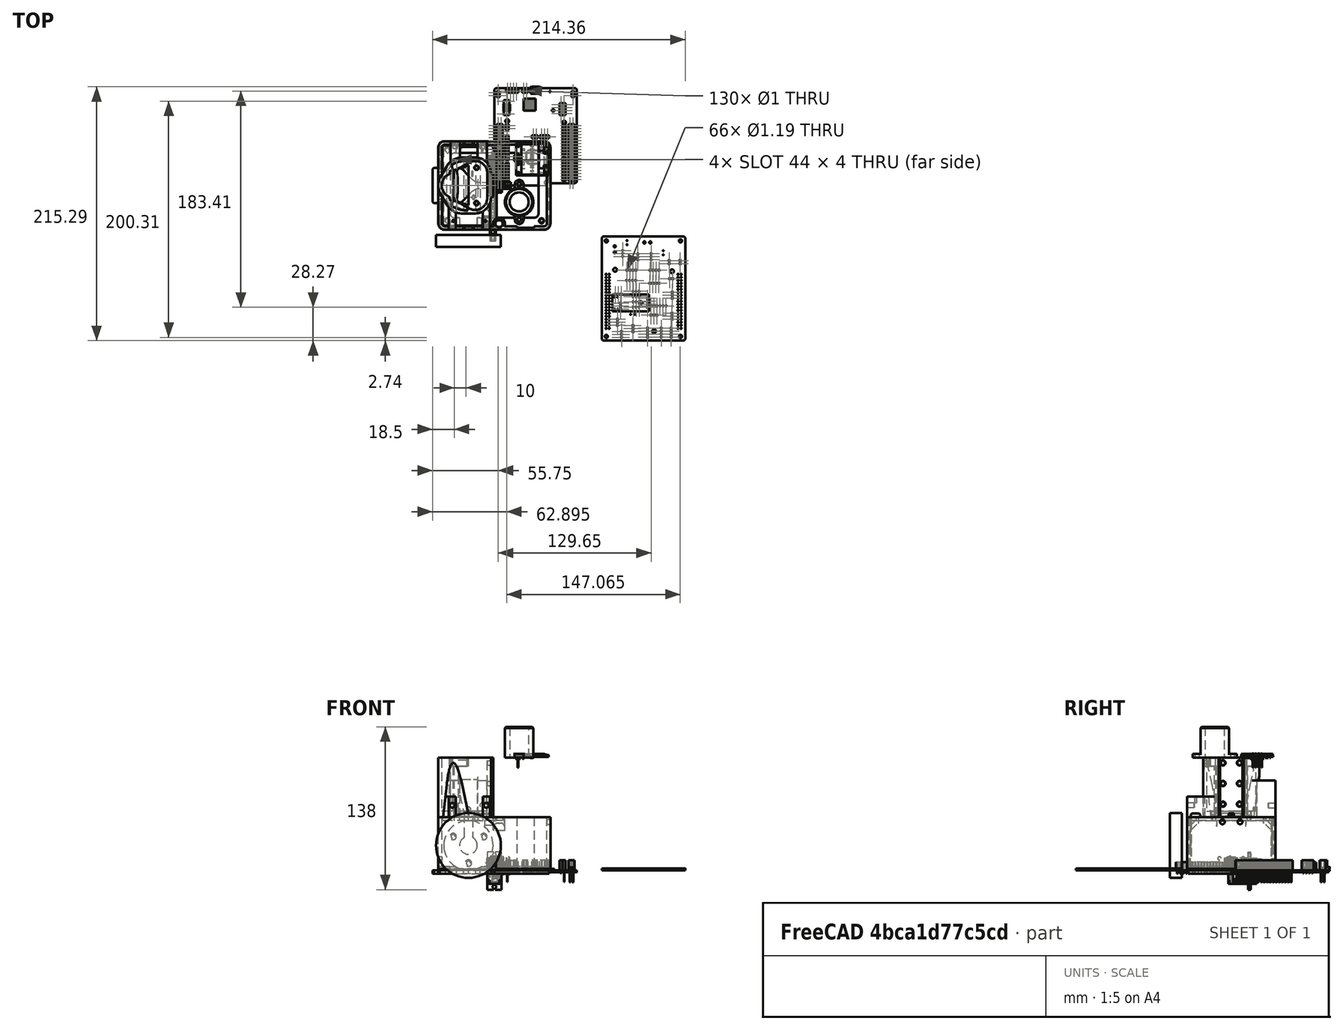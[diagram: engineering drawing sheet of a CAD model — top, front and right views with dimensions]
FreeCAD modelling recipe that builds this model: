
FCSTD DOCUMENT  (FreeCAD 1.0R38641 +678 (Git))
Label: Chassis_V3_PAMI
License: All rights reserved
LicenseURL: https://en.wikipedia.org/wiki/All_rights_reserved
objects: Part::Feature×336, Sketcher::SketchObject×61, App::Part×58, PartDesign::Pocket×46, PartDesign::Pad×18, PartDesign::Chamfer×15, PartDesign::Fillet×13, PartDesign::Body×8, PartDesign::Mirrored×7, Mesh::Feature×4, PartDesign::ShapeBinder×4, PartDesign::PolarPattern×3, PartDesign::Thickness×2, PartDesign::LinearPattern×2, PartDesign::Line×1, PartDesign::SubShapeBinder×1
note: 778 computed .brp shape members not serialized (recipe doc carries the construction recipe); baked Part::Feature solids carry a one-line shape summary decoded from their .brp
EXTERNAL_REF file=../MODEL PART/support_batterie_parkside_12V.FCStd obj=Part

FEATURE [Sketcher::SketchObject] Sketch
  ArcFitTolerance = 1e-06
  AttachmentSupport = -> [XY_Plane]
  FullyConstrained = true
  MakeInternals = false
  MapMode = 5
  sketch-geometry (5):
    g0: LineSegment StartX=47.5 StartY=-37.5 StartZ=0 EndX=47.5 EndY=37.5 EndZ=0
    g1: LineSegment StartX=47.5 StartY=37.5 StartZ=0 EndX=-47.5 EndY=37.5 EndZ=0
    g2: LineSegment StartX=-47.5 StartY=37.5 StartZ=0 EndX=-47.5 EndY=-37.5 EndZ=0
    g3: LineSegment StartX=-47.5 StartY=-37.5 StartZ=0 EndX=47.5 EndY=-37.5 EndZ=0
    g4: GeomPoint [constr] X=0 Y=0 Z=0
  constraints (12):
    c: Coincident(g0,g1)
    c: Coincident(g1,g2)
    c: Coincident(g2,g3)
    c: Coincident(g3,g0)
    c: Vertical(g0)
    c: Vertical(g2)
    c: Horizontal(g1)
    c: Horizontal(g3)
    c: Symmetric(g2,g0,g4)
    c: Coincident(g4,g-1)
    c: DistanceX(g1,g1) = 95
    c: DistanceY(g0,g0) = 75
FEATURE [PartDesign::Pad] Pad
  Direction = (0,0,1)
  Length = 45
  Length2 = 10
  Profile = -> Sketch
  ReferenceAxis = -> Sketch [N_Axis]
  Refine = true
  Suppressed = false
  Type = 0
FEATURE [PartDesign::Fillet] Fillet
  Base = -> Pad [Edge1,Edge2,Edge5,Edge8]
  BaseFeature = -> Pad
  Radius = 5
  Refine = true
  SupportTransform = false
  Suppressed = false
  UseAllEdges = false
FEATURE [PartDesign::Chamfer] Chamfer
  Angle = 45
  Base = -> Fillet [Edge7]
  BaseFeature = -> Fillet
  ChamferType = 0
  FlipDirection = false
  Refine = true
  Size = 1
  Size2 = 1
  SupportTransform = false
  Suppressed = false
  UseAllEdges = false
FEATURE [PartDesign::Thickness] Thickness
  Base = -> Chamfer [Face4]
  BaseFeature = -> Chamfer
  Intersection = true
  Join = 0
  Mode = 0
  Refine = true
  Reversed = true
  SupportTransform = false
  Suppressed = false
  Value = 3
FEATURE [Sketcher::SketchObject] Sketch001
  ArcFitTolerance = 1e-06
  AttachmentSupport = -> [Thickness]
  FullyConstrained = true
  MakeInternals = false
  MapMode = 5
  Placement = pos=(0,0,0) rot=(1,0,0;3.14159rad)
  sketch-geometry (5):
    g0: LineSegment StartX=-37.5 StartY=-27.5 StartZ=0 EndX=37.5 EndY=-27.5 EndZ=0
    g1: LineSegment StartX=37.5 StartY=-27.5 StartZ=0 EndX=37.5 EndY=27.5 EndZ=0
    g2: LineSegment StartX=37.5 StartY=27.5 StartZ=0 EndX=-37.5 EndY=27.5 EndZ=0
    g3: LineSegment StartX=-37.5 StartY=27.5 StartZ=0 EndX=-37.5 EndY=-27.5 EndZ=0
    g4: GeomPoint [constr] X=0 Y=0 Z=0
  constraints (12):
    c: Coincident(g0,g1)
    c: Coincident(g1,g2)
    c: Coincident(g2,g3)
    c: Coincident(g3,g0)
    c: Horizontal(g0)
    c: Horizontal(g2)
    c: Vertical(g1)
    c: Vertical(g3)
    c: Symmetric(g2,g0,g4)
    c: Coincident(g4,g-1)
    c: DistanceX(g2,g2) = 75
    c: DistanceY(g1,g1) = 55
FEATURE [PartDesign::Pocket] Pocket
  BaseFeature = -> Thickness
  Direction = (0,0,1)
  Length = 5
  Length2 = 5
  Profile = -> Sketch001
  ReferenceAxis = -> Sketch001 [N_Axis]
  Refine = true
  Suppressed = false
  Type = 1
FEATURE [PartDesign::Fillet] Fillet001
  Base = -> Pocket [Edge73,Edge75,Edge71,Edge69]
  BaseFeature = -> Pocket
  Radius = 4
  Refine = true
  SupportTransform = false
  Suppressed = false
  UseAllEdges = false
FEATURE [Sketcher::SketchObject] Sketch002
  ArcFitTolerance = 1e-06
  AttachmentSupport = -> [Fillet001]
  FullyConstrained = true
  MakeInternals = false
  MapMode = 5
  Placement = pos=(0,0,0) rot=(1,0,0;3.14159rad)
  sketch-geometry (6):
    g0: Circle CenterX=-40 CenterY=30 CenterZ=0 NormalX=0 NormalY=0 NormalZ=1 AngleXU=0 Radius=2.1
    g1: LineSegment [constr] StartX=-40 StartY=30 StartZ=0 EndX=-40 EndY=0 EndZ=0
    g2: LineSegment [constr] StartX=-40 StartY=0 StartZ=0 EndX=0 EndY=0 EndZ=0
    g3: LineSegment [constr] StartX=0 StartY=0 StartZ=0 EndX=0 EndY=30 EndZ=0
    g4: LineSegment [constr] StartX=0 StartY=30 StartZ=0 EndX=-40 EndY=30 EndZ=0
    g5: Circle CenterX=-40 CenterY=-30 CenterZ=0 NormalX=0 NormalY=0 NormalZ=1 AngleXU=0 Radius=2.1
  constraints (15):
    c: Diameter(g0) = 4.2
    c: Coincident(g1,g2)
    c: Coincident(g2,g3)
    c: Coincident(g3,g4)
    c: Coincident(g4,g1)
    c: Vertical(g1)
    c: Vertical(g3)
    c: Horizontal(g2)
    c: Horizontal(g4)
    c: Coincident(g1,g0)
    c: Coincident(g2,g-1)
    c: DistanceX(g4,g4) = 40
    c: DistanceY(g1,g1) = 30
    c: Equal(g5,g0)
    c: Symmetric(g0,g5,g2)
FEATURE [PartDesign::Pocket] Pocket001
  BaseFeature = -> Fillet001
  Direction = (0,0,1)
  Length = 5
  Length2 = 5
  Profile = -> Sketch002
  ReferenceAxis = -> Sketch002 [N_Axis]
  Refine = true
  Suppressed = false
  Type = 1
FEATURE [PartDesign::Chamfer] Chamfer001
  Angle = 45
  Base = -> Pocket001 [Edge9,Edge10]
  BaseFeature = -> Pocket001
  ChamferType = 0
  FlipDirection = false
  Refine = true
  Size = 0.4
  Size2 = 1
  SupportTransform = false
  Suppressed = false
  UseAllEdges = false
FEATURE [Sketcher::SketchObject] Sketch003
  ArcFitTolerance = 1e-06
  AttachmentSupport = -> [XZ_Plane]
  FullyConstrained = true
  MakeInternals = false
  MapMode = 5
  Placement = pos=(0,0,0) rot=(1,0,0;1.5708rad)
  sketch-geometry (1):
    g0: Circle CenterX=-22 CenterY=21 CenterZ=0 NormalX=0 NormalY=0 NormalZ=1 AngleXU=0 Radius=21
  constraints (3):
    c: Diameter(g0) = 42
    c: DistanceX(g0,g-1) = 22
    c: Tangent(g0,g-1)
FEATURE [PartDesign::Pocket] Pocket002
  BaseFeature = -> Chamfer001
  Direction = (0,1,-2e-16)
  Length = 69
  Length2 = 5
  Midplane = true
  Profile = -> Sketch003
  ReferenceAxis = -> Sketch003 [N_Axis]
  Refine = true
  Suppressed = false
  Type = 0
FEATURE [Sketcher::SketchObject] Sketch004
  ArcFitTolerance = 1e-06
  AttachmentSupport = -> [XZ_Plane]
  ExternalGeometry = -> [Sketch003]
  FullyConstrained = true
  MakeInternals = false
  MapMode = 5
  Placement = pos=(0,0,0) rot=(1,0,0;1.5708rad)
  sketch-geometry (1):
    g0: Circle CenterX=-22 CenterY=21 CenterZ=0 NormalX=0 NormalY=0 NormalZ=1 AngleXU=0 Radius=7.5
  constraints (2):
    c: Diameter(g0) = 15
    c: Coincident(g0,g-3)
FEATURE [PartDesign::Pocket] Pocket003
  BaseFeature = -> Pocket002
  Direction = (0,1,-2e-16)
  Length = 5
  Length2 = 5
  Midplane = true
  Profile = -> Sketch004
  ReferenceAxis = -> Sketch004 [N_Axis]
  Refine = true
  Suppressed = false
  Type = 1
FEATURE [Sketcher::SketchObject] Sketch005
  ArcFitTolerance = 1e-06
  AttachmentSupport = -> [XZ_Plane]
  ExternalGeometry = -> [Pocket003]
  FullyConstrained = true
  MakeInternals = false
  MapMode = 5
  Placement = pos=(0,0,0) rot=(1,0,0;1.5708rad)
  sketch-geometry (3):
    g0: Circle [constr] CenterX=-22 CenterY=21 CenterZ=0 NormalX=0 NormalY=0 NormalZ=1 AngleXU=0 Radius=15
    g1: LineSegment [constr] StartX=-22 StartY=21 StartZ=0 EndX=-22 EndY=6 EndZ=0
    g2: Circle CenterX=-22 CenterY=6 CenterZ=0 NormalX=0 NormalY=0 NormalZ=1 AngleXU=0 Radius=1.75
  constraints (7):
    c: Diameter(g0) = 30
    c: Coincident(g1,g0)
    c: PointOnObject(g1,g0)
    c: Vertical(g1)
    c: Coincident(g2,g1)
    c: Diameter(g2) = 3.5
    c: Coincident(g0,g-3)
FEATURE [PartDesign::Pocket] Pocket004
  BaseFeature = -> Pocket003
  Direction = (0,1,-2e-16)
  Length = 5
  Length2 = 5
  Midplane = true
  Profile = -> Sketch005
  ReferenceAxis = -> Sketch005 [N_Axis]
  Refine = true
  Suppressed = false
  Type = 1
FEATURE [PartDesign::Line] DatumLine
  AttacherType = Attacher::AttachEngineLine
  AttachmentSupport = -> [Pocket004]
  Length = 20
  MapMode = 19
  Placement = pos=(-22,37.5,21) rot=(1,0,0;1.5708rad)
  ResizeMode = 0
FEATURE [Sketcher::SketchObject] Sketch006
  ArcFitTolerance = 1e-06
  AttachmentSupport = -> [Pocket004]
  ExternalGeometry = -> [Pocket004]
  FullyConstrained = true
  MakeInternals = false
  MapMode = 5
  Placement = pos=(0,37.5,0) rot=(0,0.707107,0.707107;3.14159rad)
  sketch-geometry (1):
    g0: Circle CenterX=22 CenterY=6 CenterZ=0 NormalX=0 NormalY=0 NormalZ=1 AngleXU=0 Radius=2.75
  constraints (2):
    c: Coincident(g0,g-3)
    c: Diameter(g0) = 5.5
FEATURE [PartDesign::Pocket] Pocket005
  BaseFeature = -> Pocket004
  Direction = (0,-1,2e-16)
  Length = 1.5
  Length2 = 5
  Profile = -> Sketch006
  ReferenceAxis = -> Sketch006 [N_Axis]
  Refine = true
  Suppressed = false
  Type = 0
FEATURE [PartDesign::PolarPattern] PolarPattern001
  Angle = 360
  Axis = -> DatumLine
  BaseFeature = -> Pocket005
  Mode = 0
  Occurrences = 3
  Offset = 120
  Originals = -> [Pocket005,Pocket004]
  Refine = true
  Suppressed = false
  TransformMode = 0
FEATURE [Sketcher::SketchObject] Sketch007
  ArcFitTolerance = 1e-06
  AttachmentSupport = -> [PolarPattern001]
  ExternalGeometry = -> [PolarPattern001]
  FullyConstrained = true
  MakeInternals = false
  MapMode = 5
  Placement = pos=(0,-37.5,0) rot=(1,0,0;1.5708rad)
  sketch-geometry (1):
    g0: Circle CenterX=-22 CenterY=6 CenterZ=0 NormalX=0 NormalY=0 NormalZ=1 AngleXU=0 Radius=2.75
  constraints (2):
    c: Diameter(g0) = 5.5
    c: Coincident(g0,g-3)
FEATURE [PartDesign::Pocket] Pocket006
  BaseFeature = -> PolarPattern001
  Direction = (0,1,-2e-16)
  Length = 1.5
  Length2 = 5
  Profile = -> Sketch007
  ReferenceAxis = -> Sketch007 [N_Axis]
  Refine = true
  Suppressed = false
  Type = 0
FEATURE [PartDesign::PolarPattern] PolarPattern002
  Angle = 360
  Axis = -> DatumLine
  BaseFeature = -> Pocket006
  Mode = 0
  Occurrences = 3
  Offset = 120
  Originals = -> [Pocket006]
  Refine = true
  Suppressed = false
  TransformMode = 0
FEATURE [Sketcher::SketchObject] Sketch008
  ArcFitTolerance = 1e-06
  AttachmentSupport = -> [XZ_Plane]
  ExternalGeometry = -> [PolarPattern002]
  FullyConstrained = true
  MakeInternals = false
  MapMode = 5
  Placement = pos=(0,0,0) rot=(1,0,0;1.5708rad)
  sketch-geometry (5):
    g0: LineSegment StartX=-18.5 StartY=21 StartZ=0 EndX=-18.5 EndY=45 EndZ=0
    g1: LineSegment StartX=-18.5 StartY=45 StartZ=0 EndX=-25.5 EndY=45 EndZ=0
    g2: LineSegment StartX=-25.5 StartY=45 StartZ=0 EndX=-25.5 EndY=21 EndZ=0
    g3: LineSegment StartX=-25.5 StartY=21 StartZ=0 EndX=-18.5 EndY=21 EndZ=0
    g4: GeomPoint [constr] X=-22 Y=33 Z=0
  constraints (12):
    c: Coincident(g0,g1)
    c: Coincident(g1,g2)
    c: Coincident(g2,g3)
    c: Coincident(g3,g0)
    c: Vertical(g0)
    c: Vertical(g2)
    c: Horizontal(g1)
    c: Horizontal(g3)
    c: Symmetric(g2,g0,g4)
    c: PointOnObject(g1,g-3)
    c: DistanceX(g1,g1) = 7
    c: Symmetric(g2,g0,g-4)
FEATURE [PartDesign::Pocket] Pocket007
  BaseFeature = -> PolarPattern002
  Direction = (0,1,-2e-16)
  Length = 5
  Length2 = 5
  Midplane = true
  Profile = -> Sketch008
  ReferenceAxis = -> Sketch008 [N_Axis]
  Refine = true
  Suppressed = false
  Type = 1
FEATURE [PartDesign::Chamfer] Chamfer002
  Angle = 45
  Base = -> Pocket007 [Edge128,Edge127,Edge148,Edge144,Edge125,Edge131,Edge119,Edge130]
  BaseFeature = -> Pocket007
  ChamferType = 0
  FlipDirection = false
  Refine = true
  Size = 1
  Size2 = 1
  SupportTransform = false
  Suppressed = false
  UseAllEdges = false
FEATURE [Part::Feature] Part__Feature027  label="PinSocket_2x19_P254mm_Vertical"
  shape: bbox 5.08 x 48.26 x 10.1 mm, 1188 faces (baked)
FEATURE [App::Part] PinSocket_2x19_P2_54mm_Vertical  label="PinSocket_2x19_P2.54mm_Vertical"
  Group = -> [Part__Feature027]
  Origin = -> Origin029
  Placement = pos=(97.2797,-75.37,1.65) rot=(0,0,1;0rad)
FEATURE [Part::Feature] Part__Feature028  label="PinSocket_2x19_P254mm_Vertical001"
  shape: bbox 5.08 x 48.26 x 10.1 mm, 1188 faces (baked)
FEATURE [App::Part] PinSocket_2x19_P2_54mm_Vertical001  label="PinSocket_2x19_P2.54mm_Vertical001"
  Group = -> [Part__Feature028]
  Origin = -> Origin030
  Placement = pos=(158.25,-75.37,1.65) rot=(0,0,1;0rad)
FEATURE [Part::Feature] Part__Feature029  label="PCB"
  shape: bbox 70 x 82.5 x 1.644 mm, 168 faces (baked)
FEATURE [Part::Feature] Part__Feature030  label="PCB001"
  shape: bbox 12 x 12 x 1.56 mm, 842 faces (baked)
FEATURE [Part::Feature] Part__Feature031  label="PCB002"
  shape: bbox 10.1 x 10.1 x 1.6 mm, 6 faces (baked)
FEATURE [Part::Feature] Part__Feature032  label="PCB003"
  shape: bbox 2.54 x 5.207 x 2.54 mm, 69 faces (baked)
FEATURE [Part::Feature] Part__Feature033  label="PCB004"
  shape: bbox 0.889 x 3.429 x 10.92 mm, 38 faces (baked)
FEATURE [Part::Feature] Part__Feature034  label="PCB005"
  shape: bbox 2.599 x 5.159 x 8.38 mm, 6 faces (baked)
FEATURE [Part::Feature] Part__Feature035  label="PCB006"
  shape: bbox 2.54 x 5.207 x 2.54 mm, 69 faces (baked)
FEATURE [Part::Feature] Part__Feature036  label="PCB007"
  shape: bbox 0.889 x 3.429 x 10.92 mm, 38 faces (baked)
FEATURE [Part::Feature] Part__Feature037  label="PCB008"
  shape: bbox 2.599 x 5.159 x 8.38 mm, 6 faces (baked)
FEATURE [Part::Feature] Part__Feature038  label="PCB009"
  shape: bbox 7.62 x 2.54 x 10.92 mm, 160 faces (baked)
FEATURE [Part::Feature] Part__Feature039  label="PCB010"
  shape: bbox 7.83 x 2.75 x 8.38 mm, 6 faces (baked)
FEATURE [Part::Feature] Part__Feature040  label="PCB011"
  shape: bbox 8.2 x 5.4 x 3.3 mm, 428 faces (baked)
FEATURE [Part::Feature] Part__Feature041  label="PCB012"
  shape: bbox 7.999 x 4.599 x 2.9 mm, 6 faces (baked)
FEATURE [Part::Feature] Part__Feature042  label="PCB013"
  shape: bbox 8.12 x 5.42 x 2.9 mm, 6 faces (baked)
FEATURE [Part::Feature] Part__Feature043  label="PCB014"
  shape: bbox 0.8 x 0.4 x 0.002 mm, 10 faces (baked)
FEATURE [Part::Feature] Part__Feature044  label="PCB015"
  shape: bbox 0.7 x 1 x 0.4 mm, 14 faces (baked)
FEATURE [Part::Feature] Part__Feature045  label="PCB016"
  shape: bbox 0.8 x 0.4 x 0.2 mm, 8 faces (baked)
FEATURE [Part::Feature] Part__Feature046  label="PCB017"
  shape: bbox 0.8 x 0.8 x 0.2 mm, 6 faces (baked)
FEATURE [Part::Feature] Part__Feature047  label="PCB018"
  shape: bbox 0.81 x 1.51 x 0.6 mm, 6 faces (baked)
FEATURE [Part::Feature] Part__Feature048  label="PCB019"
  shape: bbox 5.207 x 2.54 x 2.54 mm, 69 faces (baked)
FEATURE [Part::Feature] Part__Feature049  label="PCB020"
  shape: bbox 3.429 x 0.889 x 10.92 mm, 38 faces (baked)
FEATURE [Part::Feature] Part__Feature050  label="PCB021"
  shape: bbox 5.159 x 2.599 x 8.38 mm, 6 faces (baked)
FEATURE [Part::Feature] Part__Feature051  label="PCB022"
  shape: bbox 2.6 x 1.35 x 1.1 mm, 38 faces (baked)
FEATURE [Part::Feature] Part__Feature052  label="PCB023"
  shape: bbox 1.92 x 1.57 x 1.17 mm, 6 faces (baked)
FEATURE [Part::Feature] Part__Feature053  label="PCB024"
  shape: bbox 0.5 x 0.5 x 0.01 mm, 3 faces (baked)
FEATURE [Part::Feature] Part__Feature054  label="PCB025"
  shape: bbox 10.15 x 10.15 x 0.45 mm, 6 faces (baked)
FEATURE [Part::Feature] Part__Feature055  label="PCB026"
  shape: bbox 0.29 x 0.29 x 0.29 mm, 1 faces (baked)
FEATURE [Part::Feature] Part__Feature056  label="PCB027"
  shape: bbox 0.29 x 0.29 x 0.29 mm, 1 faces (baked)
FEATURE [Part::Feature] Part__Feature057  label="PCB028"
  shape: bbox 0.29 x 0.29 x 0.29 mm, 1 faces (baked)
FEATURE [Part::Feature] Part__Feature058  label="PCB029"
  shape: bbox 0.29 x 0.29 x 0.29 mm, 1 faces (baked)
FEATURE [Part::Feature] Part__Feature059  label="PCB030"
  shape: bbox 0.29 x 0.29 x 0.29 mm, 1 faces (baked)
FEATURE [Part::Feature] Part__Feature060  label="PCB031"
  shape: bbox 0.29 x 0.29 x 0.29 mm, 1 faces (baked)
FEATURE [Part::Feature] Part__Feature061  label="PCB032"
  shape: bbox 0.29 x 0.29 x 0.29 mm, 1 faces (baked)
FEATURE [Part::Feature] Part__Feature062  label="PCB033"
  shape: bbox 0.29 x 0.29 x 0.29 mm, 1 faces (baked)
FEATURE [Part::Feature] Part__Feature063  label="PCB034"
  shape: bbox 0.29 x 0.29 x 0.29 mm, 1 faces (baked)
FEATURE [Part::Feature] Part__Feature064  label="PCB035"
  shape: bbox 0.29 x 0.29 x 0.29 mm, 1 faces (baked)
FEATURE [Part::Feature] Part__Feature065  label="PCB036"
  shape: bbox 0.29 x 0.29 x 0.29 mm, 1 faces (baked)
FEATURE [Part::Feature] Part__Feature066  label="PCB037"
  shape: bbox 0.29 x 0.29 x 0.29 mm, 1 faces (baked)
FEATURE [Part::Feature] Part__Feature067  label="PCB038"
  shape: bbox 0.29 x 0.29 x 0.29 mm, 1 faces (baked)
FEATURE [Part::Feature] Part__Feature068  label="PCB039"
  shape: bbox 0.29 x 0.29 x 0.29 mm, 1 faces (baked)
FEATURE [Part::Feature] Part__Feature069  label="PCB040"
  shape: bbox 0.29 x 0.29 x 0.29 mm, 1 faces (baked)
FEATURE [Part::Feature] Part__Feature070  label="PCB041"
  shape: bbox 0.29 x 0.29 x 0.29 mm, 1 faces (baked)
FEATURE [Part::Feature] Part__Feature071  label="PCB042"
  shape: bbox 0.29 x 0.29 x 0.29 mm, 1 faces (baked)
FEATURE [Part::Feature] Part__Feature072  label="PCB043"
  shape: bbox 0.29 x 0.29 x 0.29 mm, 1 faces (baked)
FEATURE [Part::Feature] Part__Feature073  label="PCB044"
  shape: bbox 0.29 x 0.29 x 0.29 mm, 1 faces (baked)
FEATURE [Part::Feature] Part__Feature074  label="PCB045"
  shape: bbox 0.29 x 0.29 x 0.29 mm, 1 faces (baked)
FEATURE [Part::Feature] Part__Feature075  label="PCB046"
  shape: bbox 0.29 x 0.29 x 0.29 mm, 1 faces (baked)
FEATURE [Part::Feature] Part__Feature076  label="PCB047"
  shape: bbox 0.29 x 0.29 x 0.29 mm, 1 faces (baked)
FEATURE [Part::Feature] Part__Feature077  label="PCB048"
  shape: bbox 0.29 x 0.29 x 0.29 mm, 1 faces (baked)
FEATURE [Part::Feature] Part__Feature078  label="PCB049"
  shape: bbox 0.29 x 0.29 x 0.29 mm, 1 faces (baked)
FEATURE [Part::Feature] Part__Feature079  label="PCB050"
  shape: bbox 0.29 x 0.29 x 0.29 mm, 1 faces (baked)
FEATURE [Part::Feature] Part__Feature080  label="PCB051"
  shape: bbox 0.29 x 0.29 x 0.29 mm, 1 faces (baked)
FEATURE [Part::Feature] Part__Feature081  label="PCB052"
  shape: bbox 0.29 x 0.29 x 0.29 mm, 1 faces (baked)
FEATURE [Part::Feature] Part__Feature082  label="PCB053"
  shape: bbox 0.29 x 0.29 x 0.29 mm, 1 faces (baked)
FEATURE [Part::Feature] Part__Feature083  label="PCB054"
  shape: bbox 0.29 x 0.29 x 0.29 mm, 1 faces (baked)
FEATURE [Part::Feature] Part__Feature084  label="PCB055"
  shape: bbox 0.29 x 0.29 x 0.29 mm, 1 faces (baked)
FEATURE [Part::Feature] Part__Feature085  label="PCB056"
  shape: bbox 0.29 x 0.29 x 0.29 mm, 1 faces (baked)
FEATURE [Part::Feature] Part__Feature086  label="PCB057"
  shape: bbox 0.29 x 0.29 x 0.29 mm, 1 faces (baked)
FEATURE [Part::Feature] Part__Feature087  label="PCB058"
  shape: bbox 0.29 x 0.29 x 0.29 mm, 1 faces (baked)
FEATURE [Part::Feature] Part__Feature088  label="PCB059"
  shape: bbox 0.29 x 0.29 x 0.29 mm, 1 faces (baked)
FEATURE [Part::Feature] Part__Feature089  label="PCB060"
  shape: bbox 0.29 x 0.29 x 0.29 mm, 1 faces (baked)
FEATURE [Part::Feature] Part__Feature090  label="PCB061"
  shape: bbox 0.29 x 0.29 x 0.29 mm, 1 faces (baked)
FEATURE [Part::Feature] Part__Feature091  label="PCB062"
  shape: bbox 0.29 x 0.29 x 0.29 mm, 1 faces (baked)
FEATURE [Part::Feature] Part__Feature092  label="PCB063"
  shape: bbox 0.29 x 0.29 x 0.29 mm, 1 faces (baked)
FEATURE [Part::Feature] Part__Feature093  label="PCB064"
  shape: bbox 0.29 x 0.29 x 0.29 mm, 1 faces (baked)
FEATURE [Part::Feature] Part__Feature094  label="PCB065"
  shape: bbox 0.29 x 0.29 x 0.29 mm, 1 faces (baked)
FEATURE [Part::Feature] Part__Feature095  label="PCB066"
  shape: bbox 0.29 x 0.29 x 0.29 mm, 1 faces (baked)
FEATURE [Part::Feature] Part__Feature096  label="PCB067"
  shape: bbox 0.29 x 0.29 x 0.29 mm, 1 faces (baked)
FEATURE [Part::Feature] Part__Feature097  label="PCB068"
  shape: bbox 0.29 x 0.29 x 0.29 mm, 1 faces (baked)
FEATURE [Part::Feature] Part__Feature098  label="PCB069"
  shape: bbox 0.29 x 0.29 x 0.29 mm, 1 faces (baked)
FEATURE [Part::Feature] Part__Feature099  label="PCB070"
  shape: bbox 0.29 x 0.29 x 0.29 mm, 1 faces (baked)
FEATURE [Part::Feature] Part__Feature100  label="PCB071"
  shape: bbox 0.29 x 0.29 x 0.29 mm, 1 faces (baked)
FEATURE [Part::Feature] Part__Feature101  label="PCB072"
  shape: bbox 0.29 x 0.29 x 0.29 mm, 1 faces (baked)
FEATURE [Part::Feature] Part__Feature102  label="PCB073"
  shape: bbox 0.29 x 0.29 x 0.29 mm, 1 faces (baked)
FEATURE [Part::Feature] Part__Feature103  label="PCB074"
  shape: bbox 0.29 x 0.29 x 0.29 mm, 1 faces (baked)
FEATURE [Part::Feature] Part__Feature104  label="PCB075"
  shape: bbox 0.29 x 0.29 x 0.29 mm, 1 faces (baked)
FEATURE [Part::Feature] Part__Feature105  label="PCB076"
  shape: bbox 0.29 x 0.29 x 0.29 mm, 1 faces (baked)
FEATURE [Part::Feature] Part__Feature106  label="PCB077"
  shape: bbox 0.29 x 0.29 x 0.29 mm, 1 faces (baked)
FEATURE [Part::Feature] Part__Feature107  label="PCB078"
  shape: bbox 0.29 x 0.29 x 0.29 mm, 1 faces (baked)
FEATURE [Part::Feature] Part__Feature108  label="PCB079"
  shape: bbox 0.29 x 0.29 x 0.29 mm, 1 faces (baked)
FEATURE [Part::Feature] Part__Feature109  label="PCB080"
  shape: bbox 0.29 x 0.29 x 0.29 mm, 1 faces (baked)
FEATURE [Part::Feature] Part__Feature110  label="PCB081"
  shape: bbox 0.29 x 0.29 x 0.29 mm, 1 faces (baked)
FEATURE [Part::Feature] Part__Feature111  label="PCB082"
  shape: bbox 0.29 x 0.29 x 0.29 mm, 1 faces (baked)
FEATURE [Part::Feature] Part__Feature112  label="PCB083"
  shape: bbox 0.29 x 0.29 x 0.29 mm, 1 faces (baked)
FEATURE [Part::Feature] Part__Feature113  label="PCB084"
  shape: bbox 0.29 x 0.29 x 0.29 mm, 1 faces (baked)
FEATURE [Part::Feature] Part__Feature114  label="PCB085"
  shape: bbox 0.29 x 0.29 x 0.29 mm, 1 faces (baked)
FEATURE [Part::Feature] Part__Feature115  label="PCB086"
  shape: bbox 0.29 x 0.29 x 0.29 mm, 1 faces (baked)
FEATURE [Part::Feature] Part__Feature116  label="PCB087"
  shape: bbox 0.29 x 0.29 x 0.29 mm, 1 faces (baked)
FEATURE [Part::Feature] Part__Feature117  label="PCB088"
  shape: bbox 0.29 x 0.29 x 0.29 mm, 1 faces (baked)
FEATURE [Part::Feature] Part__Feature118  label="PCB089"
  shape: bbox 0.29 x 0.29 x 0.29 mm, 1 faces (baked)
FEATURE [Part::Feature] Part__Feature119  label="PCB090"
  shape: bbox 0.29 x 0.29 x 0.29 mm, 1 faces (baked)
FEATURE [Part::Feature] Part__Feature120  label="PCB091"
  shape: bbox 0.29 x 0.29 x 0.29 mm, 1 faces (baked)
FEATURE [Part::Feature] Part__Feature121  label="PCB092"
  shape: bbox 0.29 x 0.29 x 0.29 mm, 1 faces (baked)
FEATURE [Part::Feature] Part__Feature122  label="PCB093"
  shape: bbox 0.29 x 0.29 x 0.29 mm, 1 faces (baked)
FEATURE [Part::Feature] Part__Feature123  label="PCB094"
  shape: bbox 0.29 x 0.29 x 0.29 mm, 1 faces (baked)
FEATURE [Part::Feature] Part__Feature124  label="PCB095"
  shape: bbox 0.29 x 0.29 x 0.29 mm, 1 faces (baked)
FEATURE [Part::Feature] Part__Feature125  label="PCB096"
  shape: bbox 0.29 x 0.29 x 0.29 mm, 1 faces (baked)
FEATURE [Part::Feature] Part__Feature126  label="PCB097"
  shape: bbox 0.29 x 0.29 x 0.29 mm, 1 faces (baked)
FEATURE [Part::Feature] Part__Feature127  label="PCB098"
  shape: bbox 0.29 x 0.29 x 0.29 mm, 1 faces (baked)
FEATURE [Part::Feature] Part__Feature128  label="PCB099"
  shape: bbox 0.29 x 0.29 x 0.29 mm, 1 faces (baked)
FEATURE [Part::Feature] Part__Feature129  label="PCB100"
  shape: bbox 0.29 x 0.29 x 0.29 mm, 1 faces (baked)
FEATURE [Part::Feature] Part__Feature130  label="PCB101"
  shape: bbox 0.29 x 0.29 x 0.29 mm, 1 faces (baked)
FEATURE [Part::Feature] Part__Feature131  label="PCB102"
  shape: bbox 0.29 x 0.29 x 0.29 mm, 1 faces (baked)
FEATURE [Part::Feature] Part__Feature132  label="PCB103"
  shape: bbox 0.29 x 0.29 x 0.29 mm, 1 faces (baked)
FEATURE [Part::Feature] Part__Feature133  label="PCB104"
  shape: bbox 0.29 x 0.29 x 0.29 mm, 1 faces (baked)
FEATURE [Part::Feature] Part__Feature134  label="PCB105"
  shape: bbox 0.29 x 0.29 x 0.29 mm, 1 faces (baked)
FEATURE [Part::Feature] Part__Feature135  label="PCB106"
  shape: bbox 0.29 x 0.29 x 0.29 mm, 1 faces (baked)
FEATURE [Part::Feature] Part__Feature136  label="PCB107"
  shape: bbox 0.29 x 0.29 x 0.29 mm, 1 faces (baked)
FEATURE [Part::Feature] Part__Feature137  label="PCB108"
  shape: bbox 0.29 x 0.29 x 0.29 mm, 1 faces (baked)
FEATURE [Part::Feature] Part__Feature138  label="PCB109"
  shape: bbox 0.29 x 0.29 x 0.29 mm, 1 faces (baked)
FEATURE [Part::Feature] Part__Feature139  label="PCB110"
  shape: bbox 0.29 x 0.29 x 0.29 mm, 1 faces (baked)
FEATURE [Part::Feature] Part__Feature140  label="PCB111"
  shape: bbox 0.29 x 0.29 x 0.29 mm, 1 faces (baked)
FEATURE [Part::Feature] Part__Feature141  label="PCB112"
  shape: bbox 0.29 x 0.29 x 0.29 mm, 1 faces (baked)
FEATURE [Part::Feature] Part__Feature142  label="PCB113"
  shape: bbox 0.29 x 0.29 x 0.29 mm, 1 faces (baked)
FEATURE [Part::Feature] Part__Feature143  label="PCB114"
  shape: bbox 0.29 x 0.29 x 0.29 mm, 1 faces (baked)
FEATURE [Part::Feature] Part__Feature144  label="PCB115"
  shape: bbox 0.29 x 0.29 x 0.29 mm, 1 faces (baked)
FEATURE [Part::Feature] Part__Feature145  label="PCB116"
  shape: bbox 0.29 x 0.29 x 0.29 mm, 1 faces (baked)
FEATURE [Part::Feature] Part__Feature146  label="PCB117"
  shape: bbox 0.29 x 0.29 x 0.29 mm, 1 faces (baked)
FEATURE [Part::Feature] Part__Feature147  label="PCB118"
  shape: bbox 0.29 x 0.29 x 0.29 mm, 1 faces (baked)
FEATURE [Part::Feature] Part__Feature148  label="PCB119"
  shape: bbox 0.29 x 0.29 x 0.29 mm, 1 faces (baked)
FEATURE [Part::Feature] Part__Feature149  label="PCB120"
  shape: bbox 0.29 x 0.29 x 0.29 mm, 1 faces (baked)
FEATURE [Part::Feature] Part__Feature150  label="PCB121"
  shape: bbox 0.29 x 0.29 x 0.29 mm, 1 faces (baked)
FEATURE [Part::Feature] Part__Feature151  label="PCB122"
  shape: bbox 0.29 x 0.29 x 0.29 mm, 1 faces (baked)
FEATURE [Part::Feature] Part__Feature152  label="PCB123"
  shape: bbox 0.29 x 0.29 x 0.29 mm, 1 faces (baked)
FEATURE [Part::Feature] Part__Feature153  label="PCB124"
  shape: bbox 0.29 x 0.29 x 0.29 mm, 1 faces (baked)
FEATURE [Part::Feature] Part__Feature154  label="PCB125"
  shape: bbox 0.29 x 0.29 x 0.29 mm, 1 faces (baked)
FEATURE [Part::Feature] Part__Feature155  label="PCB126"
  shape: bbox 0.29 x 0.29 x 0.29 mm, 1 faces (baked)
FEATURE [Part::Feature] Part__Feature156  label="PCB127"
  shape: bbox 0.29 x 0.29 x 0.29 mm, 1 faces (baked)
FEATURE [Part::Feature] Part__Feature157  label="PCB128"
  shape: bbox 0.29 x 0.29 x 0.29 mm, 1 faces (baked)
FEATURE [Part::Feature] Part__Feature158  label="PCB129"
  shape: bbox 0.29 x 0.29 x 0.29 mm, 1 faces (baked)
FEATURE [Part::Feature] Part__Feature159  label="PCB130"
  shape: bbox 0.29 x 0.29 x 0.29 mm, 1 faces (baked)
FEATURE [Part::Feature] Part__Feature160  label="PCB131"
  shape: bbox 0.29 x 0.29 x 0.29 mm, 1 faces (baked)
FEATURE [Part::Feature] Part__Feature161  label="PCB132"
  shape: bbox 0.29 x 0.29 x 0.29 mm, 1 faces (baked)
FEATURE [Part::Feature] Part__Feature162  label="PCB133"
  shape: bbox 0.29 x 0.29 x 0.29 mm, 1 faces (baked)
FEATURE [Part::Feature] Part__Feature163  label="PCB134"
  shape: bbox 0.29 x 0.29 x 0.29 mm, 1 faces (baked)
FEATURE [Part::Feature] Part__Feature164  label="PCB135"
  shape: bbox 0.29 x 0.29 x 0.29 mm, 1 faces (baked)
FEATURE [Part::Feature] Part__Feature165  label="PCB136"
  shape: bbox 0.29 x 0.29 x 0.29 mm, 1 faces (baked)
FEATURE [Part::Feature] Part__Feature166  label="PCB137"
  shape: bbox 0.29 x 0.29 x 0.29 mm, 1 faces (baked)
FEATURE [Part::Feature] Part__Feature167  label="PCB138"
  shape: bbox 0.29 x 0.29 x 0.29 mm, 1 faces (baked)
FEATURE [Part::Feature] Part__Feature168  label="PCB139"
  shape: bbox 0.29 x 0.29 x 0.29 mm, 1 faces (baked)
FEATURE [Part::Feature] Part__Feature169  label="PCB140"
  shape: bbox 0.29 x 0.29 x 0.29 mm, 1 faces (baked)
FEATURE [Part::Feature] Part__Feature170  label="PCB141"
  shape: bbox 0.29 x 0.29 x 0.29 mm, 1 faces (baked)
FEATURE [Part::Feature] Part__Feature171  label="PCB142"
  shape: bbox 0.29 x 0.29 x 0.29 mm, 1 faces (baked)
FEATURE [Part::Feature] Part__Feature172  label="PCB143"
  shape: bbox 0.29 x 0.29 x 0.29 mm, 1 faces (baked)
FEATURE [Part::Feature] Part__Feature173  label="PCB144"
  shape: bbox 0.29 x 0.29 x 0.29 mm, 1 faces (baked)
FEATURE [Part::Feature] Part__Feature174  label="PCB145"
  shape: bbox 0.29 x 0.29 x 0.29 mm, 1 faces (baked)
FEATURE [Part::Feature] Part__Feature175  label="PCB146"
  shape: bbox 0.29 x 0.29 x 0.29 mm, 1 faces (baked)
FEATURE [Part::Feature] Part__Feature176  label="PCB147"
  shape: bbox 0.29 x 0.29 x 0.29 mm, 1 faces (baked)
FEATURE [Part::Feature] Part__Feature177  label="PCB148"
  shape: bbox 0.29 x 0.29 x 0.29 mm, 1 faces (baked)
FEATURE [Part::Feature] Part__Feature178  label="PCB149"
  shape: bbox 0.29 x 0.29 x 0.29 mm, 1 faces (baked)
FEATURE [Part::Feature] Part__Feature179  label="PCB150"
  shape: bbox 0.29 x 0.29 x 0.29 mm, 1 faces (baked)
FEATURE [Part::Feature] Part__Feature180  label="PCB151"
  shape: bbox 0.29 x 0.29 x 0.29 mm, 1 faces (baked)
FEATURE [Part::Feature] Part__Feature181  label="PCB152"
  shape: bbox 0.29 x 0.29 x 0.29 mm, 1 faces (baked)
FEATURE [Part::Feature] Part__Feature182  label="PCB153"
  shape: bbox 0.29 x 0.29 x 0.29 mm, 1 faces (baked)
FEATURE [Part::Feature] Part__Feature183  label="PCB154"
  shape: bbox 0.29 x 0.29 x 0.29 mm, 1 faces (baked)
FEATURE [Part::Feature] Part__Feature184  label="PCB155"
  shape: bbox 0.29 x 0.29 x 0.29 mm, 1 faces (baked)
FEATURE [Part::Feature] Part__Feature185  label="PCB156"
  shape: bbox 0.29 x 0.29 x 0.29 mm, 1 faces (baked)
FEATURE [Part::Feature] Part__Feature186  label="PCB157"
  shape: bbox 0.29 x 0.29 x 0.29 mm, 1 faces (baked)
FEATURE [Part::Feature] Part__Feature187  label="PCB158"
  shape: bbox 0.29 x 0.29 x 0.29 mm, 1 faces (baked)
FEATURE [Part::Feature] Part__Feature188  label="PCB159"
  shape: bbox 0.29 x 0.29 x 0.29 mm, 1 faces (baked)
FEATURE [Part::Feature] Part__Feature189  label="PCB160"
  shape: bbox 0.29 x 0.29 x 0.29 mm, 1 faces (baked)
FEATURE [Part::Feature] Part__Feature190  label="PCB161"
  shape: bbox 0.29 x 0.29 x 0.29 mm, 1 faces (baked)
FEATURE [Part::Feature] Part__Feature191  label="PCB162"
  shape: bbox 0.29 x 0.29 x 0.29 mm, 1 faces (baked)
FEATURE [Part::Feature] Part__Feature192  label="PCB163"
  shape: bbox 0.29 x 0.29 x 0.29 mm, 1 faces (baked)
FEATURE [Part::Feature] Part__Feature193  label="PCB164"
  shape: bbox 0.29 x 0.29 x 0.29 mm, 1 faces (baked)
FEATURE [Part::Feature] Part__Feature194  label="PCB165"
  shape: bbox 0.29 x 0.29 x 0.29 mm, 1 faces (baked)
FEATURE [Part::Feature] Part__Feature195  label="PCB166"
  shape: bbox 0.29 x 0.29 x 0.29 mm, 1 faces (baked)
FEATURE [Part::Feature] Part__Feature196  label="PCB167"
  shape: bbox 0.29 x 0.29 x 0.29 mm, 1 faces (baked)
FEATURE [Part::Feature] Part__Feature197  label="PCB168"
  shape: bbox 0.29 x 0.29 x 0.29 mm, 1 faces (baked)
FEATURE [Part::Feature] Part__Feature198  label="PCB169"
  shape: bbox 0.29 x 0.29 x 0.29 mm, 1 faces (baked)
FEATURE [Part::Feature] Part__Feature199  label="PCB170"
  shape: bbox 0.29 x 0.29 x 0.29 mm, 1 faces (baked)
FEATURE [Part::Feature] Part__Feature200  label="PCB171"
  shape: bbox 0.29 x 0.29 x 0.29 mm, 1 faces (baked)
FEATURE [Part::Feature] Part__Feature201  label="PCB172"
  shape: bbox 0.29 x 0.29 x 0.29 mm, 1 faces (baked)
FEATURE [Part::Feature] Part__Feature202  label="PCB173"
  shape: bbox 0.29 x 0.29 x 0.29 mm, 1 faces (baked)
FEATURE [Part::Feature] Part__Feature203  label="PCB174"
  shape: bbox 0.29 x 0.29 x 0.29 mm, 1 faces (baked)
FEATURE [Part::Feature] Part__Feature204  label="PCB175"
  shape: bbox 0.29 x 0.29 x 0.29 mm, 1 faces (baked)
FEATURE [Part::Feature] Part__Feature205  label="PCB176"
  shape: bbox 0.29 x 0.29 x 0.29 mm, 1 faces (baked)
FEATURE [Part::Feature] Part__Feature206  label="PCB177"
  shape: bbox 0.29 x 0.29 x 0.29 mm, 1 faces (baked)
FEATURE [Part::Feature] Part__Feature207  label="PCB178"
  shape: bbox 0.29 x 0.29 x 0.29 mm, 1 faces (baked)
FEATURE [Part::Feature] Part__Feature208  label="PCB179"
  shape: bbox 0.29 x 0.29 x 0.29 mm, 1 faces (baked)
FEATURE [Part::Feature] Part__Feature209  label="PCB180"
  shape: bbox 0.29 x 0.29 x 0.29 mm, 1 faces (baked)
FEATURE [Part::Feature] Part__Feature210  label="PCB181"
  shape: bbox 0.29 x 0.29 x 0.29 mm, 1 faces (baked)
FEATURE [Part::Feature] Part__Feature211  label="PCB182"
  shape: bbox 0.29 x 0.29 x 0.29 mm, 1 faces (baked)
FEATURE [Part::Feature] Part__Feature212  label="PCB183"
  shape: bbox 0.29 x 0.29 x 0.29 mm, 1 faces (baked)
FEATURE [Part::Feature] Part__Feature213  label="PCB184"
  shape: bbox 0.29 x 0.29 x 0.29 mm, 1 faces (baked)
FEATURE [Part::Feature] Part__Feature214  label="PCB185"
  shape: bbox 0.29 x 0.29 x 0.29 mm, 1 faces (baked)
FEATURE [Part::Feature] Part__Feature215  label="PCB186"
  shape: bbox 0.29 x 0.29 x 0.29 mm, 1 faces (baked)
FEATURE [Part::Feature] Part__Feature216  label="PCB187"
  shape: bbox 0.29 x 0.29 x 0.29 mm, 1 faces (baked)
FEATURE [Part::Feature] Part__Feature217  label="PCB188"
  shape: bbox 0.29 x 0.29 x 0.29 mm, 1 faces (baked)
FEATURE [Part::Feature] Part__Feature218  label="PCB189"
  shape: bbox 0.29 x 0.29 x 0.29 mm, 1 faces (baked)
FEATURE [Part::Feature] Part__Feature219  label="PCB190"
  shape: bbox 0.29 x 0.29 x 0.29 mm, 1 faces (baked)
FEATURE [Part::Feature] Part__Feature220  label="PCB191"
  shape: bbox 0.29 x 0.29 x 0.29 mm, 1 faces (baked)
FEATURE [Part::Feature] Part__Feature221  label="PCB192"
  shape: bbox 0.29 x 0.29 x 0.29 mm, 1 faces (baked)
FEATURE [Part::Feature] Part__Feature222  label="PCB193"
  shape: bbox 0.29 x 0.29 x 0.29 mm, 1 faces (baked)
FEATURE [Part::Feature] Part__Feature223  label="PCB194"
  shape: bbox 0.29 x 0.29 x 0.29 mm, 1 faces (baked)
FEATURE [Part::Feature] Part__Feature224  label="PCB195"
  shape: bbox 0.29 x 0.29 x 0.29 mm, 1 faces (baked)
FEATURE [Part::Feature] Part__Feature225  label="PCB196"
  shape: bbox 0.29 x 0.29 x 0.29 mm, 1 faces (baked)
FEATURE [Part::Feature] Part__Feature226  label="PCB197"
  shape: bbox 0.29 x 0.29 x 0.29 mm, 1 faces (baked)
FEATURE [Part::Feature] Part__Feature227  label="PCB198"
  shape: bbox 0.29 x 0.29 x 0.29 mm, 1 faces (baked)
FEATURE [Part::Feature] Part__Feature228  label="PCB199"
  shape: bbox 0.29 x 0.29 x 0.29 mm, 1 faces (baked)
FEATURE [Part::Feature] Part__Feature229  label="PCB200"
  shape: bbox 0.29 x 0.29 x 0.29 mm, 1 faces (baked)
FEATURE [Part::Feature] Part__Feature230  label="PCB201"
  shape: bbox 0.29 x 0.29 x 0.29 mm, 1 faces (baked)
FEATURE [Part::Feature] Part__Feature231  label="PCB202"
  shape: bbox 0.29 x 0.29 x 0.29 mm, 1 faces (baked)
FEATURE [Part::Feature] Part__Feature232  label="PCB203"
  shape: bbox 0.29 x 0.29 x 0.29 mm, 1 faces (baked)
FEATURE [Part::Feature] Part__Feature233  label="PCB204"
  shape: bbox 0.29 x 0.29 x 0.29 mm, 1 faces (baked)
FEATURE [Part::Feature] Part__Feature234  label="PCB205"
  shape: bbox 0.29 x 0.29 x 0.29 mm, 1 faces (baked)
FEATURE [Part::Feature] Part__Feature235  label="PCB206"
  shape: bbox 0.29 x 0.29 x 0.29 mm, 1 faces (baked)
FEATURE [Part::Feature] Part__Feature236  label="PCB207"
  shape: bbox 0.29 x 0.29 x 0.29 mm, 1 faces (baked)
FEATURE [Part::Feature] Part__Feature237  label="PCB208"
  shape: bbox 0.29 x 0.29 x 0.29 mm, 1 faces (baked)
FEATURE [Part::Feature] Part__Feature238  label="PCB209"
  shape: bbox 0.29 x 0.29 x 0.29 mm, 1 faces (baked)
FEATURE [Part::Feature] Part__Feature239  label="PCB210"
  shape: bbox 0.29 x 0.29 x 0.29 mm, 1 faces (baked)
FEATURE [Part::Feature] Part__Feature240  label="PCB211"
  shape: bbox 0.29 x 0.29 x 0.29 mm, 1 faces (baked)
FEATURE [Part::Feature] Part__Feature241  label="PCB212"
  shape: bbox 0.29 x 0.29 x 0.29 mm, 1 faces (baked)
FEATURE [Part::Feature] Part__Feature242  label="PCB213"
  shape: bbox 0.29 x 0.29 x 0.29 mm, 1 faces (baked)
FEATURE [Part::Feature] Part__Feature243  label="PCB214"
  shape: bbox 0.29 x 0.29 x 0.29 mm, 1 faces (baked)
FEATURE [Part::Feature] Part__Feature244  label="PCB215"
  shape: bbox 0.29 x 0.29 x 0.29 mm, 1 faces (baked)
FEATURE [Part::Feature] Part__Feature245  label="PCB216"
  shape: bbox 0.29 x 0.29 x 0.29 mm, 1 faces (baked)
FEATURE [Part::Feature] Part__Feature246  label="PCB217"
  shape: bbox 0.29 x 0.29 x 0.29 mm, 1 faces (baked)
FEATURE [Part::Feature] Part__Feature247  label="PCB218"
  shape: bbox 0.29 x 0.29 x 0.29 mm, 1 faces (baked)
FEATURE [Part::Feature] Part__Feature248  label="PCB219"
  shape: bbox 0.29 x 0.29 x 0.29 mm, 1 faces (baked)
FEATURE [Part::Feature] Part__Feature249  label="PCB220"
  shape: bbox 0.29 x 0.29 x 0.29 mm, 1 faces (baked)
FEATURE [Part::Feature] Part__Feature250  label="PCB221"
  shape: bbox 0.29 x 0.29 x 0.29 mm, 1 faces (baked)
FEATURE [Part::Feature] Part__Feature251  label="PCB222"
  shape: bbox 0.29 x 0.29 x 0.29 mm, 1 faces (baked)
FEATURE [Part::Feature] Part__Feature252  label="PCB223"
  shape: bbox 0.29 x 0.29 x 0.29 mm, 1 faces (baked)
FEATURE [Part::Feature] Part__Feature253  label="PCB224"
  shape: bbox 0.29 x 0.29 x 0.29 mm, 1 faces (baked)
FEATURE [Part::Feature] Part__Feature254  label="PCB225"
  shape: bbox 0.29 x 0.29 x 0.29 mm, 1 faces (baked)
FEATURE [Part::Feature] Part__Feature255  label="PCB226"
  shape: bbox 0.29 x 0.29 x 0.29 mm, 1 faces (baked)
FEATURE [Part::Feature] Part__Feature256  label="PCB227"
  shape: bbox 5.207 x 2.54 x 2.54 mm, 69 faces (baked)
FEATURE [Part::Feature] Part__Feature257  label="PCB228"
  shape: bbox 3.429 x 0.889 x 10.92 mm, 38 faces (baked)
FEATURE [Part::Feature] Part__Feature258  label="PCB229"
  shape: bbox 5.159 x 2.599 x 8.38 mm, 6 faces (baked)
FEATURE [Part::Feature] Part__Feature259  label="PCB230"
  shape: bbox 5.08 x 10.16 x 2.54 mm, 174 faces (baked)
FEATURE [Part::Feature] Part__Feature260  label="PCB231"
  shape: bbox 3.429 x 8.509 x 10.92 mm, 150 faces (baked)
FEATURE [Part::Feature] Part__Feature261  label="PCB232"
  shape: bbox 5.09 x 10.16 x 8.38 mm, 6 faces (baked)
FEATURE [Part::Feature] Part__Feature262  label="PCB233"
  shape: bbox 2.54 x 5.207 x 2.54 mm, 69 faces (baked)
FEATURE [Part::Feature] Part__Feature263  label="PCB234"
  shape: bbox 0.889 x 3.429 x 18.54 mm, 38 faces (baked)
FEATURE [Part::Feature] Part__Feature264  label="PCB235"
  shape: bbox 2.599 x 5.159 x 8.38 mm, 6 faces (baked)
FEATURE [Part::Feature] Part__Feature265  label="PCB236"
  shape: bbox 5.08 x 6.35 x 5.715 mm, 90 faces (baked)
FEATURE [Part::Feature] Part__Feature266  label="PCB237"
  shape: bbox 1.676 x 5.486 x 4.293 mm, 91 faces (baked)
FEATURE [Part::Feature] Part__Feature267  label="PCB238"
  shape: bbox 5.842 x 5.486 x 2.017 mm, 71 faces (baked)
FEATURE [Part::Feature] Part__Feature268  label="PCB239"
  shape: bbox 4.8 x 12.6 x 6.6 mm, 6 faces (baked)
FEATURE [Part::Feature] Part__Feature269  label="PCB240"
  shape: bbox 2.413 x 15.75 x 8.509 mm, 54 faces (baked)
FEATURE [Part::Feature] Part__Feature270  label="PCB241"
  shape: bbox 1.219 x 13.74 x 11.02 mm, 48 faces (baked)
FEATURE [Part::Feature] Part__Feature271  label="PCB242"
  shape: bbox 2.41 x 15.75 x 8.51 mm, 6 faces (baked)
FEATURE [Part::Feature] Part__Feature272  label="PCB243"
  shape: bbox 2.413 x 20.83 x 8.509 mm, 70 faces (baked)
FEATURE [Part::Feature] Part__Feature273  label="PCB244"
  shape: bbox 1.219 x 18.82 x 11.02 mm, 62 faces (baked)
FEATURE [Part::Feature] Part__Feature274  label="PCB245"
  shape: bbox 2.41 x 20.83 x 8.51 mm, 6 faces (baked)
FEATURE [Part::Feature] Part__Feature275  label="PCB246"
  shape: bbox 5.08 x 48.26 x 2.54 mm, 894 faces (baked)
FEATURE [Part::Feature] Part__Feature276  label="PCB247"
  shape: bbox 3.429 x 46.61 x 18.54 mm, 690 faces (baked)
FEATURE [Part::Feature] Part__Feature277  label="PCB248"
  shape: bbox 5.09 x 48.26 x 8.38 mm, 6 faces (baked)
FEATURE [Part::Feature] Part__Feature278  label="PCB249"
  shape: bbox 5.08 x 48.26 x 2.54 mm, 894 faces (baked)
FEATURE [Part::Feature] Part__Feature279  label="PCB250"
  shape: bbox 3.429 x 46.61 x 18.54 mm, 690 faces (baked)
FEATURE [Part::Feature] Part__Feature280  label="PCB251"
  shape: bbox 5.09 x 48.26 x 8.38 mm, 6 faces (baked)
FEATURE [Part::Feature] Part__Feature281  label="PCB252"
  shape: bbox 2.413 x 20.83 x 8.509 mm, 70 faces (baked)
FEATURE [Part::Feature] Part__Feature282  label="PCB253"
  shape: bbox 1.219 x 18.82 x 11.02 mm, 62 faces (baked)
FEATURE [Part::Feature] Part__Feature283  label="PCB254"
  shape: bbox 2.41 x 20.83 x 8.51 mm, 6 faces (baked)
FEATURE [Part::Feature] Part__Feature284  label="PCB255"
  shape: bbox 2.413 x 25.91 x 8.509 mm, 86 faces (baked)
FEATURE [Part::Feature] Part__Feature285  label="PCB256"
  shape: bbox 1.219 x 23.9 x 11.02 mm, 76 faces (baked)
FEATURE [Part::Feature] Part__Feature286  label="PCB257"
  shape: bbox 2.41 x 25.91 x 8.51 mm, 6 faces (baked)
FEATURE [Part::Feature] Part__Feature287  label="PCB258"
  shape: bbox 2.54 x 5.207 x 2.54 mm, 69 faces (baked)
FEATURE [Part::Feature] Part__Feature288  label="PCB259"
  shape: bbox 0.889 x 3.429 x 18.54 mm, 38 faces (baked)
FEATURE [Part::Feature] Part__Feature289  label="PCB260"
  shape: bbox 2.599 x 5.159 x 8.38 mm, 6 faces (baked)
FEATURE [Part::Feature] Part__Feature290  label="PCB261"
  shape: bbox 10.29 x 2.54 x 2.54 mm, 137 faces (baked)
FEATURE [Part::Feature] Part__Feature291  label="PCB262"
  shape: bbox 8.509 x 0.889 x 10.92 mm, 70 faces (baked)
FEATURE [Part::Feature] Part__Feature292  label="PCB263"
  shape: bbox 10.37 x 2.75 x 8.38 mm, 6 faces (baked)
FEATURE [Part::Feature] Part__Feature293  label="PCB264"
  shape: bbox 0.8 x 0.4 x 0.2 mm, 11 faces, 0 solids (baked)
FEATURE [App::Part] PCB  label="PCB265"
  Group = -> [Part__Feature029,Part__Feature030,Part__Feature031,Part__Feature032,Part__Feature033,Part__Feature034,Part__Feature035,Part__Feature036,Part__Feature037,Part__Feature038,Part__Feature039,Part__Feature040,Part__Feature041,Part__Feature042,Part__Feature043,Part__Feature044,Part__Feature045,Part__Feature046,Part__Feature047,Part__Feature048,Part__Feature049,Part__Feature050,Part__Feature051,+242 more]
  Origin = -> Origin031
FEATURE [App::Part] MB1367_G474RE  label="MB1367-G474RE"
  Group = -> [PCB]
  Origin = -> Origin032
  Placement = pos=(91.4997,-126.12,10.65) rot=(0,0,1;0rad)
FEATURE [Part::Feature] Part__Feature301  label="User Library-XT30UPB-F-1"
  shape: bbox 10.2 x 11.4 x 5.2 mm, 256 faces (baked)
FEATURE [App::Part] AMASS_XT30UPB_F_1x02_P5_0mm_Vertical  label="AMASS_XT30UPB-F_1x02_P5.0mm_Vertical"
  Group = -> [Part__Feature301]
  Origin = -> Origin040
  Placement = pos=(102.03,-54.14,-0.05) rot=(0.57735,-0.57735,0.57735;4.18879rad)
FEATURE [Part::Feature] Part__Feature302  label="Molex_AE_6410_03A"
  shape: bbox 7.62 x 5.8 x 15.26 mm, 91 faces (baked)
FEATURE [App::Part] Molex_KK_254_AE_6410_03A_1x03_P2_54mm_Vertical  label="Molex_KK-254_AE-6410-03A_1x03_P2.54mm_Vertical"
  Group = -> [Part__Feature302]
  Origin = -> Origin041
  Placement = pos=(150.77,-90.55,-0.05) rot=(0.707107,-0.707107,0;3.14159rad)
FEATURE [Part::Feature] Part__Feature303  label="LED_1206_3216Metric"
  shape: bbox 3.2 x 1.6 x 1.1 mm, 50 faces (baked)
FEATURE [App::Part] LED_1206_3216Metric  label="LED_1206_3216Metric001"
  Group = -> [Part__Feature303]
  Origin = -> Origin042
  Placement = pos=(134.648,-96,-0.05) rot=(1,0,0;3.14159rad)
FEATURE [Part::Feature] Part__Feature304  label="C_Radial_D80mm_H115mm_P350mm"
  shape: bbox 10.31 x 10.92 x 13 mm, 32 faces (baked)
FEATURE [App::Part] C_Radial_D8_0mm_H11_5mm_P3_50mm  label="C_Radial_D8.0mm_H11.5mm_P3.50mm"
  Group = -> [Part__Feature304]
  Origin = -> Origin043
  Placement = pos=(119.01,-109.34,-0.05) rot=(0,1,0;3.14159rad)
FEATURE [Part::Feature] Part__Feature305  label="Molex_AE_6410_03A001"
  shape: bbox 7.62 x 5.8 x 15.26 mm, 91 faces (baked)
FEATURE [App::Part] Molex_KK_254_AE_6410_03A_1x03_P2_54mm_Vertical001  label="Molex_KK-254_AE-6410-03A_1x03_P2.54mm_Vertical001"
  Group = -> [Part__Feature305]
  Origin = -> Origin044
  Placement = pos=(102.485,-92.22,-0.05) rot=(1,0,0;3.14159rad)
FEATURE [Part::Feature] Part__Feature306  label="Molex_AE_6410_03A002"
  shape: bbox 7.62 x 5.8 x 15.26 mm, 91 faces (baked)
FEATURE [App::Part] Molex_KK_254_AE_6410_03A_1x03_P2_54mm_Vertical002  label="Molex_KK-254_AE-6410-03A_1x03_P2.54mm_Vertical002"
  Group = -> [Part__Feature306]
  Origin = -> Origin045
  Placement = pos=(104.33,-113.44,-0.05) rot=(0.707107,-0.707107,0;3.14159rad)
FEATURE [Part::Feature] Part__Feature307  label="Molex_AE_6410_03A003"
  shape: bbox 7.62 x 5.8 x 15.26 mm, 91 faces (baked)
FEATURE [App::Part] Molex_KK_254_AE_6410_03A_1x03_P2_54mm_Vertical003  label="Molex_KK-254_AE-6410-03A_1x03_P2.54mm_Vertical003"
  Group = -> [Part__Feature307]
  Origin = -> Origin046
  Placement = pos=(107.02,-104.86,-0.05) rot=(0.707107,0.707107,0;3.14159rad)
FEATURE [Part::Feature] Part__Feature308  label="Molex_AE_6410_04A"
  shape: bbox 10.16 x 5.8 x 15.26 mm, 117 faces (baked)
FEATURE [App::Part] Molex_KK_254_AE_6410_04A_1x04_P2_54mm_Vertical  label="Molex_KK-254_AE-6410-04A_1x04_P2.54mm_Vertical"
  Group = -> [Part__Feature308]
  Origin = -> Origin047
  Placement = pos=(120,-71.83,-0.05) rot=(0,1,0;3.14159rad)
FEATURE [Part::Feature] Part__Feature309  label="Molex_AE_6410_03A004"
  shape: bbox 7.62 x 5.8 x 15.26 mm, 91 faces (baked)
FEATURE [App::Part] Molex_KK_254_AE_6410_03A_1x03_P2_54mm_Vertical004  label="Molex_KK-254_AE-6410-03A_1x03_P2.54mm_Vertical004"
  Group = -> [Part__Feature309]
  Origin = -> Origin048
  Placement = pos=(137.75,-109.89,-0.05) rot=(0,1,0;3.14159rad)
FEATURE [Part::Feature] Part__Feature310  label="Molex_AE_6410_03A005"
  shape: bbox 7.62 x 5.8 x 15.26 mm, 91 faces (baked)
FEATURE [App::Part] Molex_KK_254_AE_6410_03A_1x03_P2_54mm_Vertical005  label="Molex_KK-254_AE-6410-03A_1x03_P2.54mm_Vertical005"
  Group = -> [Part__Feature310]
  Origin = -> Origin049
  Placement = pos=(117.57,-118.85,-0.05) rot=(0.707107,-0.707107,0;3.14159rad)
FEATURE [Part::Feature] Part__Feature311  label="Molex_AE_6410_03A006"
  shape: bbox 7.62 x 5.8 x 15.26 mm, 91 faces (baked)
FEATURE [App::Part] Molex_KK_254_AE_6410_03A_1x03_P2_54mm_Vertical006  label="Molex_KK-254_AE-6410-03A_1x03_P2.54mm_Vertical006"
  Group = -> [Part__Feature311]
  Origin = -> Origin050
  Placement = pos=(107.81,-123.82,-0.05) rot=(0.707107,-0.707107,0;3.14159rad)
FEATURE [Part::Feature] Part__Feature312  label="PinHeader_1x03_P254mm_Vertical"
  shape: bbox 2.54 x 7.62 x 11.54 mm, 76 faces (baked)
FEATURE [App::Part] PinHeader_1x03_P2_54mm_Vertical  label="PinHeader_1x03_P2.54mm_Vertical"
  Group = -> [Part__Feature312]
  Origin = -> Origin051
  Placement = pos=(117.713,-94.25,-0.05) rot=(0.707107,-0.707107,0;3.14159rad)
FEATURE [Part::Feature] Part__Feature313  label="Molex_AE_6410_04A001"
  shape: bbox 10.16 x 5.8 x 15.26 mm, 117 faces (baked)
FEATURE [App::Part] Molex_KK_254_AE_6410_04A_1x04_P2_54mm_Vertical001  label="Molex_KK-254_AE-6410-04A_1x04_P2.54mm_Vertical001"
  Group = -> [Part__Feature313]
  Origin = -> Origin052
  Placement = pos=(141.47,-120.98,-0.05) rot=(0.707107,-0.707107,0;3.14159rad)
FEATURE [Part::Feature] Part__Feature314  label="Converter_DCDC_TRACO_TSR_1_THT"
  shape: bbox 11.76 x 7.663 x 14.2 mm, 27 faces (baked)
FEATURE [App::Part] Converter_DCDC_TRACO_TSR_1_THT  label="Converter_DCDC_TRACO_TSR-1_THT"
  Group = -> [Part__Feature314]
  Origin = -> Origin053
  Placement = pos=(121.6,-57.92,-0.05) rot=(0.707107,-0.707107,0;3.14159rad)
FEATURE [Part::Feature] Part__Feature315  label="User Library-xt30upb-m"
  shape: bbox 10.2 x 9.4 x 5.2 mm, 493 faces (baked)
FEATURE [Part::Feature] Part__Feature316  label="User Library-xt30upb-m001"
  shape: bbox 2.575 x 10.42 x 4.013 mm, 75 faces (baked)
FEATURE [Part::Feature] Part__Feature317  label="User Library-xt30upb-m002"
  shape: bbox 2.575 x 10.42 x 4.013 mm, 75 faces (baked)
FEATURE [App::Part] User_Library_xt30upb_m  label="User Library-xt30upb-m003"
  Group = -> [Part__Feature315,Part__Feature316,Part__Feature317]
  Origin = -> Origin054
FEATURE [App::Part] AMASS_XT30UPB_M_1x02_P5_0mm_Vertical  label="AMASS_XT30UPB-M_1x02_P5.0mm_Vertical"
  Group = -> [User_Library_xt30upb_m]
  Origin = -> Origin055
  Placement = pos=(129.65,-48.34,-0.05) rot=(-1,0,0;1.5708rad)
FEATURE [Part::Feature] Part__Feature318  label="LED_1206_3216Metric002"
  shape: bbox 3.2 x 1.6 x 1.1 mm, 50 faces (baked)
FEATURE [App::Part] LED_1206_3216Metric001  label="LED_1206_3216Metric003"
  Group = -> [Part__Feature318]
  Origin = -> Origin056
  Placement = pos=(134.588,-92.09,-0.05) rot=(1,0,0;3.14159rad)
FEATURE [Part::Feature] Part__Feature319  label="Molex_AE_6410_03A007"
  shape: bbox 7.62 x 5.8 x 15.26 mm, 91 faces (baked)
FEATURE [App::Part] Molex_KK_254_AE_6410_03A_1x03_P2_54mm_Vertical007  label="Molex_KK-254_AE-6410-03A_1x03_P2.54mm_Vertical007"
  Group = -> [Part__Feature319]
  Origin = -> Origin057
  Placement = pos=(150.64,-113.41,-0.05) rot=(0.707107,0.707107,0;3.14159rad)
FEATURE [Part::Feature] Part__Feature320  label="Converter_DCDC_TRACO_TSR_1_THT001"
  shape: bbox 11.76 x 7.663 x 14.2 mm, 27 faces (baked)
FEATURE [App::Part] Converter_DCDC_TRACO_TSR_1_THT001  label="Converter_DCDC_TRACO_TSR-1_THT001"
  Group = -> [Part__Feature320]
  Origin = -> Origin058
  Placement = pos=(132.9,-57.85,-0.05) rot=(0.707107,-0.707107,0;3.14159rad)
FEATURE [Part::Feature] Part__Feature321  label="PinHeader_1x03_P254mm_Vertical001"
  shape: bbox 2.54 x 7.62 x 11.54 mm, 76 faces (baked)
FEATURE [App::Part] PinHeader_1x03_P2_54mm_Vertical001  label="PinHeader_1x03_P2.54mm_Vertical001"
  Group = -> [Part__Feature321]
  Origin = -> Origin059
  Placement = pos=(108.84,-60.275,-0.05) rot=(1,0,0;3.14159rad)
FEATURE [Part::Feature] Part__Feature322  label="C_Radial_D80mm_H115mm_P350mm001"
  shape: bbox 10.31 x 10.92 x 13 mm, 32 faces (baked)
FEATURE [App::Part] C_Radial_D8_0mm_H11_5mm_P3_50mm001  label="C_Radial_D8.0mm_H11.5mm_P3.50mm001"
  Group = -> [Part__Feature322]
  Origin = -> Origin060
  Placement = pos=(143.18,-58.86,-0.05) rot=(0.707107,0.707107,0;3.14159rad)
FEATURE [Part::Feature] Part__Feature323  label="Molex_AE_6410_06A"
  shape: bbox 15.24 x 5.8 x 15.26 mm, 169 faces (baked)
FEATURE [App::Part] Molex_KK_254_AE_6410_06A_1x06_P2_54mm_Vertical  label="Molex_KK-254_AE-6410-06A_1x06_P2.54mm_Vertical"
  Group = -> [Part__Feature323]
  Origin = -> Origin061
  Placement = pos=(132.87,-102.13,-0.05) rot=(1,0,0;3.14159rad)
FEATURE [Part::Feature] Part__Feature324  label="C_Radial_D80mm_H115mm_P350mm002"
  shape: bbox 10.31 x 10.92 x 13 mm, 32 faces (baked)
FEATURE [App::Part] C_Radial_D8_0mm_H11_5mm_P3_50mm002  label="C_Radial_D8.0mm_H11.5mm_P3.50mm002"
  Group = -> [Part__Feature324]
  Origin = -> Origin062
  Placement = pos=(112.48,-50.24,-0.05) rot=(0.707107,0.707107,0;3.14159rad)
FEATURE [Part::Feature] Part__Feature325  label="Molex_AE_6410_04A002"
  shape: bbox 10.16 x 5.8 x 15.26 mm, 117 faces (baked)
FEATURE [App::Part] Molex_KK_254_AE_6410_04A_1x04_P2_54mm_Vertical002  label="Molex_KK-254_AE-6410-04A_1x04_P2.54mm_Vertical002"
  Group = -> [Part__Feature325]
  Origin = -> Origin063
  Placement = pos=(131.95,-71.84,-0.05) rot=(1,0,0;3.14159rad)
FEATURE [Part::Feature] Part__Feature326  label="Molex_AE_6410_02A"
  shape: bbox 5.08 x 5.8 x 15.26 mm, 65 faces (baked)
FEATURE [App::Part] Molex_KK_254_AE_6410_02A_1x02_P2_54mm_Vertical  label="Molex_KK-254_AE-6410-02A_1x02_P2.54mm_Vertical"
  Group = -> [Part__Feature326]
  Origin = -> Origin064
  Placement = pos=(151.19,-79.07,-0.05) rot=(0,1,0;3.14159rad)
FEATURE [Part::Feature] Part__Feature327  label="Molex_AE_6410_04A003"
  shape: bbox 10.16 x 5.8 x 15.26 mm, 117 faces (baked)
FEATURE [App::Part] Molex_KK_254_AE_6410_04A_1x04_P2_54mm_Vertical003  label="Molex_KK-254_AE-6410-04A_1x04_P2.54mm_Vertical003"
  Group = -> [Part__Feature327]
  Origin = -> Origin065
  Placement = pos=(129.86,-120.98,-0.05) rot=(0.707107,-0.707107,0;3.14159rad)
FEATURE [Part::Feature] Part__Feature328  label="SOT_223"
  shape: bbox 7 x 6.5 x 1.7 mm, 78 faces (baked)
FEATURE [App::Part] SOT_223  label="SOT-223"
  Group = -> [Part__Feature328]
  Origin = -> Origin066
  Placement = pos=(101.38,-65.94,-0.05) rot=(1,0,0;3.14159rad)
FEATURE [Part::Feature] Part__Feature329  label="PinHeader_1x03_P254mm_Vertical002"
  shape: bbox 2.54 x 7.62 x 11.54 mm, 76 faces (baked)
FEATURE [App::Part] PinHeader_1x03_P2_54mm_Vertical002  label="PinHeader_1x03_P2.54mm_Vertical002"
  Group = -> [Part__Feature329]
  Origin = -> Origin067
  Placement = pos=(117.713,-103.13,-0.05) rot=(0.707107,-0.707107,0;3.14159rad)
FEATURE [Part::Feature] Part__Feature330  label="Molex_AE_6410_04A004"
  shape: bbox 10.16 x 5.8 x 15.26 mm, 117 faces (baked)
FEATURE [App::Part] Molex_KK_254_AE_6410_04A_1x04_P2_54mm_Vertical004  label="Molex_KK-254_AE-6410-04A_1x04_P2.54mm_Vertical004"
  Group = -> [Part__Feature330]
  Origin = -> Origin068
  Placement = pos=(119.87,-80.55,-0.05) rot=(0,1,0;3.14159rad)
FEATURE [Part::Feature] Part__Feature331  label="PinHeader_1x03_P254mm_Vertical003"
  shape: bbox 2.54 x 7.62 x 11.54 mm, 76 faces (baked)
FEATURE [App::Part] PinHeader_1x03_P2_54mm_Vertical003  label="PinHeader_1x03_P2.54mm_Vertical003"
  Group = -> [Part__Feature331]
  Origin = -> Origin069
  Placement = pos=(117.713,-98.74,-0.05) rot=(0.707107,-0.707107,0;3.14159rad)
FEATURE [Part::Feature] Part__Feature332  label="Molex_AE_6410_02A001"
  shape: bbox 5.08 x 5.8 x 15.26 mm, 65 faces (baked)
FEATURE [App::Part] Molex_KK_254_AE_6410_02A_1x02_P2_54mm_Vertical001  label="Molex_KK-254_AE-6410-02A_1x02_P2.54mm_Vertical001"
  Group = -> [Part__Feature332]
  Origin = -> Origin070
  Placement = pos=(157.46,-66.27,-0.05) rot=(0.707107,0.707107,0;3.14159rad)
FEATURE [Part::Feature] Part__Feature333  label="Molex_AE_6410_04A005"
  shape: bbox 10.16 x 5.8 x 15.26 mm, 117 faces (baked)
FEATURE [App::Part] Molex_KK_254_AE_6410_04A_1x04_P2_54mm_Vertical005  label="Molex_KK-254_AE-6410-04A_1x04_P2.54mm_Vertical005"
  Group = -> [Part__Feature333]
  Origin = -> Origin071
  Placement = pos=(131.9,-82.92,-0.05) rot=(1,0,0;3.14159rad)
FEATURE [Part::Feature] Part__Feature334  label="PinHeader_1x03_P254mm_Vertical004"
  shape: bbox 2.54 x 7.62 x 11.54 mm, 76 faces (baked)
FEATURE [App::Part] PinHeader_1x03_P2_54mm_Vertical004  label="PinHeader_1x03_P2.54mm_Vertical004"
  Group = -> [Part__Feature334]
  Origin = -> Origin072
  Placement = pos=(117.713,-89.67,-0.05) rot=(0.707107,-0.707107,0;3.14159rad)
FEATURE [Part::Feature] Part__Feature335  label="Molex_AE_6410_02A002"
  shape: bbox 5.08 x 5.8 x 15.26 mm, 65 faces (baked)
FEATURE [App::Part] Molex_KK_254_AE_6410_02A_1x02_P2_54mm_Vertical002  label="Molex_KK-254_AE-6410-02A_1x02_P2.54mm_Vertical002"
  Group = -> [Part__Feature335]
  Origin = -> Origin073
  Placement = pos=(148.2,-66.33,-0.05) rot=(0.707107,0.707107,0;3.14159rad)
FEATURE [Part::Feature] Part__Feature336  label="Molex_AE_6410_04A006"
  shape: bbox 10.16 x 5.8 x 15.26 mm, 117 faces (baked)
FEATURE [App::Part] Molex_KK_254_AE_6410_04A_1x04_P2_54mm_Vertical006  label="Molex_KK-254_AE-6410-04A_1x04_P2.54mm_Vertical006"
  Group = -> [Part__Feature336]
  Origin = -> Origin074
  Placement = pos=(149.95,-120.98,-0.05) rot=(0.707107,-0.707107,0;3.14159rad)
FEATURE [Part::Feature] Part__Feature337  label="_autosave-Electrobot-G474_PCB"
  shape: bbox 70.81 x 88.51 x 1.6 mm, 191 faces (baked)
FEATURE [App::Part] Electrobot_G474_1  label="Electrobot-G474 1"
  Group = -> [PinSocket_2x19_P2_54mm_Vertical,PinSocket_2x19_P2_54mm_Vertical001,MB1367_G474RE,AMASS_XT30UPB_F_1x02_P5_0mm_Vertical,Molex_KK_254_AE_6410_03A_1x03_P2_54mm_Vertical,LED_1206_3216Metric,C_Radial_D8_0mm_H11_5mm_P3_50mm,Molex_KK_254_AE_6410_03A_1x03_P2_54mm_Vertical001,Molex_KK_254_AE_6410_03A_1x03_P2_54mm_Vertical002,Molex_KK_254_AE_6410_03A_1x03_P2_54mm_Vertical003,+28 more]
  Origin = -> Origin075
  Placement = pos=(22.5,-126.5,135) rot=(-0.57735,-0.57735,-0.57735;4.18879rad)
FEATURE [Sketcher::SketchObject] Sketch010
  ArcFitTolerance = 1e-06
  AttachmentSupport = -> [Chamfer002]
  ExternalGeometry = -> [DatumLine]
  FullyConstrained = true
  MakeInternals = false
  MapMode = 5
  Placement = pos=(0,0,3) rot=(0,0,1;0rad)
  sketch-geometry (5):
    g0: LineSegment StartX=-29.5 StartY=-34.5 StartZ=0 EndX=-14.5 EndY=-34.5 EndZ=0
    g1: LineSegment StartX=-14.5 StartY=-34.5 StartZ=0 EndX=-14.5 EndY=34.5 EndZ=0
    g2: LineSegment StartX=-14.5 StartY=34.5 StartZ=0 EndX=-29.5 EndY=34.5 EndZ=0
    g3: LineSegment StartX=-29.5 StartY=34.5 StartZ=0 EndX=-29.5 EndY=-34.5 EndZ=0
    g4: GeomPoint [constr] X=-22 Y=0 Z=0
  constraints (13):
    c: Coincident(g0,g1)
    c: Coincident(g1,g2)
    c: Coincident(g2,g3)
    c: Coincident(g3,g0)
    c: Horizontal(g0)
    c: Horizontal(g2)
    c: Vertical(g1)
    c: Symmetric(g2,g0,g4)
    c: PointOnObject(g4,g-1)
    c: DistanceX(g2,g2) = 15
    c: Vertical(g3)
    c: PointOnObject(g4,g-3)
    c: DistanceY(g1,g1) = 69
FEATURE [PartDesign::Pocket] Pocket008
  BaseFeature = -> Chamfer002
  Direction = (0,0,-1)
  Length = 5
  Length2 = 5
  Profile = -> Sketch010
  ReferenceAxis = -> Sketch010 [N_Axis]
  Refine = true
  Suppressed = false
  Type = 1
FEATURE [Sketcher::SketchObject] Sketch011
  ArcFitTolerance = 1e-06
  AttachmentSupport = -> [XZ_Plane077]
  FullyConstrained = true
  MakeInternals = false
  MapMode = 5
  Placement = pos=(0,0,0) rot=(1,0,0;1.5708rad)
  sketch-geometry (1):
    g0: Circle CenterX=0 CenterY=0 CenterZ=0 NormalX=0 NormalY=0 NormalZ=1 AngleXU=0 Radius=27.5
  constraints (2):
    c: Coincident(g0,g-1)
    c: Diameter(g0) = 55
FEATURE [PartDesign::Pad] Pad002
  Direction = (0,-1,2e-16)
  Length = 10
  Length2 = 10
  Placement = pos=(0,0,0) rot=(1,0,0;1.5708rad)
  Profile = -> Sketch011
  ReferenceAxis = -> Sketch011 [N_Axis]
  Refine = true
  Suppressed = false
  Type = 0
FEATURE [PartDesign::Body] Body002  label="ROUE_EQ"
  AllowCompound = false
  Group = -> [Sketch011,Pad002]
  Origin = -> Origin077
  Placement = pos=(-22,-42,21) rot=(0,0,1;0rad)
  Tip = -> Pad002
FEATURE [Sketcher::SketchObject] Sketch012
  ArcFitTolerance = 1e-06
  AttachmentSupport = -> [Pocket008]
  FullyConstrained = true
  MakeInternals = false
  MapMode = 5
  Placement = pos=(0,0,45) rot=(0,0,1;0rad)
  sketch-geometry (5):
    g0: LineSegment StartX=33.75 StartY=-36 StartZ=0 EndX=33.75 EndY=36 EndZ=0
    g1: LineSegment StartX=33.75 StartY=36 StartZ=0 EndX=19.5 EndY=36 EndZ=0
    g2: LineSegment StartX=19.5 StartY=36 StartZ=0 EndX=19.5 EndY=-36 EndZ=0
    g3: LineSegment StartX=19.5 StartY=-36 StartZ=0 EndX=33.75 EndY=-36 EndZ=0
    g4: GeomPoint [constr] X=26.625 Y=0 Z=0
  constraints (13):
    c: Coincident(g0,g1)
    c: Coincident(g1,g2)
    c: Coincident(g2,g3)
    c: Coincident(g3,g0)
    c: Vertical(g0)
    c: Vertical(g2)
    c: Horizontal(g1)
    c: Horizontal(g3)
    c: Symmetric(g2,g0,g4)
    c: PointOnObject(g4,g-1)
    c: DistanceX(g1,g1) = 14.25
    c: DistanceY(g0,g0) = 72
    c: Distance(g0,g-2) = 33.75
FEATURE [PartDesign::Pocket] Pocket009
  BaseFeature = -> Pocket008
  Direction = (0,0,-1)
  Length = 0
  Length2 = 5
  Profile = -> Sketch012
  ReferenceAxis = -> Sketch012 [N_Axis]
  Refine = true
  Suppressed = false
  Type = 3
  UpToFace = -> Pocket008 [Face37]
FEATURE [PartDesign::SubShapeBinder] Binder
  BindCopyOnChange = 0
  BindMode = 0
  ClaimChildren = false
  Context = -> <external ../MODEL PART/support_batterie_parkside_12V.FCStd>#Part [Body005.Binder.]
  Fuse = false
  MakeFace = true
  OffsetFill = false
  OffsetIntersection = false
  OffsetJoinType = 0
  OffsetOpenResult = false
  PartialLoad = false
  Relative = true
  _Version = 2
FEATURE [Sketcher::SketchObject] Sketch016
  ArcFitTolerance = 1e-06
  AttachmentOffset = pos=(0,0,4) rot=(0,0,1;0rad)
  AttachmentSupport = -> [XY_Plane005]
  FullyConstrained = true
  MakeInternals = false
  MapMode = 5
  Placement = pos=(0,0,4) rot=(0,0,1;0rad)
  sketch-geometry (6):
    g0: LineSegment StartX=0 StartY=27.1999 StartZ=0 EndX=-10.45 EndY=27.1999 EndZ=0
    g1: ArcOfCircle CenterX=-10.45 CenterY=16.8999 CenterZ=0 NormalX=0 NormalY=0 NormalZ=1 AngleXU=0 Radius=10.3 StartAngle=1.5708 EndAngle=3.66519
    g2: LineSegment StartX=-19.3701 StartY=11.7499 StartZ=0 EndX=-8.92006 EndY=-6.35 EndZ=0
    g3: ArcOfCircle CenterX=1.3e-15 CenterY=-1.2 CenterZ=0 NormalX=0 NormalY=0 NormalZ=1 AngleXU=0 Radius=10.3 StartAngle=3.66519 EndAngle=4.71239
    g4: LineSegment StartX=-6e-16 StartY=-11.5 StartZ=0 EndX=0 EndY=27.1999 EndZ=0
    g5: LineSegment [constr] StartX=-6e-16 StartY=-11.5 StartZ=0 EndX=-8.92006 EndY=-11.5 EndZ=0
  constraints (16):
    c: PointOnObject(g0,g-2)
    c: Horizontal(g0)
    c: Tangent(g0,g1) = -1.5708
    c: Tangent(g1,g2) = -1.5708
    c: Tangent(g2,g3) = -1.5708
    c: PointOnObject(g3,g-2)
    c: Coincident(g3,g4)
    c: Coincident(g4,g0)
    c: Angle(g2,g-1) = 1.0472
    c: Equal(g1,g3)
    c: Radius(g1) = 10.3
    c: Horizontal(g5)
    c: Vertical(g5,g2)
    c: Tangent(g5,g3) = 1.5708
    c: Distance(g2,g2) = 20.9
    c: DistanceY(g3,g-1) = 11.5
FEATURE [Sketcher::SketchObject] Sketch017
  ArcFitTolerance = 1e-06
  AttachmentSupport = -> [XY_Plane005]
  ExternalGeometry = -> [Sketch016]
  FullyConstrained = true
  MakeInternals = false
  MapMode = 5
  sketch-geometry (10):
    g0: LineSegment StartX=0 StartY=30.1999 StartZ=0 EndX=-10.45 EndY=30.1999 EndZ=0
    g1: ArcOfCircle CenterX=-10.45 CenterY=16.8999 CenterZ=0 NormalX=0 NormalY=0 NormalZ=1 AngleXU=0 Radius=13.3 StartAngle=1.5708 EndAngle=3.14159
    g2: ArcOfCircle CenterX=1.3e-15 CenterY=-1.2 CenterZ=0 NormalX=0 NormalY=0 NormalZ=1 AngleXU=0 Radius=13.3 StartAngle=4.18879 EndAngle=4.71239
    g3: LineSegment StartX=0 StartY=30.1999 StartZ=0 EndX=-1.1e-15 EndY=-14.5 EndZ=0
    g4: LineSegment StartX=-23.75 StartY=16.8999 StartZ=0 EndX=-23.75 EndY=5.81481 EndZ=0
    g5: LineSegment StartX=-16.25 StartY=-7.17558 StartZ=0 EndX=-6.65 EndY=-12.7181 EndZ=0
    g6: ArcOfCircle CenterX=-8.75 CenterY=5.81481 CenterZ=0 NormalX=0 NormalY=0 NormalZ=1 AngleXU=0 Radius=15 StartAngle=3.14159 EndAngle=4.18879
    g7: GeomPoint [constr] X=-23.75 Y=-2.84545 Z=0
    g8: LineSegment [constr] StartX=-19.3701 StartY=11.7499 StartZ=0 EndX=-23.75 EndY=16.8999 EndZ=0
    g9: LineSegment [constr] StartX=-8.92006 StartY=-6.35 StartZ=0 EndX=-6.65 EndY=-12.7181 EndZ=0
  constraints (23):
    c: PointOnObject(g0,g-2)
    c: Horizontal(g0)
    c: Tangent(g0,g1) = -1.5708
    c: PointOnObject(g2,g-2)
    c: Coincident(g3,g0)
    c: Coincident(g3,g2)
    c: Coincident(g2,g-7)
    c: Coincident(g1,g-6)
    c: DistanceY(g-5,g0) = 3
    c: Tangent(g5,g2) = -1.5708
    c: Tangent(g4,g1) = -1.5708
    c: PointOnObject(g7,g4)
    c: PointOnObject(g7,g5)
    c: Tangent(g4,g6) = -1.5708
    c: Tangent(g5,g6) = -1.5708
    c: Equal(g5,g4)
    c: Coincident(g8,g-6)
    c: Coincident(g8,g1)
    c: Coincident(g9,g-7)
    c: Coincident(g9,g2)
    c: Equal(g9,g8)
    c: Vertical(g4)
    c: Radius(g6) = 15
FEATURE [PartDesign::Pad] Pad005
  Direction = (0,0,1)
  Length = 49.5
  Length2 = 1
  Profile = -> Sketch017
  ReferenceAxis = -> Sketch017 [N_Axis]
  Suppressed = false
  Type = 4
FEATURE [PartDesign::Pocket] Pocket011
  BaseFeature = -> Pad005
  Direction = (0,0,-1)
  Length = 5
  Length2 = 5
  Profile = -> Sketch016
  ReferenceAxis = -> Sketch016 [N_Axis]
  Reversed = true
  Suppressed = false
  Type = 1
FEATURE [PartDesign::Pocket] Pocket012
  BaseFeature = -> Pocket011
  Direction = (0,0,1)
  Length = 8
  Length2 = 5
  Profile = -> Binder
  Suppressed = false
  Type = 1
FEATURE [Sketcher::SketchObject] Sketch018
  ArcFitTolerance = 1e-06
  AttachmentOffset = pos=(0,0,1) rot=(0,0,1;0rad)
  AttachmentSupport = -> [XY_Plane005]
  FullyConstrained = true
  MakeInternals = false
  MapMode = 5
  Placement = pos=(0,0,-1) rot=(0,1,0;3.14159rad)
  sketch-geometry (11):
    g0: ArcOfCircle CenterX=12 CenterY=4 CenterZ=0 NormalX=0 NormalY=0 NormalZ=1 AngleXU=0 Radius=2.5 StartAngle=4.63328 EndAngle=7.06858
    g1: LineSegment StartX=11.8024 StartY=1.50782 StartZ=0 EndX=6.18535 EndY=1.95309 EndZ=0
    g2: LineSegment StartX=5 StartY=2 StartZ=0 EndX=0 EndY=2 EndZ=0
    g3: LineSegment StartX=13.7678 StartY=5.76777 StartZ=0 EndX=5.58287 EndY=13.9527 EndZ=0
    g4: LineSegment StartX=0 StartY=32 StartZ=0 EndX=0 EndY=2 EndZ=0
    g5: ArcOfCircle CenterX=5 CenterY=-13 CenterZ=0 NormalX=0 NormalY=0 NormalZ=1 AngleXU=0 Radius=15 StartAngle=1.49169 EndAngle=1.5708
    g6: GeomPoint [constr] X=5.5936 Y=2 Z=0
    g7: LineSegment StartX=0 StartY=32 StartZ=0 EndX=2 EndY=32 EndZ=0
    g8: LineSegment StartX=2 StartY=32 StartZ=0 EndX=2.67074 EndY=20.4443 EndZ=0
    g9: ArcOfCircle CenterX=12.6539 CenterY=21.0237 CenterZ=0 NormalX=0 NormalY=0 NormalZ=1 AngleXU=0 Radius=10 StartAngle=3.19957 EndAngle=3.92699
    g10: GeomPoint [constr] X=2.89131 Y=16.6442 Z=0
  constraints (28):
    c: PointOnObject(g2,g-2)
    c: Horizontal(g2)
    c: Coincident(g4,g2)
    c: Tangent(g3,g0) = -1.5708
    c: PointOnObject(g6,g2)
    c: PointOnObject(g6,g1)
    c: Tangent(g2,g5) = -1.5708
    c: Tangent(g1,g5) = -1.5708
    c: DistanceY(g-1,g0) = 4
    c: DistanceX(g-1,g0) = 12
    c: Radius(g0) = 2.5
    c: Tangent(g1,g0) = 1.5708
    c: PointOnObject(g4,g-2)
    c: Coincident(g7,g4)
    c: Horizontal(g7)
    c: Coincident(g8,g7)
    c: PointOnObject(g10,g8)
    c: PointOnObject(g10,g3)
    c: Tangent(g8,g9) = -1.5708
    c: Tangent(g3,g9) = 1.5708
    c: DistanceY(g4,g4) = 30
    c: DistanceY(g-1,g2) = 2
    c: DistanceX(g7,g7) = 2
    c: Angle(g3,g-1) = 0.785398
    c: Radius(g9) = 10
    c: Equal(g3,g8)
    c: Radius(g5) = 15
    c: DistanceX(g2,g2) = 5
FEATURE [PartDesign::Pocket] Pocket013
  BaseFeature = -> Pocket012
  Direction = (0,0,1)
  Length = 5
  Length2 = 5
  Offset = 2
  Profile = -> Sketch018
  ReferenceAxis = -> Sketch018 [N_Axis]
  Suppressed = false
  Type = 2
FEATURE [PartDesign::Pocket] Pocket014
  BaseFeature = -> Pocket013
  Direction = (0,0,1)
  Length = 5
  Length2 = 5
  Profile = -> Pocket013 [Face29]
  Suppressed = false
  Type = 0
FEATURE [Sketcher::SketchObject] Sketch019
  ArcFitTolerance = 1e-06
  AttachmentSupport = -> [Pocket014]
  FullyConstrained = true
  MakeInternals = false
  MapMode = 5
  Placement = pos=(0,0,49.5) rot=(0,0,1;0rad)
  sketch-geometry (5):
    g0: LineSegment StartX=-18.9701 StartY=11.0571 StartZ=0 EndX=-21.1351 EndY=9.80711 EndZ=0
    g1: ArcOfCircle CenterX=-16.6525 CenterY=8.33999 CenterZ=0 NormalX=0 NormalY=0 NormalZ=1 AngleXU=0 Radius=11 StartAngle=4.60788 EndAngle=5.03941
    g2: LineSegment StartX=-13.1191 StartY=-2.07705 StartZ=0 EndX=-11.8201 EndY=-1.32705 EndZ=0
    g3: LineSegment StartX=-11.8201 StartY=-1.32705 StartZ=0 EndX=-18.9701 EndY=11.0571 EndZ=0
    g4: ArcOfCircle CenterX=7.84255 CenterY=10.9447 CenterZ=0 NormalX=0 NormalY=0 NormalZ=1 AngleXU=0 Radius=29 StartAngle=3.18083 EndAngle=3.62755
  constraints (17):
    c: Coincident(g1,g2)
    c: Coincident(g2,g3)
    c: Coincident(g3,g0)
    c: PointOnObject(g0,g-3)
    c: Perpendicular(g-3,g0)
    c: Distance(g0,g0) = 2.5
    c: Distance(g3,g3) = 14.3
    c: Distance(g2,g-3) = 5.8
    c: Perpendicular(g3,g2)
    c: PointOnObject(g2,g-3)
    c: Distance(g2,g2) = 1.5
    c: Coincident(g4,g0)
    c: Coincident(g4,g1)
    c: DistanceX(g1,g-1) = 17.8
    c: DistanceY(g1,g-1) = 2.6
    c: Radius(g4) = 29
    c: Radius(g1) = 11
FEATURE [PartDesign::Pocket] Pocket015
  BaseFeature = -> Pocket014
  Direction = (0,0,-1)
  Length = 7.5
  Length2 = 5
  Profile = -> Sketch019
  ReferenceAxis = -> Sketch019 [N_Axis]
  Suppressed = false
  Type = 0
FEATURE [Sketcher::SketchObject] Sketch020
  ArcFitTolerance = 1e-06
  AttachmentSupport = -> [Pocket015]
  ExternalGeometry = -> [Pocket015]
  FullyConstrained = true
  MakeInternals = false
  MapMode = 5
  Placement = pos=(0,0,49.5) rot=(0,0,1;0rad)
  sketch-geometry (4):
    g0: LineSegment StartX=-13.4289 StartY=-2.14045 StartZ=0 EndX=-11.6789 EndY=-5.17154 EndZ=0
    g1: LineSegment StartX=-11.6789 StartY=-5.17154 StartZ=0 EndX=-10.1201 EndY=-4.27154 EndZ=0
    g2: LineSegment StartX=-10.1201 StartY=-4.27154 StartZ=0 EndX=-11.8701 EndY=-1.24045 EndZ=0
    g3: LineSegment StartX=-11.8701 StartY=-1.24045 StartZ=0 EndX=-13.4289 EndY=-2.14045 EndZ=0
  constraints (12):
    c: Coincident(g0,g1)
    c: Coincident(g1,g2)
    c: Coincident(g2,g3)
    c: Coincident(g3,g0)
    c: Parallel(g0,g2)
    c: Parallel(g1,g3)
    c: Perpendicular(g0,g1)
    c: Distance(g3,g3) = 1.8
    c: Distance(g2,g2) = 3.5
    c: PointOnObject(g2,g-3)
    c: Distance(g-3,g2) = 0.1
    c: PointOnObject(g1,g-3)
FEATURE [PartDesign::Pocket] Pocket016
  BaseFeature = -> Pocket015
  Direction = (0,0,-1)
  Length = 45.5
  Length2 = 5
  Profile = -> Sketch020
  ReferenceAxis = -> Sketch020 [N_Axis]
  Suppressed = false
  Type = 0
FEATURE [Sketcher::SketchObject] Sketch021
  ArcFitTolerance = 1e-06
  AttachmentSupport = -> [Pocket016]
  ExternalGeometry = -> [Pocket016]
  FullyConstrained = true
  MakeInternals = false
  MapMode = 5
  Placement = pos=(0,0,42) rot=(0,0,1;0rad)
  sketch-geometry (4):
    g0: LineSegment StartX=-21.1351 StartY=9.80711 StartZ=0 EndX=-22.5351 EndY=9.80711 EndZ=0
    g1: LineSegment StartX=-22.5351 StartY=9.80711 StartZ=0 EndX=-19.9 EndY=-2.6 EndZ=0
    g2: LineSegment StartX=-19.9 StartY=-2.6 StartZ=0 EndX=-17.8 EndY=-2.6 EndZ=0
    g3: LineSegment StartX=-21.1351 StartY=9.80711 StartZ=0 EndX=-17.8 EndY=-2.6 EndZ=0
  constraints (10):
    c: Horizontal(g0)
    c: Coincident(g1,g0)
    c: Coincident(g2,g1)
    c: Horizontal(g2)
    c: DistanceX(g0,g0) = 1.4
    c: DistanceX(g2,g2) = 2.1
    c: Coincident(g3,g0)
    c: Coincident(g3,g2)
    c: Coincident(g2,g-3)
    c: Coincident(g0,g-3)
FEATURE [PartDesign::Pocket] Pocket017
  BaseFeature = -> Pocket016
  Direction = (0,0,-1)
  Length = 5.3
  Length2 = 5
  Profile = -> Sketch021
  ReferenceAxis = -> Sketch021 [N_Axis]
  Reversed = true
  Suppressed = false
  Type = 0
FEATURE [Sketcher::SketchObject] Sketch023
  ArcFitTolerance = 1e-06
  AttachmentSupport = -> [Pocket017]
  FullyConstrained = true
  MakeInternals = false
  MapMode = 5
  Placement = pos=(0,0,-1) rot=(1,0,0;3.14159rad)
  sketch-geometry (1):
    g0: Circle CenterX=-15 CenterY=-18 CenterZ=0 NormalX=0 NormalY=0 NormalZ=1 AngleXU=0 Radius=2.1
  constraints (3):
    c: Diameter(g0) = 4.2
    c: Distance(g0,g-2) = 15
    c: DistanceY(g0,g-1) = 18
FEATURE [PartDesign::Pocket] Pocket019
  BaseFeature = -> Pocket017
  Direction = (0,0,1)
  Length = 2
  Length2 = 5
  Profile = -> Sketch023
  ReferenceAxis = -> Sketch023 [N_Axis]
  Suppressed = false
  Type = 0
FEATURE [Sketcher::SketchObject] Sketch024
  ArcFitTolerance = 1e-06
  AttachmentSupport = -> [Pocket019]
  ExternalGeometry = -> [Pocket019]
  FullyConstrained = true
  MakeInternals = false
  MapMode = 5
  Placement = pos=(0,0,1) rot=(1,0,0;3.14159rad)
  sketch-geometry (1):
    g0: Circle CenterX=-15 CenterY=-18 CenterZ=0 NormalX=0 NormalY=0 NormalZ=1 AngleXU=0 Radius=1.85
  constraints (2):
    c: Diameter(g0) = 3.7
    c: Coincident(g0,g-3)
FEATURE [PartDesign::Pocket] Pocket020
  BaseFeature = -> Pocket019
  Direction = (0,0,1)
  Length = 5
  Length2 = 5
  Profile = -> Sketch024
  ReferenceAxis = -> Sketch024 [N_Axis]
  Suppressed = false
  Type = 0
FEATURE [PartDesign::Pad] Pad006
  BaseFeature = -> Pocket020
  Direction = (0,1,0)
  Length = 2
  Length2 = 10
  Profile = -> Pocket020 [Face1]
  Suppressed = false
  Type = 0
FEATURE [PartDesign::Chamfer] Chamfer004
  Angle = 45
  Base = -> Pad006 [Edge57]
  BaseFeature = -> Pad006
  ChamferType = 1
  FlipDirection = false
  Size = 1
  Size2 = 1.99
  SupportTransform = false
  Suppressed = false
  UseAllEdges = false
FEATURE [Sketcher::SketchObject] Sketch025
  ArcFitTolerance = 1e-06
  AttachmentSupport = -> [Chamfer004]
  FullyConstrained = true
  MakeInternals = false
  MapMode = 5
  Placement = pos=(0,32.1999,0) rot=(0,0.707107,0.707107;3.14159rad)
  sketch-geometry (1):
    g0: Circle CenterX=7 CenterY=10 CenterZ=0 NormalX=0 NormalY=0 NormalZ=1 AngleXU=0 Radius=2.2
  constraints (3):
    c: Diameter(g0) = 4.4
    c: DistanceY(g-1,g0) = 10
    c: DistanceX(g-1,g0) = 7
FEATURE [PartDesign::Pocket] Pocket021
  BaseFeature = -> Chamfer004
  Direction = (0,-1,2e-16)
  Length = 2
  Length2 = 5
  Profile = -> Sketch025
  ReferenceAxis = -> Sketch025 [N_Axis]
  Suppressed = false
  Type = 0
FEATURE [Sketcher::SketchObject] Sketch026
  ArcFitTolerance = 1e-06
  AttachmentSupport = -> [Pocket021]
  ExternalGeometry = -> [Sketch025]
  FullyConstrained = true
  MakeInternals = false
  MapMode = 5
  Placement = pos=(0,32.1999,0) rot=(0,0.707107,0.707107;3.14159rad)
  sketch-geometry (1):
    g0: Circle CenterX=7 CenterY=10 CenterZ=0 NormalX=0 NormalY=0 NormalZ=1 AngleXU=0 Radius=1.85
  constraints (2):
    c: Diameter(g0) = 3.7
    c: Coincident(g0,g-3)
FEATURE [PartDesign::Pocket] Pocket022
  BaseFeature = -> Pocket021
  Direction = (0,-1,2e-16)
  Length = 5
  Length2 = 5
  Profile = -> Sketch026
  ReferenceAxis = -> Sketch026 [N_Axis]
  Suppressed = false
  Type = 0
FEATURE [PartDesign::LinearPattern] LinearPattern
  BaseFeature = -> Pocket022
  Direction = -> Sketch025 [V_Axis]
  Length = 35
  Mode = 0
  Occurrences = 3
  Offset = 17.5
  Originals = -> [Pocket021,Pocket022]
  Suppressed = false
  TransformMode = 0
FEATURE [Sketcher::SketchObject] Sketch027
  ArcFitTolerance = 1e-06
  AttachmentOffset = pos=(0,0,0) rot=(0,1,0;0.523599rad)
  AttachmentSupport = -> [XZ_Plane005]
  ExternalGeometry = -> [LinearPattern]
  FullyConstrained = true
  MakeInternals = false
  MapMode = 5
  Placement = pos=(0,0,0) rot=(0.935113,0.250563,0.250563;1.63783rad)
  sketch-geometry (3):
    g0: LineSegment StartX=-19.6703 StartY=45 StartZ=0 EndX=-19.6703 EndY=-1 EndZ=0
    g1: LineSegment StartX=-19.6703 StartY=45 StartZ=0 EndX=-14.6703 EndY=-1 EndZ=0
    g2: LineSegment StartX=-19.6703 StartY=-1 StartZ=0 EndX=-14.6703 EndY=-1 EndZ=0
  constraints (9):
    c: Coincident(g1,g0)
    c: Coincident(g2,g0)
    c: Coincident(g2,g1)
    c: Horizontal(g2)
    c: DistanceX(g2,g2) = 5
    c: DistanceY(g-1,g0) = 45
    c: Vertical(g-3,g0)
    c: Vertical(g0)
    c: DistanceY(g0,g-1) = 1
FEATURE [PartDesign::Pocket] Pocket023
  BaseFeature = -> LinearPattern
  Direction = (-0.5,0.866025,-1e-16)
  Length = 5
  Length2 = 5
  Midplane = true
  Profile = -> Sketch027
  ReferenceAxis = -> Sketch027 [N_Axis]
  Suppressed = false
  Type = 1
FEATURE [PartDesign::Mirrored] Mirrored001
  BaseFeature = -> Pocket023
  MirrorPlane = -> Sketch021 [V_Axis]
  Originals = -> [Pocket017]
  Refine = true
  Suppressed = false
  TransformMode = 1
FEATURE [Sketcher::SketchObject] Sketch022
  ArcFitTolerance = 1e-06
  AttachmentSupport = -> [Mirrored001]
  FullyConstrained = true
  MakeInternals = false
  MapMode = 5
  Placement = pos=(0,0,-1) rot=(1,0,0;3.14159rad)
  sketch-geometry (16):
    g0: LineSegment StartX=-12 StartY=-15 StartZ=0 EndX=-12 EndY=-14 EndZ=0
    g1: LineSegment StartX=-12 StartY=-14 StartZ=0 EndX=-8 EndY=-14 EndZ=0
    g2: LineSegment StartX=-8 StartY=-14 StartZ=0 EndX=-8 EndY=-15 EndZ=0
    g3: LineSegment StartX=-8 StartY=-15 StartZ=0 EndX=-12 EndY=-15 EndZ=0
    g4: LineSegment StartX=9.5 StartY=-13.5 StartZ=0 EndX=9.5 EndY=-15 EndZ=0
    g5: LineSegment StartX=9.5 StartY=-17.5 StartZ=0 EndX=10.5 EndY=-17.5 EndZ=0
    g6: LineSegment StartX=10.5 StartY=-17.5 StartZ=0 EndX=10.5 EndY=-16 EndZ=0
    g7: LineSegment StartX=10.5 StartY=-13.5 StartZ=0 EndX=9.5 EndY=-13.5 EndZ=0
    g8: LineSegment StartX=8 StartY=-15 StartZ=0 EndX=8 EndY=-16 EndZ=0
    g9: LineSegment StartX=8 StartY=-16 StartZ=0 EndX=9.5 EndY=-16 EndZ=0
    g10: LineSegment StartX=12 StartY=-16 StartZ=0 EndX=12 EndY=-15 EndZ=0
    g11: LineSegment StartX=12 StartY=-15 StartZ=0 EndX=10.5 EndY=-15 EndZ=0
    g12: LineSegment StartX=10.5 StartY=-15 StartZ=0 EndX=10.5 EndY=-13.5 EndZ=0
    g13: LineSegment StartX=9.5 StartY=-16 StartZ=0 EndX=9.5 EndY=-17.5 EndZ=0
    g14: LineSegment StartX=9.5 StartY=-15 StartZ=0 EndX=8 EndY=-15 EndZ=0
    g15: LineSegment StartX=10.5 StartY=-16 StartZ=0 EndX=12 EndY=-16 EndZ=0
  constraints (49):
    c: Coincident(g0,g1)
    c: Coincident(g1,g2)
    c: Coincident(g2,g3)
    c: Coincident(g3,g0)
    c: Vertical(g0)
    c: Vertical(g2)
    c: Horizontal(g1)
    c: Horizontal(g3)
    c: Coincident(g13,g5)
    c: Coincident(g5,g6)
    c: Coincident(g12,g7)
    c: Coincident(g7,g4)
    c: Vertical(g4)
    c: Vertical(g6)
    c: Horizontal(g5)
    c: Horizontal(g7)
    c: Coincident(g8,g9)
    c: Coincident(g15,g10)
    c: Coincident(g10,g11)
    c: Coincident(g14,g8)
    c: Vertical(g8)
    c: Vertical(g10)
    c: Horizontal(g9)
    c: Horizontal(g11)
    c: PointOnObject(g6,g15)
    c: PointOnObject(g4,g14)
    c: Coincident(g11,g12)
    c: PointOnObject(g14,g4)
    c: Coincident(g9,g13)
    c: PointOnObject(g15,g6)
    c: Equal(g11,g12)
    c: Equal(g12,g4)
    c: Equal(g4,g14)
    c: Equal(g14,g9)
    c: Equal(g9,g13)
    c: Equal(g13,g6)
    c: Equal(g6,g15)
    c: Equal(g7,g8)
    c: Equal(g8,g10)
    c: Equal(g10,g5)
    c: Equal(g5,g0)
    c: Vertical(g13)
    c: Horizontal(g15)
    c: DistanceX(g8,g10) = 4
    c: DistanceY(g10,g10) = 1
    c: DistanceX(g3,g3) = 4
    c: Symmetric(g10,g0,g-2)
    c: DistanceY(g0,g-1) = 15
    c: DistanceX(g1,g-1) = 8
FEATURE [PartDesign::Pocket] Pocket018
  BaseFeature = -> Mirrored001
  Direction = (0,0,1)
  Length = 1
  Length2 = 5
  Profile = -> Sketch022
  ReferenceAxis = -> Sketch022 [N_Axis]
  Suppressed = false
  Type = 0
FEATURE [PartDesign::Fillet] Fillet002
  Base = -> Pocket018 [Edge90,Edge81,Edge76,Edge87]
  BaseFeature = -> Pocket018
  Radius = 1
  SupportTransform = false
  Suppressed = false
  UseAllEdges = false
FEATURE [Mesh::Feature] ACCUMULATOR_Bottom_Cover
FEATURE [Mesh::Feature] ACCUMULATOR_Bottom_Plate
FEATURE [Mesh::Feature] ACCUMULATOR_Top_Cover
FEATURE [Mesh::Feature] ACCUMULATOR_Top_Plate
FEATURE [App::Part] Part003  label="Batterie"
  Group = -> [ACCUMULATOR_Bottom_Cover,ACCUMULATOR_Bottom_Plate,ACCUMULATOR_Top_Cover,ACCUMULATOR_Top_Plate]
  Origin = -> Origin008
  Placement = pos=(-32.5,-6.2e-15,130) rot=(-1,0,0;3.14159rad)
FEATURE [PartDesign::ShapeBinder] CopyPocket009
  TraceSupport = false
FEATURE [Sketcher::SketchObject] Sketch028
  ArcFitTolerance = 1e-06
  AttachmentSupport = -> [CopyPocket009]
  FullyConstrained = true
  MakeInternals = false
  MapMode = 5
  Placement = pos=(0,0,45) rot=(0,0,1;0rad)
  sketch-geometry (5):
    g0: LineSegment StartX=-1 StartY=-37.5 StartZ=0 EndX=47.5 EndY=-37.5 EndZ=0
    g1: LineSegment StartX=47.5 StartY=-37.5 StartZ=0 EndX=47.5 EndY=37.5 EndZ=0
    g2: LineSegment StartX=47.5 StartY=37.5 StartZ=0 EndX=-1 EndY=37.5 EndZ=0
    g3: LineSegment StartX=-1 StartY=37.5 StartZ=0 EndX=-1 EndY=-37.5 EndZ=0
    g4: GeomPoint [constr] X=23.25 Y=0 Z=0
  constraints (13):
    c: Coincident(g0,g1)
    c: Coincident(g1,g2)
    c: Coincident(g2,g3)
    c: Coincident(g3,g0)
    c: Horizontal(g0)
    c: Horizontal(g2)
    c: Vertical(g1)
    c: Vertical(g3)
    c: Symmetric(g2,g0,g4)
    c: PointOnObject(g4,g-1)
    c: DistanceY(g1,g1) = 75
    c: Distance(g-2,g1) = 47.5
    c: Distance(g-2,g3) = 1
FEATURE [PartDesign::Pad] Pad007
  Direction = (0,0,1)
  Length = 50.5
  Length2 = 10
  Profile = -> Sketch028
  ReferenceAxis = -> Sketch028 [N_Axis]
  Refine = true
  Suppressed = false
  Type = 0
FEATURE [PartDesign::Fillet] Fillet003
  Base = -> Pad007 [Edge2,Edge1,Edge8,Edge5]
  BaseFeature = -> Pad007
  Radius = 5
  Refine = true
  SupportTransform = false
  Suppressed = false
  UseAllEdges = false
FEATURE [PartDesign::Thickness] Thickness001
  Base = -> Fillet003 [Face2]
  BaseFeature = -> Fillet003
  Intersection = false
  Join = 0
  Mode = 0
  Refine = true
  Reversed = true
  SupportTransform = false
  Suppressed = false
  Value = 3
FEATURE [Sketcher::SketchObject] Sketch029
  ArcFitTolerance = 1e-06
  AttachmentSupport = -> [Thickness001]
  FullyConstrained = true
  MakeInternals = false
  MapMode = 5
  Placement = pos=(0,0,95.5) rot=(0,0,1;0rad)
  sketch-geometry (5):
    g0: LineSegment StartX=31.5 StartY=-6 StartZ=0 EndX=37.5 EndY=-6 EndZ=0
    g1: LineSegment StartX=37.5 StartY=-6 StartZ=0 EndX=37.5 EndY=6 EndZ=0
    g2: LineSegment StartX=37.5 StartY=6 StartZ=0 EndX=31.5 EndY=6 EndZ=0
    g3: LineSegment StartX=31.5 StartY=6 StartZ=0 EndX=31.5 EndY=-6 EndZ=0
    g4: GeomPoint [constr] X=34.5 Y=-1e-16 Z=0
  constraints (13):
    c: Coincident(g0,g1)
    c: Coincident(g1,g2)
    c: Coincident(g2,g3)
    c: Coincident(g3,g0)
    c: Horizontal(g0)
    c: Horizontal(g2)
    c: Vertical(g1)
    c: Vertical(g3)
    c: Symmetric(g2,g0,g4)
    c: PointOnObject(g4,g-1)
    c: DistanceX(g-1,g4) = 34.5
    c: DistanceX(g2,g2) = 6
    c: DistanceY(g1,g1) = 12
FEATURE [PartDesign::Pocket] Pocket024
  BaseFeature = -> Thickness001
  Direction = (0,0,-1)
  Length = 5
  Length2 = 5
  Profile = -> Sketch029
  ReferenceAxis = -> Sketch029 [N_Axis]
  Refine = true
  Suppressed = false
  Type = 1
FEATURE [PartDesign::Fillet] Fillet004
  Base = -> Pocket024 [Edge55,Edge58,Edge53,Edge56]
  BaseFeature = -> Pocket024
  Radius = 1
  Refine = true
  SupportTransform = false
  Suppressed = false
  UseAllEdges = false
FEATURE [PartDesign::Chamfer] Chamfer005
  Angle = 45
  Base = -> Fillet004 [Edge4]
  BaseFeature = -> Fillet004
  ChamferType = 0
  FlipDirection = false
  Refine = true
  Size = 1.5
  Size2 = 1
  SupportTransform = false
  Suppressed = false
  UseAllEdges = false
FEATURE [Sketcher::SketchObject] Sketch030
  ArcFitTolerance = 1e-06
  AttachmentSupport = -> [Chamfer005]
  FullyConstrained = true
  MakeInternals = false
  MapMode = 5
  Placement = pos=(0,0,45) rot=(1,0,0;3.14159rad)
  sketch-geometry (5):
    g0: LineSegment StartX=33.75 StartY=-36 StartZ=0 EndX=33.75 EndY=36 EndZ=0
    g1: LineSegment StartX=33.75 StartY=36 StartZ=0 EndX=19.5 EndY=36 EndZ=0
    g2: LineSegment StartX=19.5 StartY=36 StartZ=0 EndX=19.5 EndY=-36 EndZ=0
    g3: LineSegment StartX=19.5 StartY=-36 StartZ=0 EndX=33.75 EndY=-36 EndZ=0
    g4: GeomPoint [constr] X=26.625 Y=0 Z=0
  constraints (13):
    c: Coincident(g0,g1)
    c: Coincident(g1,g2)
    c: Coincident(g2,g3)
    c: Coincident(g3,g0)
    c: Vertical(g0)
    c: Vertical(g2)
    c: Horizontal(g1)
    c: Horizontal(g3)
    c: Symmetric(g2,g0,g4)
    c: PointOnObject(g4,g-1)
    c: DistanceX(g1,g1) = 14.25
    c: DistanceY(g0,g0) = 72
    c: Distance(g-2,g0) = 33.75
FEATURE [PartDesign::Pocket] Pocket025
  BaseFeature = -> Chamfer005
  Direction = (0,0,1)
  Length = 0
  Length2 = 5
  Profile = -> Sketch030
  ReferenceAxis = -> Sketch030 [N_Axis]
  Refine = true
  Suppressed = false
  Type = 3
  UpToFace = -> Chamfer005 [Face27]
FEATURE [Sketcher::SketchObject] Sketch034
  ArcFitTolerance = 1e-06
  AttachmentSupport = -> [XZ_Plane079]
  FullyConstrained = true
  MakeInternals = false
  MapMode = 5
  Placement = pos=(0,0,0) rot=(1,0,0;1.5708rad)
  sketch-geometry (1):
    g0: Circle CenterX=-22 CenterY=21 CenterZ=0 NormalX=0 NormalY=0 NormalZ=1 AngleXU=0 Radius=21
  constraints (3):
    c: DistanceX(g0,g-1) = 22
    c: DistanceY(g-1,g0) = 21
    c: Diameter(g0) = 42
FEATURE [PartDesign::Pad] Pad009
  Direction = (0,-1,2e-16)
  Length = 68
  Length2 = 10
  Midplane = true
  Placement = pos=(0,0,0) rot=(1,0,0;1.5708rad)
  Profile = -> Sketch034
  ReferenceAxis = -> Sketch034 [N_Axis]
  Refine = true
  Suppressed = false
  Type = 0
FEATURE [PartDesign::Body] Body007  label="MOTEUR_EQ"
  AllowCompound = false
  Group = -> [Sketch034,Pad009]
  Origin = -> Origin079
  Tip = -> Pad009
FEATURE [PartDesign::ShapeBinder] CopyMirrored
  TraceSupport = false
FEATURE [Sketcher::SketchObject] Sketch035
  ArcFitTolerance = 1e-06
  AttachmentSupport = -> [CopyMirrored]
  FullyConstrained = true
  MakeInternals = false
  MapMode = 5
  Placement = pos=(0,0,45) rot=(1,0,0;3.14159rad)
  sketch-geometry (5):
    g0: LineSegment StartX=2 StartY=-34 StartZ=0 EndX=2 EndY=34 EndZ=0
    g1: LineSegment StartX=2 StartY=34 StartZ=0 EndX=-44 EndY=34 EndZ=0
    g2: LineSegment StartX=-44 StartY=34 StartZ=0 EndX=-44 EndY=-34 EndZ=0
    g3: LineSegment StartX=-44 StartY=-34 StartZ=0 EndX=2 EndY=-34 EndZ=0
    g4: GeomPoint [constr] X=-21 Y=0 Z=0
  constraints (13):
    c: Coincident(g0,g1)
    c: Coincident(g1,g2)
    c: Coincident(g2,g3)
    c: Coincident(g3,g0)
    c: Vertical(g0)
    c: Vertical(g2)
    c: Horizontal(g1)
    c: Horizontal(g3)
    c: Symmetric(g2,g0,g4)
    c: PointOnObject(g4,g-1)
    c: DistanceX(g1,g1) = 46
    c: DistanceX(g4,g-1) = 21
    c: DistanceY(g2,g2) = 68
FEATURE [PartDesign::Pad] Pad010
  Direction = (0,0,-1)
  Length = 3
  Length2 = 10
  Profile = -> Sketch035
  ReferenceAxis = -> Sketch035 [N_Axis]
  Refine = true
  Suppressed = false
  Type = 0
FEATURE [PartDesign::Fillet] Fillet006
  Base = -> Pad010 [Edge5,Edge8]
  BaseFeature = -> Pad010
  Radius = 2
  Refine = true
  SupportTransform = false
  Suppressed = false
  UseAllEdges = false
FEATURE [Sketcher::SketchObject] Sketch036
  ArcFitTolerance = 1e-06
  AttachmentSupport = -> [Fillet006]
  FullyConstrained = true
  MakeInternals = false
  MapMode = 5
  Placement = pos=(0,0,42) rot=(1,0,0;3.14159rad)
  sketch-geometry (1):
    g0: Circle CenterX=-15.2 CenterY=15 CenterZ=0 NormalX=0 NormalY=0 NormalZ=1 AngleXU=0 Radius=1.7
  constraints (3):
    c: Diameter(g0) = 3.4
    c: DistanceY(g-1,g0) = 15
    c: DistanceX(g0,g-1) = 15.2
FEATURE [PartDesign::Pocket] Pocket028
  BaseFeature = -> Fillet006
  Direction = (0,0,1)
  Length = 5
  Length2 = 5
  Profile = -> Sketch036
  ReferenceAxis = -> Sketch036 [N_Axis]
  Refine = true
  Suppressed = false
  Type = 1
FEATURE [Sketcher::SketchObject] Sketch037
  ArcFitTolerance = 1e-06
  AttachmentSupport = -> [XZ_Plane]
  FullyConstrained = true
  MakeInternals = false
  MapMode = 5
  Placement = pos=(0,0,0) rot=(1,0,0;1.5708rad)
  sketch-geometry (3):
    g0: LineSegment StartX=-44.5 StartY=42 StartZ=0 EndX=-40.5 EndY=42 EndZ=0
    g1: LineSegment StartX=-40.5 StartY=42 StartZ=0 EndX=-44.5 EndY=38 EndZ=0
    g2: LineSegment StartX=-44.5 StartY=38 StartZ=0 EndX=-44.5 EndY=42 EndZ=0
  constraints (9):
    c: Horizontal(g0)
    c: Coincident(g1,g0)
    c: Coincident(g2,g1)
    c: Coincident(g2,g0)
    c: Vertical(g2)
    c: Angle(g1,g2) = 0.785398
    c: DistanceX(g0,g0) = 4
    c: Distance(g-2,g2) = 44.5
    c: DistanceY(g-1,g0) = 42
FEATURE [PartDesign::Pad] Pad011
  BaseFeature = -> Pocket009
  Direction = (0,-1,2e-16)
  Length = 25
  Length2 = 10
  Midplane = true
  Profile = -> Sketch037
  ReferenceAxis = -> Sketch037 [N_Axis]
  Refine = true
  Suppressed = false
  Type = 0
FEATURE [PartDesign::Fillet] Fillet007
  Base = -> Pad011 [Edge184]
  BaseFeature = -> Pad011
  Radius = 2
  Refine = true
  SupportTransform = false
  Suppressed = false
  UseAllEdges = false
FEATURE [Sketcher::SketchObject] Sketch040
  ArcFitTolerance = 1e-06
  AttachmentSupport = -> [Fillet007]
  ExternalGeometry = -> [Fillet007]
  FullyConstrained = true
  MakeInternals = false
  MapMode = 5
  Placement = pos=(47.5,0,0) rot=(0.57735,0.57735,0.57735;2.0944rad)
  sketch-geometry (2):
    g0: Circle CenterX=-7.5 CenterY=41 CenterZ=0 NormalX=0 NormalY=0 NormalZ=1 AngleXU=0 Radius=2.05
    g1: Circle CenterX=7.5 CenterY=41 CenterZ=0 NormalX=0 NormalY=0 NormalZ=1 AngleXU=0 Radius=2.05
  constraints (5):
    c: Diameter(g0) = 4.1
    c: Equal(g0,g1)
    c: Symmetric(g1,g0,g-2)
    c: DistanceX(g0,g1) = 15
    c: Distance(g1,g-3) = 4
FEATURE [PartDesign::Pocket] Pocket030
  BaseFeature = -> Fillet007
  Direction = (-1,0,0)
  Length = 5
  Length2 = 5
  Profile = -> Sketch040
  ReferenceAxis = -> Sketch040 [N_Axis]
  Refine = true
  Suppressed = false
  Type = 2
FEATURE [PartDesign::PolarPattern] PolarPattern
  Angle = 360
  Axis = -> Sketch002 [N_Axis]
  BaseFeature = -> Pocket030
  Mode = 0
  Occurrences = 4
  Offset = 120
  Originals = -> [Pocket001,Chamfer001]
  Refine = true
  Suppressed = false
  TransformMode = 0
FEATURE [PartDesign::Mirrored] Mirrored003
  BaseFeature = -> PolarPattern
  MirrorPlane = -> XY_Plane
  Originals = -> [Chamfer001,Pocket001]
  Refine = true
  Suppressed = false
  TransformMode = 0
FEATURE [Sketcher::SketchObject] Sketch043
  ArcFitTolerance = 1e-06
  FullyConstrained = true
  MakeInternals = false
  MapMode = 5
  Placement = pos=(0,0,95.5) rot=(0,0,1;0rad)
  sketch-geometry (6):
    g0: Circle CenterX=9 CenterY=27.5 CenterZ=0 NormalX=0 NormalY=0 NormalZ=1 AngleXU=0 Radius=5
    g1: LineSegment [constr] StartX=14.5 StartY=18.15 StartZ=0 EndX=14.5 EndY=32.85 EndZ=0
    g2: LineSegment [constr] StartX=14.5 StartY=32.85 StartZ=0 EndX=3.5 EndY=32.85 EndZ=0
    g3: LineSegment [constr] StartX=3.5 StartY=32.85 StartZ=0 EndX=3.5 EndY=18.15 EndZ=0
    g4: LineSegment [constr] StartX=3.5 StartY=18.15 StartZ=0 EndX=14.5 EndY=18.15 EndZ=0
    g5: GeomPoint [constr] X=9 Y=25.5 Z=0
  constraints (16):
    c: Diameter(g0) = 10
    c: Coincident(g1,g2)
    c: Coincident(g2,g3)
    c: Coincident(g3,g4)
    c: Coincident(g4,g1)
    c: Vertical(g1)
    c: Vertical(g3)
    c: Horizontal(g2)
    c: Horizontal(g4)
    c: Symmetric(g3,g1,g5)
    c: DistanceX(g2,g2) = 11
    c: Vertical(g0,g5)
    c: DistanceY(g1,g1) = 14.7
    c: DistanceY(g5,g0) = 2
    c: Distance(g0,g-3) = 10
    c: Distance(g0,g-4) = 10
FEATURE [PartDesign::Pocket] Pocket031
  BaseFeature = -> Pocket025
  Direction = (0,0,-1)
  Length = 5
  Length2 = 5
  Profile = -> Sketch043
  ReferenceAxis = -> Sketch043 [N_Axis]
  Refine = true
  Suppressed = false
  Type = 2
FEATURE [PartDesign::Chamfer] Chamfer006
  Angle = 45
  Base = -> Pocket031 [Edge17]
  BaseFeature = -> Pocket031
  ChamferType = 0
  FlipDirection = false
  Refine = true
  Size = 2
  Size2 = 1
  SupportTransform = false
  Suppressed = false
  UseAllEdges = false
FEATURE [Sketcher::SketchObject] Sketch044
  ArcFitTolerance = 1e-06
  AttachmentSupport = -> [Chamfer006]
  ExternalGeometry = -> [Chamfer006]
  FullyConstrained = false
  MakeInternals = false
  MapMode = 5
  Placement = pos=(0,34.5,0) rot=(1,0,0;1.5708rad)
  sketch-geometry (13):
    g0: LineSegment StartX=3 StartY=92.5 StartZ=0 EndX=3 EndY=91.2 EndZ=0
    g1: LineSegment StartX=3 StartY=91.2 StartZ=0 EndX=4 EndY=91.2 EndZ=0
    g2: LineSegment StartX=4 StartY=91.2 StartZ=0 EndX=4 EndY=89.2 EndZ=0
    g3: LineSegment StartX=4 StartY=89.2 StartZ=0 EndX=2 EndY=89.2 EndZ=0
    g4: LineSegment StartX=2 StartY=89.2 StartZ=0 EndX=2 EndY=92.5 EndZ=0
    g5: LineSegment StartX=2 StartY=92.5 StartZ=0 EndX=3 EndY=92.5 EndZ=0
    g6: LineSegment [constr] StartX=9 StartY=92.5 StartZ=0 EndX=9 EndY=84.8496 EndZ=0
    g7: LineSegment StartX=15 StartY=92.5 StartZ=0 EndX=15 EndY=91.2 EndZ=0
    g8: LineSegment StartX=15 StartY=91.2 StartZ=0 EndX=14 EndY=91.2 EndZ=0
    g9: LineSegment StartX=14 StartY=91.2 StartZ=0 EndX=14 EndY=89.2 EndZ=0
    g10: LineSegment StartX=14 StartY=89.2 StartZ=0 EndX=16 EndY=89.2 EndZ=0
    g11: LineSegment StartX=16 StartY=89.2 StartZ=0 EndX=16 EndY=92.5 EndZ=0
    g12: LineSegment StartX=16 StartY=92.5 StartZ=0 EndX=15 EndY=92.5 EndZ=0
  constraints (32):
    c: Vertical(g0)
    c: Coincident(g1,g0)
    c: Horizontal(g1)
    c: Coincident(g2,g1)
    c: Vertical(g2)
    c: Coincident(g3,g2)
    c: Horizontal(g3)
    c: Coincident(g4,g3)
    c: Vertical(g4)
    c: Coincident(g5,g4)
    c: Coincident(g5,g0)
    c: Horizontal(g5)
    c: Coincident(g4,g-4)
    c: DistanceY(g0,g0) = 1.3
    c: DistanceY(g2,g2) = 2
    c: DistanceX(g1,g1) = 1
    c: PointOnObject(g6,g-3)
    c: Vertical(g6)
    c: DistanceX(g-6,g6) = 10
    c: Distance(g6,g0) = 6
    c: Vertical(g7)
    c: Coincident(g8,g7)
    c: Horizontal(g8)
    c: Coincident(g9,g8)
    c: Vertical(g9)
    c: Coincident(g10,g9)
    c: Horizontal(g10)
    c: Coincident(g11,g10)
    c: Vertical(g11)
    c: Coincident(g12,g11)
    c: Coincident(g12,g7)
    c: Horizontal(g12)
FEATURE [PartDesign::Pad] Pad014
  BaseFeature = -> Chamfer006
  Direction = (0,-1,2e-16)
  Length = 20
  Length2 = 10
  Profile = -> Sketch044
  ReferenceAxis = -> Sketch044 [N_Axis]
  Refine = true
  Suppressed = false
  Type = 0
FEATURE [PartDesign::Chamfer] Chamfer007
  Angle = 45
  Base = -> Pad014 [Edge90]
  BaseFeature = -> Pad014
  ChamferType = 0
  FlipDirection = false
  Refine = true
  Size = 2
  Size2 = 1
  SupportTransform = false
  Suppressed = false
  UseAllEdges = false
FEATURE [Part::Feature] Part__Feature  label="OLED TFT 0.96 inch 64x128 monochrome"
  Placement = pos=(18.4,22.1,96) rot=(-0.57735,-0.57735,-0.57735;4.18879rad)
  shape: bbox 27.8 x 27.3 x 12.3 mm, 309 faces, 21 solids (baked)
FEATURE [Sketcher::SketchObject] Sketch046
  ArcFitTolerance = 1e-06
  FullyConstrained = true
  MakeInternals = false
  MapMode = 5
  Placement = pos=(0,0,95.5) rot=(0,0,1;0rad)
  sketch-geometry (8):
    g0: Circle [constr] CenterX=21 CenterY=-14 CenterZ=0 NormalX=0 NormalY=0 NormalZ=1 AngleXU=0 Radius=12
    g1: LineSegment StartX=23.25 StartY=-21.5 StartZ=0 EndX=26.75 EndY=-21.5 EndZ=0
    g2: LineSegment StartX=26.75 StartY=-21.5 StartZ=0 EndX=26.75 EndY=-6.5 EndZ=0
    g3: LineSegment StartX=26.75 StartY=-6.5 StartZ=0 EndX=23.25 EndY=-6.5 EndZ=0
    g4: LineSegment StartX=23.25 StartY=-6.5 StartZ=0 EndX=23.25 EndY=-21.5 EndZ=0
    g5: GeomPoint [constr] X=25 Y=-14 Z=0
    g6: Circle CenterX=21 CenterY=-29 CenterZ=0 NormalX=0 NormalY=0 NormalZ=1 AngleXU=0 Radius=2.05
    g7: Circle CenterX=21 CenterY=1 CenterZ=0 NormalX=0 NormalY=0 NormalZ=1 AngleXU=0 Radius=2.05
  constraints (21):
    c: Diameter(g0) = 24
    c: DistanceY(g0,g-1) = 14
    c: Coincident(g1,g2)
    c: Coincident(g2,g3)
    c: Coincident(g3,g4)
    c: Coincident(g4,g1)
    c: Horizontal(g1)
    c: Horizontal(g3)
    c: Vertical(g2)
    c: Vertical(g4)
    c: Symmetric(g3,g1,g5)
    c: DistanceX(g-1,g0) = 21
    c: DistanceX(g3,g3) = 3.5
    c: Horizontal(g5,g0)
    c: DistanceY(g2,g2) = 15
    c: Diameter(g6) = 4.1
    c: Equal(g7,g6)
    c: Vertical(g7,g0)
    c: Symmetric(g7,g6,g0)
    c: DistanceY(g6,g7) = 30
    c: DistanceX(g0,g5) = 4
FEATURE [PartDesign::Pocket] Pocket032
  BaseFeature = -> Chamfer007
  Direction = (0,0,-1)
  Length = 5
  Length2 = 5
  Profile = -> Sketch046
  ReferenceAxis = -> Sketch046 [N_Axis]
  Refine = true
  Suppressed = false
  Type = 1
FEATURE [PartDesign::ShapeBinder] CopyPocket032
  TraceSupport = false
FEATURE [Sketcher::SketchObject] Sketch047
  ArcFitTolerance = 1e-06
  AttachmentSupport = -> [CopyPocket032]
  FullyConstrained = true
  MakeInternals = false
  MapMode = 5
  Placement = pos=(0,0,95.5) rot=(0,0,1;0rad)
  sketch-geometry (2):
    g0: Circle CenterX=13 CenterY=-14 CenterZ=0 NormalX=0 NormalY=0 NormalZ=1 AngleXU=0 Radius=8.1
    g1: Circle CenterX=13 CenterY=-14 CenterZ=0 NormalX=0 NormalY=0 NormalZ=1 AngleXU=0 Radius=12.1
  constraints (5):
    c: Diameter(g0) = 16.2
    c: Coincident(g1,g0)
    c: Distance(g1,g0) = 4
    c: DistanceX(g-1,g0) = 13
    c: DistanceY(g0,g-1) = 14
FEATURE [PartDesign::Pad] Pad016
  Direction = (0,0,1)
  Length = 26
  Length2 = 10
  Profile = -> Sketch047
  ReferenceAxis = -> Sketch047 [N_Axis]
  Refine = true
  Suppressed = false
  Type = 0
FEATURE [PartDesign::Chamfer] Chamfer010
  Angle = 45
  Base = -> Pad016 [Edge3]
  BaseFeature = -> Pad016
  ChamferType = 0
  FlipDirection = false
  Refine = true
  Size = 1
  Size2 = 1
  SupportTransform = false
  Suppressed = false
  UseAllEdges = false
FEATURE [Sketcher::SketchObject] Sketch048
  ArcFitTolerance = 1e-06
  AttachmentSupport = -> [Chamfer010]
  ExternalGeometry = -> [Chamfer010]
  FullyConstrained = false
  MakeInternals = false
  MapMode = 5
  Placement = pos=(0,0,95.5) rot=(1,0,0;3.14159rad)
  sketch-geometry (10):
    g0: Circle CenterX=13 CenterY=29 CenterZ=0 NormalX=0 NormalY=0 NormalZ=1 AngleXU=0 Radius=1.7
    g1: Circle CenterX=13 CenterY=-1 CenterZ=0 NormalX=0 NormalY=0 NormalZ=1 AngleXU=0 Radius=1.7
    g2: ArcOfCircle CenterX=13 CenterY=29 CenterZ=0 NormalX=0 NormalY=0 NormalZ=1 AngleXU=0 Radius=3.7 StartAngle=4e-16 EndAngle=3.14159
    g3: LineSegment StartX=9.3 StartY=29 StartZ=0 EndX=9.3 EndY=25.5204 EndZ=0
    g4: LineSegment StartX=16.7 StartY=29 StartZ=0 EndX=16.7 EndY=25.5204 EndZ=0
    g5: ArcOfCircle CenterX=13 CenterY=14 CenterZ=0 NormalX=0 NormalY=0 NormalZ=1 AngleXU=0 Radius=12.1 StartAngle=1.26003 EndAngle=1.88156
    g6: ArcOfCircle CenterX=13 CenterY=-1 CenterZ=0 NormalX=0 NormalY=0 NormalZ=1 AngleXU=0 Radius=3.7 StartAngle=3.14159 EndAngle=6.28319
    g7: LineSegment StartX=16.7 StartY=-1 StartZ=0 EndX=16.7 EndY=2.47958 EndZ=0
    g8: ArcOfCircle CenterX=13 CenterY=14 CenterZ=0 NormalX=0 NormalY=0 NormalZ=1 AngleXU=0 Radius=12.1 StartAngle=4.40163 EndAngle=5.02315
    g9: LineSegment StartX=9.3 StartY=-1 StartZ=0 EndX=9.3 EndY=2.47958 EndZ=0
  constraints (24):
    c: Diameter(g0) = 3.4
    c: Diameter(g1) = 3.4
    c: DistanceY(g1,g0) = 30
    c: Vertical(g0,g-3)
    c: Symmetric(g1,g0,g-3)
    c: Coincident(g2,g0)
    c: Horizontal(g2,g0)
    c: Horizontal(g0,g2)
    c: Distance(g2,g0) = 2
    c: Coincident(g3,g2)
    c: PointOnObject(g3,g-3)
    c: Vertical(g3)
    c: Coincident(g4,g2)
    c: PointOnObject(g4,g-3)
    c: Vertical(g4)
    c: Coincident(g5,g3)
    c: Coincident(g5,g4)
    c: Equal(g5,g-3)
    c: Coincident(g7,g6)
    c: Vertical(g7)
    c: Coincident(g9,g6)
    c: Vertical(g9)
    c: Coincident(g8,g7)
    c: Coincident(g8,g9)
FEATURE [PartDesign::Pad] Pad017
  BaseFeature = -> Chamfer010
  Direction = (0,0,-1)
  Length = 3
  Length2 = 10
  Profile = -> Sketch048
  ReferenceAxis = -> Sketch048 [N_Axis]
  Refine = true
  Reversed = true
  Suppressed = false
  Type = 0
FEATURE [PartDesign::Fillet] Fillet011
  Base = -> Pad017 [Edge4,Edge6,Edge8,Edge10]
  BaseFeature = -> Pad017
  Radius = 2
  Refine = true
  SupportTransform = false
  Suppressed = false
  UseAllEdges = false
FEATURE [PartDesign::Body] Body010  label="SUPPORT_ARRETurgence"
  AllowCompound = false
  Group = -> [CopyPocket032,Sketch047,Pad016,Chamfer010,Sketch048,Pad017,Fillet011]
  Origin = -> Origin082
  Placement = pos=(8,0,0) rot=(0,0,1;0rad)
  Tip = -> Fillet011
FEATURE [PartDesign::Fillet] Fillet012
  Base = -> Pocket032 [Edge117,Edge119,Edge114,Edge115]
  BaseFeature = -> Pocket032
  Radius = 1
  Refine = true
  SupportTransform = false
  Suppressed = false
  UseAllEdges = false
FEATURE [PartDesign::Chamfer] Chamfer011
  Angle = 45
  Base = -> Fillet012 [Edge115,Edge133,Edge43]
  BaseFeature = -> Fillet012
  ChamferType = 0
  FlipDirection = false
  Refine = true
  Size = 0.4
  Size2 = 1
  SupportTransform = false
  Suppressed = false
  UseAllEdges = false
FEATURE [Sketcher::SketchObject] Sketch049
  ArcFitTolerance = 1e-06
  AttachmentSupport = -> [Chamfer011]
  ExternalGeometry = -> [Chamfer011]
  FullyConstrained = true
  MakeInternals = false
  MapMode = 5
  Placement = pos=(2,0,0) rot=(0.57735,0.57735,0.57735;2.0944rad)
  sketch-geometry (5):
    g0: LineSegment StartX=-2.5 StartY=48 StartZ=0 EndX=-2.5 EndY=45 EndZ=0
    g1: LineSegment StartX=-2.5 StartY=45 StartZ=0 EndX=2.5 EndY=45 EndZ=0
    g2: LineSegment StartX=2.5 StartY=45 StartZ=0 EndX=2.5 EndY=48 EndZ=0
    g3: LineSegment StartX=2.5 StartY=48 StartZ=0 EndX=-2.5 EndY=48 EndZ=0
    g4: GeomPoint [constr] X=0 Y=46.5 Z=0
  constraints (13):
    c: Coincident(g0,g1)
    c: Coincident(g1,g2)
    c: Coincident(g2,g3)
    c: Coincident(g3,g0)
    c: Vertical(g0)
    c: Vertical(g2)
    c: Horizontal(g1)
    c: Horizontal(g3)
    c: Symmetric(g2,g0,g4)
    c: PointOnObject(g4,g-2)
    c: DistanceX(g3,g3) = 5
    c: PointOnObject(g1,g-3)
    c: DistanceY(g2,g2) = 3
FEATURE [PartDesign::Pocket] Pocket033
  BaseFeature = -> Chamfer011
  Direction = (-1,0,0)
  Length = 5
  Length2 = 5
  Profile = -> Sketch049
  ReferenceAxis = -> Sketch049 [N_Axis]
  Refine = true
  Suppressed = false
  Type = 1
FEATURE [Sketcher::SketchObject] Sketch051
  ArcFitTolerance = 1e-06
  FullyConstrained = true
  MakeInternals = false
  MapMode = 5
  Placement = pos=(0,0,45) rot=(0,0,1;0rad)
  sketch-geometry (4):
    g0: ArcOfCircle CenterX=-27 CenterY=30 CenterZ=0 NormalX=0 NormalY=0 NormalZ=1 AngleXU=0 Radius=2.5 StartAngle=1.5708 EndAngle=4.71239
    g1: ArcOfCircle CenterX=-12 CenterY=30 CenterZ=0 NormalX=0 NormalY=0 NormalZ=1 AngleXU=0 Radius=2.5 StartAngle=4.71239 EndAngle=7.85398
    g2: LineSegment StartX=-27 StartY=32.5 StartZ=0 EndX=-12 EndY=32.5 EndZ=0
    g3: LineSegment StartX=-27 StartY=27.5 StartZ=0 EndX=-12 EndY=27.5 EndZ=0
  constraints (10):
    c: Tangent(g0,g2) = 1.5708
    c: Tangent(g0,g3) = -1.5708
    c: Tangent(g1,g2) = 1.5708
    c: Tangent(g1,g3) = -1.5708
    c: Equal(g0,g1)
    c: Horizontal(g3)
    c: Distance(g3,g2) = 5
    c: DistanceX(g0,g1) = 15
    c: DistanceX(g1,g-1) = 12
    c: DistanceY(g-1,g1) = 30
FEATURE [PartDesign::Pocket] Pocket035
  BaseFeature = -> Pocket028
  Direction = (0,0,-1)
  Length = 5
  Length2 = 5
  Profile = -> Sketch051
  ReferenceAxis = -> Sketch051 [N_Axis]
  Refine = true
  Suppressed = false
  Type = 1
FEATURE [Sketcher::SketchObject] Sketch052
  ArcFitTolerance = 1e-06
  AttachmentSupport = -> [Pocket033]
  FullyConstrained = false
  MakeInternals = false
  MapMode = 5
  Placement = pos=(0,0,95.5) rot=(0,0,1;0rad)
  sketch-geometry (17):
    g0: LineSegment [constr] StartX=44.6 StartY=9.35 StartZ=0 EndX=44.6 EndY=34.65 EndZ=0
    g1: LineSegment [constr] StartX=44.6 StartY=34.65 StartZ=0 EndX=18.4 EndY=34.65 EndZ=0
    g2: LineSegment [constr] StartX=18.4 StartY=34.65 StartZ=0 EndX=18.4 EndY=9.35 EndZ=0
    g3: LineSegment [constr] StartX=18.4 StartY=9.35 StartZ=0 EndX=44.6 EndY=9.35 EndZ=0
    g4: GeomPoint [constr] X=31.5 Y=22 Z=0
    g5: LineSegment StartX=18.4 StartY=16.8 StartZ=0 EndX=21.6 EndY=16.8 EndZ=0
    g6: LineSegment StartX=21.6 StartY=16.8 StartZ=0 EndX=21.6 EndY=27.2 EndZ=0
    g7: LineSegment StartX=21.6 StartY=27.2 StartZ=0 EndX=18.4 EndY=27.2 EndZ=0
    g8: LineSegment StartX=18.4 StartY=27.2 StartZ=0 EndX=18.4 EndY=16.8 EndZ=0
    g9: GeomPoint [constr] X=20 Y=22 Z=0
    g10: LineSegment [constr] StartX=42.5 StartY=11.25 StartZ=0 EndX=42.5 EndY=32.75 EndZ=0
    g11: LineSegment [constr] StartX=42.5 StartY=32.75 StartZ=0 EndX=20.5 EndY=32.75 EndZ=0
    g12: LineSegment [constr] StartX=20.5 StartY=32.75 StartZ=0 EndX=20.5 EndY=11.25 EndZ=0
    g13: LineSegment [constr] StartX=20.5 StartY=11.25 StartZ=0 EndX=42.5 EndY=11.25 EndZ=0
    g14: GeomPoint [constr] X=31.5 Y=22 Z=0
    g15: Circle CenterX=20.5 CenterY=32.75 CenterZ=0 NormalX=0 NormalY=0 NormalZ=1 AngleXU=0 Radius=1.15
    g16: Circle CenterX=20.5 CenterY=11.25 CenterZ=0 NormalX=0 NormalY=0 NormalZ=1 AngleXU=0 Radius=1.15
  constraints (41):
    c: Coincident(g0,g1)
    c: Coincident(g1,g2)
    c: Coincident(g2,g3)
    c: Coincident(g3,g0)
    c: Vertical(g0)
    c: Vertical(g2)
    c: Horizontal(g1)
    c: Horizontal(g3)
    c: Symmetric(g2,g0,g4)
    c: DistanceY(g2,g2) = 25.3
    c: DistanceY(g-1,g4) = 22
    c: DistanceX(g-1,g4) = 31.5
    c: Coincident(g5,g6)
    c: Coincident(g6,g7)
    c: Coincident(g7,g8)
    c: Coincident(g8,g5)
    c: Horizontal(g5)
    c: Horizontal(g7)
    c: Vertical(g6)
    c: Vertical(g8)
    c: Symmetric(g7,g5,g9)
    c: Horizontal(g9,g4)
    c: DistanceX(g7,g7) = 3.2
    c: DistanceY(g8,g8) = 10.4
    c: PointOnObject(g7,g2)
    c: DistanceX(g1,g1) = 26.2
    c: Coincident(g10,g11)
    c: Coincident(g11,g12)
    c: Coincident(g12,g13)
    c: Coincident(g13,g10)
    c: Vertical(g10)
    c: Vertical(g12)
    c: Horizontal(g11)
    c: Horizontal(g13)
    c: Symmetric(g12,g10,g14)
    c: Coincident(g14,g4)
    c: DistanceX(g11,g11) = 22
    c: DistanceY(g10,g10) = 21.5
    c: Diameter(g15) = 2.3
    c: Coincident(g15,g11)
    c: Coincident(g16,g12)
FEATURE [PartDesign::Pocket] Pocket036
  BaseFeature = -> Pocket033
  Direction = (0,0,-1)
  Length = 5
  Length2 = 5
  Profile = -> Sketch052
  ReferenceAxis = -> Sketch052 [N_Axis]
  Refine = true
  Suppressed = false
  Type = 1
FEATURE [Sketcher::SketchObject] Sketch053
  ArcFitTolerance = 1e-06
  AttachmentSupport = -> [Pocket036]
  ExternalGeometry = -> [Pocket036]
  FullyConstrained = true
  MakeInternals = false
  MapMode = 5
  Placement = pos=(0,0,45) rot=(1,0,0;3.14159rad)
  sketch-geometry (2):
    g0: Circle [constr] CenterX=4 CenterY=32.5 CenterZ=0 NormalX=0 NormalY=0 NormalZ=1 AngleXU=0 Radius=3.05
    g1: Circle CenterX=4 CenterY=32.5 CenterZ=0 NormalX=0 NormalY=0 NormalZ=1 AngleXU=0 Radius=5
  constraints (5):
    c: Diameter(g0) = 6.1
    c: DistanceX(g-1,g0) = 4
    c: DistanceY(g-1,g0) = 32.5
    c: Coincident(g1,g0)
    c: PointOnObject(g-3,g1)
FEATURE [PartDesign::Pad] Pad018
  BaseFeature = -> Pocket036
  Direction = (0,0,-1)
  Length = 6
  Length2 = 10
  Profile = -> Sketch053
  ReferenceAxis = -> Sketch053 [N_Axis]
  Refine = true
  Reversed = true
  Suppressed = false
  Type = 0
FEATURE [Sketcher::SketchObject] Sketch054
  ArcFitTolerance = 1e-06
  AttachmentSupport = -> [Pad018]
  ExternalGeometry = -> [Pad018]
  FullyConstrained = true
  MakeInternals = false
  MapMode = 5
  Placement = pos=(0,0,45) rot=(1,0,0;3.14159rad)
  sketch-geometry (1):
    g0: Circle CenterX=4 CenterY=32.5 CenterZ=0 NormalX=0 NormalY=0 NormalZ=1 AngleXU=0 Radius=3.05
  constraints (2):
    c: Coincident(g0,g-3)
    c: Diameter(g0) = 6.1
FEATURE [PartDesign::Pocket] Pocket037
  BaseFeature = -> Pad018
  Direction = (0,0,1)
  Length = 2.8
  Length2 = 5
  Profile = -> Sketch054
  ReferenceAxis = -> Sketch054 [N_Axis]
  Refine = true
  Suppressed = false
  Type = 0
FEATURE [PartDesign::Mirrored] Mirrored
  BaseFeature = -> Pocket037
  MirrorPlane = -> XZ_Plane078
  Originals = -> [Pad018]
  Refine = true
  Suppressed = false
  TransformMode = 0
FEATURE [PartDesign::Mirrored] Mirrored005
  BaseFeature = -> Mirrored
  MirrorPlane = -> XZ_Plane078
  Originals = -> [Pocket037]
  Refine = true
  Suppressed = false
  TransformMode = 0
FEATURE [PartDesign::Chamfer] Chamfer012
  Angle = 45
  Base = -> Mirrored005 [Edge242,Edge154]
  BaseFeature = -> Mirrored005
  ChamferType = 0
  FlipDirection = false
  Refine = true
  Size = 5
  Size2 = 1
  SupportTransform = false
  Suppressed = false
  UseAllEdges = false
FEATURE [Sketcher::SketchObject] Sketch055
  ArcFitTolerance = 1e-06
  AttachmentSupport = -> [Chamfer012]
  ExternalGeometry = -> [Chamfer012]
  FullyConstrained = true
  MakeInternals = false
  MapMode = 5
  Placement = pos=(-1,0,0) rot=(0.57735,-0.57735,-0.57735;2.0944rad)
  sketch-geometry (5):
    g0: LineSegment StartX=27 StartY=45 StartZ=0 EndX=27 EndY=87.5 EndZ=0
    g1: LineSegment StartX=27 StartY=87.5 StartZ=0 EndX=-27 EndY=87.5 EndZ=0
    g2: LineSegment StartX=-27 StartY=87.5 StartZ=0 EndX=-27 EndY=45 EndZ=0
    g3: LineSegment StartX=-27 StartY=45 StartZ=0 EndX=27 EndY=45 EndZ=0
    g4: GeomPoint [constr] X=0 Y=66.25 Z=0
  constraints (13):
    c: Coincident(g0,g1)
    c: Coincident(g1,g2)
    c: Coincident(g2,g3)
    c: Coincident(g3,g0)
    c: Vertical(g0)
    c: Vertical(g2)
    c: Horizontal(g1)
    c: Horizontal(g3)
    c: Symmetric(g2,g0,g4)
    c: PointOnObject(g4,g-2)
    c: PointOnObject(g2,g-4)
    c: DistanceX(g1,g1) = 54
    c: Distance(g-3,g1) = 8
FEATURE [PartDesign::Pocket] Pocket038
  BaseFeature = -> Chamfer012
  Direction = (1,0,0)
  Length = 5
  Length2 = 5
  Profile = -> Sketch055
  ReferenceAxis = -> Sketch055 [N_Axis]
  Refine = true
  Suppressed = false
  Type = 2
FEATURE [Part::Feature] Part__Feature338  label="C_0402_1005Metric"
  shape: bbox 1 x 0.5 x 0.5 mm, 28 faces (baked)
FEATURE [App::Part] C_0402_1005Metric  label="C_0402_1005Metric001"
  Group = -> [Part__Feature338]
  Origin = -> Origin083
  Placement = pos=(109.23,-94,1.65) rot=(0,0,1;3.14159rad)
FEATURE [Part::Feature] Part__Feature339  label="Unnamed1"
  shape: bbox 7.8 x 0.6 x 7.6 mm, 10 faces (baked)
FEATURE [Part::Feature] Part__Feature340  label="Unnamed002"
  shape: bbox 2.54 x 2.54 x 2.5 mm, 10 faces (baked)
FEATURE [Part::Feature] Part__Feature341  label="Unnamed003"
  shape: bbox 7.8 x 0.6 x 7.6 mm, 10 faces (baked)
FEATURE [Part::Feature] Part__Feature342  label="Unnamed004"
  shape: bbox 7.8 x 0.6 x 7.6 mm, 10 faces (baked)
FEATURE [Part::Feature] Part__Feature343  label="Unnamed005"
  shape: bbox 7.8 x 0.6 x 7.6 mm, 10 faces (baked)
FEATURE [Part::Feature] Part__Feature344  label="Unnamed006"
  shape: bbox 2.54 x 2.54 x 2.5 mm, 10 faces (baked)
FEATURE [Part::Feature] Part__Feature345  label="Unnamed007"
  shape: bbox 2.54 x 2.54 x 2.5 mm, 10 faces (baked)
FEATURE [Part::Feature] Part__Feature346  label="Unnamed008"
  shape: bbox 2.54 x 2.54 x 2.5 mm, 10 faces (baked)
FEATURE [App::Part] Unnamed1  label="Unnamed009"
  Group = -> [Part__Feature339,Part__Feature340,Part__Feature341,Part__Feature342,Part__Feature343,Part__Feature344,Part__Feature345,Part__Feature346]
  Origin = -> Origin084
FEATURE [App::Part] pinhead_h4
  Group = -> [Unnamed1]
  Origin = -> Origin085
  Placement = pos=(129.75,-103.37,1.65) rot=(0,0,1;0rad)
FEATURE [Part::Feature] Part__Feature347  label="C_0402_1005Metric002"
  shape: bbox 1 x 0.5 x 0.5 mm, 28 faces (baked)
FEATURE [App::Part] C_0402_1005Metric001  label="C_0402_1005Metric003"
  Group = -> [Part__Feature347]
  Origin = -> Origin086
  Placement = pos=(109.23,-96.75,1.65) rot=(0,0,1;3.14159rad)
FEATURE [Part::Feature] Part__Feature348  label="R_0402_1005Metric"
  shape: bbox 1 x 0.5 x 0.35 mm, 26 faces (baked)
FEATURE [App::Part] R_0402_1005Metric  label="R_0402_1005Metric001"
  Group = -> [Part__Feature348]
  Origin = -> Origin087
  Placement = pos=(113.76,-95.76,1.65) rot=(0,0,-1;1.5708rad)
FEATURE [Part::Feature] Part__Feature349  label="Corps001"
  shape: bbox 13 x 6 x 13 mm, 79 faces (baked)
FEATURE [App::Part] photo_inter_5mm
  Group = -> [Part__Feature349]
  Origin = -> Origin088
  Placement = pos=(100.19,-99.7,1.65) rot=(0,0,1;1.5708rad)
FEATURE [Part::Feature] Part__Feature350  label="R_0402_1005Metric002"
  shape: bbox 1 x 0.5 x 0.35 mm, 26 faces (baked)
FEATURE [App::Part] R_0402_1005Metric001  label="R_0402_1005Metric003"
  Group = -> [Part__Feature350]
  Origin = -> Origin089
  Placement = pos=(109.26,-104.75,1.65) rot=(0,0,1;0rad)
FEATURE [Part::Feature] Part__Feature351  label="R_0402_1005Metric004"
  shape: bbox 1 x 0.5 x 0.35 mm, 26 faces (baked)
FEATURE [App::Part] R_0402_1005Metric002  label="R_0402_1005Metric005"
  Group = -> [Part__Feature351]
  Origin = -> Origin090
  Placement = pos=(121.75,-95.76,1.65) rot=(0,0,-1;1.5708rad)
FEATURE [Part::Feature] Part__Feature352  label="SOIC_8_39x49mm_P127mm"
  shape: bbox 6 x 4.9 x 1.75 mm, 156 faces (baked)
FEATURE [App::Part] SOIC_8_3_9x4_9mm_P1_27mm  label="SOIC-8_3.9x4.9mm_P1.27mm"
  Group = -> [Part__Feature352]
  Origin = -> Origin091
  Placement = pos=(115.975,-103.655,1.65) rot=(0,0,1;3.14159rad)
FEATURE [Part::Feature] Part__Feature353  label="R_0402_1005Metric006"
  shape: bbox 1 x 0.5 x 0.35 mm, 26 faces (baked)
FEATURE [App::Part] R_0402_1005Metric003  label="R_0402_1005Metric007"
  Group = -> [Part__Feature353]
  Origin = -> Origin092
  Placement = pos=(122,-103.24,1.65) rot=(0,0,1;1.5708rad)
FEATURE [Part::Feature] Part__Feature354  label="R_0402_1005Metric008"
  shape: bbox 1 x 0.5 x 0.35 mm, 26 faces (baked)
FEATURE [App::Part] R_0402_1005Metric004  label="R_0402_1005Metric009"
  Group = -> [Part__Feature354]
  Origin = -> Origin093
  Placement = pos=(109.26,-99,1.65) rot=(0,0,1;0rad)
FEATURE [Part::Feature] Part__Feature355  label="LED_0805_2012Metric"
  shape: bbox 2 x 1.25 x 1.1 mm, 50 faces (baked)
FEATURE [App::Part] LED_0805_2012Metric  label="LED_0805_2012Metric001"
  Group = -> [Part__Feature355]
  Origin = -> Origin094
  Placement = pos=(125.438,-103.75,1.65) rot=(0,0,1;0rad)
FEATURE [Part::Feature] Part__Feature356  label="R_0402_1005Metric010"
  shape: bbox 1 x 0.5 x 0.35 mm, 26 faces (baked)
FEATURE [App::Part] R_0402_1005Metric005  label="R_0402_1005Metric011"
  Group = -> [Part__Feature356]
  Origin = -> Origin095
  Placement = pos=(109.26,-101.75,1.65) rot=(0,0,1;0rad)
FEATURE [Part::Feature] Part__Feature357  label="LED_0805_2012Metric002"
  shape: bbox 2 x 1.25 x 1.1 mm, 50 faces (baked)
FEATURE [App::Part] LED_0805_2012Metric001  label="LED_0805_2012Metric003"
  Group = -> [Part__Feature357]
  Origin = -> Origin096
  Placement = pos=(125.438,-95.25,1.65) rot=(0,0,1;0rad)
FEATURE [Part::Feature] Part__Feature358  label="R_0402_1005Metric012"
  shape: bbox 1 x 0.5 x 0.35 mm, 26 faces (baked)
FEATURE [App::Part] R_0402_1005Metric006  label="R_0402_1005Metric013"
  Group = -> [Part__Feature358]
  Origin = -> Origin097
  Placement = pos=(118.5,-95.76,1.65) rot=(0,0,-1;1.5708rad)
FEATURE [Part::Feature] Part__Feature359  label="techTaco_PCB"
  shape: bbox 31.25 x 14.25 x 1.6 mm, 15 faces (baked)
FEATURE [App::Part] techTaco_1  label="techTaco 1"
  Group = -> [C_0402_1005Metric,pinhead_h4,C_0402_1005Metric001,R_0402_1005Metric,photo_inter_5mm,R_0402_1005Metric001,R_0402_1005Metric002,SOIC_8_3_9x4_9mm_P1_27mm,R_0402_1005Metric003,R_0402_1005Metric004,LED_0805_2012Metric,R_0402_1005Metric005,LED_0805_2012Metric001,R_0402_1005Metric006,Part__Feature359]
  Origin = -> Origin098
  Placement = pos=(-121.5,24.9,176.2) rot=(-0.57735,0.57735,0.57735;2.0944rad)
FEATURE [Sketcher::SketchObject] Sketch056
  ArcFitTolerance = 1e-06
  AttachmentSupport = -> [Fillet002]
  FullyConstrained = true
  MakeInternals = false
  MapMode = 5
  Placement = pos=(-23.75,0,0) rot=(0.57735,-0.57735,-0.57735;2.0944rad)
  sketch-geometry (4):
    g0: LineSegment StartX=-19 StartY=31 StartZ=0 EndX=-19 EndY=-1 EndZ=0
    g1: LineSegment StartX=-19 StartY=-1 StartZ=0 EndX=-4 EndY=-1 EndZ=0
    g2: LineSegment StartX=-4 StartY=-1 StartZ=0 EndX=-4 EndY=31 EndZ=0
    g3: LineSegment StartX=-4 StartY=31 StartZ=0 EndX=-19 EndY=31 EndZ=0
  constraints (12):
    c: Coincident(g0,g1)
    c: Coincident(g1,g2)
    c: Coincident(g2,g3)
    c: Coincident(g3,g0)
    c: Vertical(g0)
    c: Vertical(g2)
    c: Horizontal(g1)
    c: Horizontal(g3)
    c: DistanceX(g3,g3) = 15
    c: DistanceY(g2,g2) = 32
    c: Distance(g-2,g2) = 4
    c: Distance(g-1,g1) = 1
FEATURE [PartDesign::Pocket] Pocket039
  BaseFeature = -> Fillet002
  Direction = (1,0,0)
  Length = 2
  Length2 = 5
  Profile = -> Sketch056
  ReferenceAxis = -> Sketch056 [N_Axis]
  Refine = true
  Suppressed = false
  Type = 0
FEATURE [Sketcher::SketchObject] Sketch057
  ArcFitTolerance = 1e-06
  AttachmentSupport = -> [Pocket039]
  ExternalGeometry = -> [Pocket039]
  FullyConstrained = true
  MakeInternals = false
  MapMode = 5
  Placement = pos=(0,0,-1) rot=(1,0,0;3.14159rad)
  sketch-geometry (8):
    g0: LineSegment StartX=-23.5832 StartY=-19 StartZ=0 EndX=-37.4832 EndY=-19 EndZ=0
    g1: ArcOfCircle CenterX=-10.45 CenterY=-16.8999 CenterZ=0 NormalX=0 NormalY=0 NormalZ=1 AngleXU=0 Radius=13.3 StartAngle=3.30016 EndAngle=4.00399
    g2: LineSegment StartX=-37.4832 StartY=-19 StartZ=0 EndX=-37.4832 EndY=-27 EndZ=0
    g3: LineSegment StartX=-37.4832 StartY=-27 StartZ=0 EndX=-19.1032 EndY=-27 EndZ=0
    g4: LineSegment StartX=-19.2492 StartY=-4 StartZ=0 EndX=-37.4832 EndY=-4 EndZ=0
    g5: LineSegment StartX=-37.4832 StartY=-4 StartZ=0 EndX=-37.4832 EndY=4 EndZ=0
    g6: LineSegment StartX=-37.4832 StartY=4 StartZ=0 EndX=-14.6304 EndY=4 EndZ=0
    g7: LineSegment StartX=-14.6304 StartY=4 StartZ=0 EndX=-19.2492 EndY=-4 EndZ=0
  constraints (23):
    c: Coincident(g0,g-3)
    c: Horizontal(g0)
    c: Coincident(g1,g-3)
    c: Coincident(g1,g0)
    c: Coincident(g2,g0)
    c: Vertical(g2)
    c: Coincident(g3,g2)
    c: Coincident(g3,g1)
    c: Horizontal(g3)
    c: DistanceY(g2,g2) = 8
    c: DistanceX(g0,g0) = 13.9
    c: PointOnObject(g4,g-4)
    c: Horizontal(g4)
    c: Vertical(g4,g0)
    c: PointOnObject(g-5,g4)
    c: Coincident(g5,g4)
    c: Vertical(g5)
    c: Coincident(g6,g5)
    c: PointOnObject(g6,g-4)
    c: Horizontal(g6)
    c: Coincident(g7,g6)
    c: Coincident(g7,g4)
    c: Equal(g5,g2)
FEATURE [PartDesign::Pad] Pad019
  BaseFeature = -> Pocket039
  Direction = (0,0,-1)
  Length = 31
  Length2 = 10
  Profile = -> Sketch057
  ReferenceAxis = -> Sketch057 [N_Axis]
  Refine = true
  Reversed = true
  Suppressed = false
  Type = 0
FEATURE [PartDesign::Chamfer] Chamfer013
  Angle = 45
  Base = -> Pad019 [Edge108]
  BaseFeature = -> Pad019
  ChamferType = 0
  FlipDirection = false
  Refine = true
  Size = 1.5
  Size2 = 1
  SupportTransform = false
  Suppressed = false
  UseAllEdges = false
FEATURE [PartDesign::Fillet] Fillet013
  Base = -> Chamfer013 [Edge11]
  BaseFeature = -> Chamfer013
  Radius = 2
  Refine = true
  SupportTransform = false
  Suppressed = false
  UseAllEdges = false
FEATURE [Sketcher::SketchObject] Sketch058
  ArcFitTolerance = 1e-06
  AttachmentSupport = -> [Fillet013]
  ExternalGeometry = -> [Fillet013]
  FullyConstrained = true
  MakeInternals = false
  MapMode = 5
  Placement = pos=(-37.4832,0,0) rot=(0.57735,-0.57735,-0.57735;2.0944rad)
  sketch-geometry (6):
    g0: Circle CenterX=-23 CenterY=9 CenterZ=0 NormalX=0 NormalY=0 NormalZ=1 AngleXU=0 Radius=2.05
    g1: Circle CenterX=2.343e-13 CenterY=9 CenterZ=0 NormalX=0 NormalY=0 NormalZ=1 AngleXU=0 Radius=2.05
    g2: LineSegment [constr] StartX=-27 StartY=-1 StartZ=0 EndX=-19 EndY=-1 EndZ=0
    g3: LineSegment [constr] StartX=-4 StartY=-1 StartZ=0 EndX=4 EndY=-1 EndZ=0
    g4: LineSegment [constr] StartX=2.343e-13 StartY=-1 StartZ=0 EndX=2.343e-13 EndY=9 EndZ=0
    g5: LineSegment [constr] StartX=-23 StartY=-1 StartZ=0 EndX=-23 EndY=9 EndZ=0
  constraints (14):
    c: Diameter(g0) = 4.1
    c: Equal(g1,g0)
    c: Coincident(g2,g-3)
    c: Coincident(g2,g-4)
    c: Coincident(g3,g-5)
    c: Coincident(g3,g-6)
    c: Symmetric(g3,g3,g4)
    c: Coincident(g4,g1)
    c: Vertical(g4)
    c: Symmetric(g2,g2,g5)
    c: Coincident(g5,g0)
    c: Vertical(g5)
    c: DistanceY(g5,g5) = 10
    c: Equal(g5,g4)
FEATURE [PartDesign::Pocket] Pocket040
  BaseFeature = -> Fillet013
  Direction = (1,0,0)
  Length = 6
  Length2 = 5
  Profile = -> Sketch058
  ReferenceAxis = -> Sketch058 [N_Axis]
  Refine = true
  Suppressed = false
  Type = 0
FEATURE [Part::Feature] Part__Feature360  label="SG90"
  shape: bbox 1.2 x 11.5 x 0.5 mm, 15 faces (baked)
FEATURE [Part::Feature] Part__Feature361  label="SG091"
  shape: bbox 12.3 x 26.3 x 23.6 mm, 2983 faces (baked)
FEATURE [Part::Feature] Part__Feature362  label="SG092"
  shape: bbox 12.3 x 2 x 5 mm, 10 faces (baked)
FEATURE [Part::Feature] Part__Feature363  label="SG093"
  shape: bbox 12.3 x 2 x 5 mm, 10 faces (baked)
FEATURE [Part::Feature] Part__Feature364  label="SG094"
  shape: bbox 1.2 x 11.5 x 0.5 mm, 15 faces (baked)
FEATURE [Part::Feature] Part__Feature365  label="SG095"
  shape: bbox 1.2 x 11.5 x 0.5 mm, 15 faces (baked)
FEATURE [Part::Feature] Part__Feature366  label="SG096"
  shape: bbox 8.498 x 12.5 x 8.487 mm, 786 faces (baked)
FEATURE [Part::Feature] Part__Feature367  label="SG097"
  shape: bbox 9.8 x 6.5 x 9 mm, 41 faces (baked)
FEATURE [Part::Feature] Part__Feature368  label="SG098"
  shape: bbox 12.3 x 11 x 22 mm, 434 faces (baked)
FEATURE [App::Part] SG90  label="SG099"
  Group = -> [Part__Feature360,Part__Feature361,Part__Feature362,Part__Feature363,Part__Feature364,Part__Feature365,Part__Feature366,Part__Feature367,Part__Feature368]
  Origin = -> Origin099
  Placement = pos=(-20.7,-30,47.6) rot=(0.57735,0.57735,0.57735;2.0944rad)
FEATURE [PartDesign::Fillet] Fillet014
  Base = -> Pocket040 [Edge251,Edge9]
  BaseFeature = -> Pocket040
  Radius = 5
  Refine = true
  SupportTransform = false
  Suppressed = false
  UseAllEdges = false
FEATURE [Sketcher::SketchObject] Sketch059
  ArcFitTolerance = 1e-06
  AttachmentSupport = -> [Fillet014]
  ExternalGeometry = -> [Fillet014]
  FullyConstrained = true
  MakeInternals = false
  MapMode = 5
  Placement = pos=(0,0,-1) rot=(1,0,0;3.14159rad)
  sketch-geometry (8):
    g0: ArcOfCircle CenterX=10.45 CenterY=-16.8999 CenterZ=0 NormalX=0 NormalY=0 NormalZ=1 AngleXU=0 Radius=13.3 StartAngle=5.06098 EndAngle=5.77256
    g1: LineSegment StartX=22.0534 StartY=-23.4 StartZ=0 EndX=37.5 EndY=-23.4 EndZ=0
    g2: LineSegment StartX=14.9929 StartY=-29.4 StartZ=0 EndX=37.5 EndY=-29.4 EndZ=0
    g3: LineSegment StartX=37.5 StartY=-29.4 StartZ=0 EndX=37.5 EndY=-23.4 EndZ=0
    g4: LineSegment StartX=17.2862 StartY=-0.6 StartZ=0 EndX=13.8221 EndY=5.4 EndZ=0
    g5: LineSegment StartX=17.2862 StartY=-0.6 StartZ=0 EndX=37.5 EndY=-0.6 EndZ=0
    g6: LineSegment StartX=13.8221 StartY=5.4 StartZ=0 EndX=37.5 EndY=5.4 EndZ=0
    g7: LineSegment StartX=37.5 StartY=5.4 StartZ=0 EndX=37.5 EndY=-0.6 EndZ=0
  constraints (24):
    c: Coincident(g0,g-4)
    c: PointOnObject(g0,g-4)
    c: Coincident(g1,g0)
    c: Horizontal(g1)
    c: Distance(g1,g-2) = 37.5
    c: Coincident(g2,g0)
    c: Horizontal(g2)
    c: Coincident(g3,g2)
    c: Coincident(g3,g1)
    c: Vertical(g3)
    c: DistanceY(g3,g3) = 6
    c: Distance(g-1,g1) = 23.4
    c: PointOnObject(g4,g-3)
    c: PointOnObject(g4,g-3)
    c: Coincident(g5,g4)
    c: Horizontal(g5)
    c: Coincident(g6,g4)
    c: Horizontal(g6)
    c: Coincident(g7,g6)
    c: Coincident(g7,g5)
    c: Vertical(g7)
    c: Vertical(g5,g1)
    c: Equal(g7,g3)
    c: Distance(g5,g-1) = 0.6
FEATURE [PartDesign::Pad] Pad020
  BaseFeature = -> Fillet014
  Direction = (0,0,-1)
  Length = 17.5
  Length2 = 10
  Profile = -> Sketch059
  ReferenceAxis = -> Sketch059 [N_Axis]
  Refine = true
  Reversed = true
  Suppressed = false
  Type = 0
FEATURE [Sketcher::SketchObject] Sketch060
  ArcFitTolerance = 1e-06
  AttachmentSupport = -> [Pad020]
  ExternalGeometry = -> [Pad020]
  FullyConstrained = false
  MakeInternals = false
  MapMode = 5
  Placement = pos=(0,0,16.5) rot=(0,0,1;0rad)
  sketch-geometry (4):
    g0: Circle CenterX=30 CenterY=-1.5 CenterZ=0 NormalX=0 NormalY=0 NormalZ=1 AngleXU=0 Radius=0.9
    g1: LineSegment [constr] StartX=37.5 StartY=23.4 StartZ=0 EndX=37.5 EndY=0.6 EndZ=0
    g2: LineSegment [constr] StartX=37.5 StartY=12 StartZ=0 EndX=23.9205 EndY=12 EndZ=0
    g3: Circle CenterX=30 CenterY=25.5 CenterZ=0 NormalX=0 NormalY=0 NormalZ=1 AngleXU=0 Radius=0.9
  constraints (9):
    c: DistanceX(g-1,g0) = 30
    c: Coincident(g1,g-3)
    c: Coincident(g1,g-4)
    c: Symmetric(g1,g1,g2)
    c: Horizontal(g2)
    c: Equal(g3,g0)
    c: Symmetric(g0,g3,g2)
    c: DistanceY(g0,g3) = 27
    c: Diameter(g0) = 1.8
FEATURE [PartDesign::Pocket] Pocket041
  BaseFeature = -> Pad020
  Direction = (0,0,-1)
  Length = 5
  Length2 = 5
  Profile = -> Sketch060
  ReferenceAxis = -> Sketch060 [N_Axis]
  Refine = true
  Suppressed = false
  Type = 0
FEATURE [Sketcher::SketchObject] Sketch061
  ArcFitTolerance = 1e-06
  AttachmentSupport = -> [Pocket041]
  ExternalGeometry = -> [Pocket041]
  FullyConstrained = true
  MakeInternals = false
  MapMode = 5
  Placement = pos=(37.5,0,0) rot=(0.57735,0.57735,0.57735;2.0944rad)
  sketch-geometry (6):
    g0: Circle CenterX=-2.4 CenterY=9 CenterZ=0 NormalX=0 NormalY=0 NormalZ=1 AngleXU=0 Radius=2.05
    g1: LineSegment [constr] StartX=-5.4 StartY=-1 StartZ=0 EndX=0.6 EndY=-1 EndZ=0
    g2: LineSegment [constr] StartX=-2.4 StartY=-1 StartZ=0 EndX=-2.4 EndY=9 EndZ=0
    g3: LineSegment [constr] StartX=23.4 StartY=-1 StartZ=0 EndX=29.4 EndY=-1 EndZ=0
    g4: LineSegment [constr] StartX=26.4 StartY=-1 StartZ=0 EndX=26.4 EndY=9 EndZ=0
    g5: Circle CenterX=26.4 CenterY=9 CenterZ=0 NormalX=0 NormalY=0 NormalZ=1 AngleXU=0 Radius=2.05
  constraints (14):
    c: Coincident(g1,g-3)
    c: Coincident(g1,g-4)
    c: Symmetric(g1,g1,g2)
    c: Coincident(g2,g0)
    c: Vertical(g2)
    c: DistanceY(g2,g2) = 10
    c: Diameter(g0) = 4.1
    c: Coincident(g3,g-5)
    c: Coincident(g3,g-6)
    c: Symmetric(g3,g3,g4)
    c: Vertical(g4)
    c: DistanceY(g4,g4) = 10
    c: Coincident(g5,g4)
    c: Equal(g5,g0)
FEATURE [PartDesign::Pocket] Pocket042
  BaseFeature = -> Pocket041
  Direction = (-1,0,0)
  Length = 6
  Length2 = 5
  Profile = -> Sketch061
  ReferenceAxis = -> Sketch061 [N_Axis]
  Refine = true
  Suppressed = false
  Type = 0
FEATURE [PartDesign::Fillet] Fillet015
  Base = -> Pocket042 [Edge187,Edge172]
  BaseFeature = -> Pocket042
  Radius = 5
  Refine = true
  SupportTransform = false
  Suppressed = false
  UseAllEdges = false
FEATURE [PartDesign::Chamfer] Chamfer014
  Angle = 45
  Base = -> Pocket038 [Edge221]
  BaseFeature = -> Pocket038
  ChamferType = 0
  FlipDirection = false
  Refine = true
  Size = 1
  Size2 = 1
  SupportTransform = false
  Suppressed = false
  UseAllEdges = false
FEATURE [PartDesign::Body] Body006  label="SupportElec"
  AllowCompound = false
  Group = -> [CopyPocket009,Sketch028,Pad007,Fillet003,Thickness001,Sketch029,Pocket024,Fillet004,Chamfer005,Sketch030,Pocket025,Sketch043,Pocket031,Chamfer006,Sketch044,Pad014,Chamfer007,Sketch046,Pocket032,Fillet012,Chamfer011,Sketch049,Pocket033,Sketch052,Pocket036,Sketch053,Pad018,Sketch054,Pocket037,Mirrored,Mirrored005,Chamfer012,Sketch055,Pocket038,Chamfer014]
  Origin = -> Origin078
  Tip = -> Chamfer014
FEATURE [Sketcher::SketchObject] Sketch062
  ArcFitTolerance = 1e-06
  AttachmentSupport = -> [Pocket035]
  FullyConstrained = true
  MakeInternals = false
  MapMode = 5
  Placement = pos=(0,0,42) rot=(1,0,0;3.14159rad)
  sketch-geometry (1):
    g0: Circle CenterX=4 CenterY=32.5 CenterZ=0 NormalX=0 NormalY=0 NormalZ=1 AngleXU=0 Radius=5.15
  constraints (3):
    c: Diameter(g0) = 10.3
    c: DistanceY(g-1,g0) = 32.5
    c: DistanceX(g-1,g0) = 4
FEATURE [PartDesign::Pocket] Pocket043
  BaseFeature = -> Pocket035
  Direction = (0,0,1)
  Length = 5
  Length2 = 5
  Profile = -> Sketch062
  ReferenceAxis = -> Sketch062 [N_Axis]
  Refine = true
  Suppressed = false
  Type = 1
FEATURE [PartDesign::Mirrored] Mirrored006
  BaseFeature = -> Pocket043
  MirrorPlane = -> XZ_Plane080
  Originals = -> [Pocket043,Pocket028]
  Refine = true
  Suppressed = false
  TransformMode = 0
FEATURE [Sketcher::SketchObject] Sketch063
  ArcFitTolerance = 1e-06
  AttachmentSupport = -> [Mirrored006]
  FullyConstrained = true
  MakeInternals = false
  MapMode = 5
  Placement = pos=(0,0,42) rot=(1,0,0;3.14159rad)
  sketch-geometry (4):
    g0: ArcOfCircle CenterX=-28 CenterY=10 CenterZ=0 NormalX=0 NormalY=0 NormalZ=1 AngleXU=0 Radius=6 StartAngle=3e-16 EndAngle=3.14159
    g1: ArcOfCircle CenterX=-28 CenterY=-10 CenterZ=0 NormalX=0 NormalY=0 NormalZ=1 AngleXU=0 Radius=6 StartAngle=3.14159 EndAngle=6.28319
    g2: LineSegment StartX=-22 StartY=10 StartZ=0 EndX=-22 EndY=-10 EndZ=0
    g3: LineSegment StartX=-34 StartY=10 StartZ=0 EndX=-34 EndY=-10 EndZ=0
  constraints (9):
    c: Tangent(g0,g2) = 1.5708
    c: Tangent(g0,g3) = -1.5708
    c: Tangent(g1,g2) = 1.5708
    c: Tangent(g1,g3) = -1.5708
    c: Equal(g0,g1)
    c: Symmetric(g0,g1,g-1)
    c: DistanceY(g1,g0) = 20
    c: Distance(g2,g3) = 12
    c: Distance(g-2,g2) = 22
FEATURE [PartDesign::Pocket] Pocket044
  BaseFeature = -> Mirrored006
  Direction = (0,0,1)
  Length = 5
  Length2 = 5
  Profile = -> Sketch063
  ReferenceAxis = -> Sketch063 [N_Axis]
  Refine = true
  Suppressed = false
  Type = 1
FEATURE [PartDesign::Body] Body008  label="PLAQUE COUVERTURE"
  AllowCompound = false
  Group = -> [CopyMirrored,Sketch035,Pad010,Fillet006,Sketch036,Pocket028,Sketch051,Pocket035,Sketch062,Pocket043,Mirrored006,Sketch063,Pocket044]
  Origin = -> Origin080
  Tip = -> Pocket044
FEATURE [PartDesign::ShapeBinder] CopyMirrored003
  TraceSupport = false
FEATURE [Sketcher::SketchObject] Sketch064
  ArcFitTolerance = 1e-06
  AttachmentSupport = -> [CopyMirrored003]
  FullyConstrained = true
  MakeInternals = false
  MapMode = 5
  Placement = pos=(0,0,0) rot=(1,0,0;3.14159rad)
  sketch-geometry (5):
    g0: LineSegment StartX=46.5 StartY=-36.5 StartZ=0 EndX=46.5 EndY=36.5 EndZ=0
    g1: LineSegment StartX=46.5 StartY=36.5 StartZ=0 EndX=-46.5 EndY=36.5 EndZ=0
    g2: LineSegment StartX=-46.5 StartY=36.5 StartZ=0 EndX=-46.5 EndY=-36.5 EndZ=0
    g3: LineSegment StartX=-46.5 StartY=-36.5 StartZ=0 EndX=46.5 EndY=-36.5 EndZ=0
    g4: GeomPoint [constr] X=0 Y=0 Z=0
  constraints (12):
    c: Coincident(g0,g1)
    c: Coincident(g1,g2)
    c: Coincident(g2,g3)
    c: Coincident(g3,g0)
    c: Vertical(g0)
    c: Vertical(g2)
    c: Horizontal(g1)
    c: Horizontal(g3)
    c: Symmetric(g2,g0,g4)
    c: Coincident(g4,g-1)
    c: DistanceX(g1,g1) = 93
    c: DistanceY(g2,g2) = 73
FEATURE [PartDesign::Pad] Pad021
  Direction = (0,0,-1)
  Length = 3
  Length2 = 10
  Profile = -> Sketch064
  ReferenceAxis = -> Sketch064 [N_Axis]
  Refine = true
  Suppressed = false
  Type = 0
FEATURE [PartDesign::Fillet] Fillet016
  Base = -> Pad021 [Edge8,Edge5,Edge2,Edge1]
  BaseFeature = -> Pad021
  Radius = 4
  Refine = true
  SupportTransform = false
  Suppressed = false
  UseAllEdges = false
FEATURE [Sketcher::SketchObject] Sketch065
  ArcFitTolerance = 1e-06
  AttachmentSupport = -> [Fillet016]
  FullyConstrained = true
  MakeInternals = false
  MapMode = 5
  Placement = pos=(0,0,-3) rot=(1,0,0;3.14159rad)
  sketch-geometry (9):
    g0: LineSegment [constr] StartX=40 StartY=-30 StartZ=0 EndX=40 EndY=30 EndZ=0
    g1: LineSegment [constr] StartX=40 StartY=30 StartZ=0 EndX=-40 EndY=30 EndZ=0
    g2: LineSegment [constr] StartX=-40 StartY=30 StartZ=0 EndX=-40 EndY=-30 EndZ=0
    g3: LineSegment [constr] StartX=-40 StartY=-30 StartZ=0 EndX=40 EndY=-30 EndZ=0
    g4: GeomPoint [constr] X=0 Y=0 Z=0
    g5: Circle CenterX=-40 CenterY=30 CenterZ=0 NormalX=0 NormalY=0 NormalZ=1 AngleXU=0 Radius=1.65
    g6: Circle CenterX=-40 CenterY=-30 CenterZ=0 NormalX=0 NormalY=0 NormalZ=1 AngleXU=0 Radius=1.65
    g7: Circle CenterX=40 CenterY=30 CenterZ=0 NormalX=0 NormalY=0 NormalZ=1 AngleXU=0 Radius=1.65
    g8: Circle CenterX=40 CenterY=-30 CenterZ=0 NormalX=0 NormalY=0 NormalZ=1 AngleXU=0 Radius=1.65
  constraints (20):
    c: Coincident(g0,g1)
    c: Coincident(g1,g2)
    c: Coincident(g2,g3)
    c: Coincident(g3,g0)
    c: Vertical(g0)
    c: Vertical(g2)
    c: Horizontal(g1)
    c: Horizontal(g3)
    c: Symmetric(g2,g0,g4)
    c: Coincident(g4,g-1)
    c: DistanceX(g1,g1) = 80
    c: DistanceY(g2,g2) = 60
    c: Coincident(g5,g1)
    c: Diameter(g5) = 3.3
    c: Coincident(g6,g2)
    c: Equal(g6,g5)
    c: Coincident(g7,g0)
    c: Coincident(g8,g0)
    c: Equal(g8,g5)
    c: Equal(g5,g7)
FEATURE [PartDesign::Pocket] Pocket045
  BaseFeature = -> Fillet016
  Direction = (0,0,1)
  Length = 5
  Length2 = 5
  Profile = -> Sketch065
  ReferenceAxis = -> Sketch065 [N_Axis]
  Refine = true
  Suppressed = false
  Type = 1
FEATURE [Sketcher::SketchObject] Sketch066
  ArcFitTolerance = 1e-06
  AttachmentSupport = -> [Fillet015]
  ExternalGeometry = -> [Fillet015]
  FullyConstrained = true
  MakeInternals = false
  MapMode = 5
  Placement = pos=(-21.75,0,0) rot=(0.57735,-0.57735,-0.57735;2.0944rad)
  sketch-geometry (3):
    g0: LineSegment [constr] StartX=-19 StartY=30 StartZ=0 EndX=-4 EndY=30 EndZ=0
    g1: LineSegment [constr] StartX=-11.5 StartY=30 StartZ=0 EndX=-11.5 EndY=6 EndZ=0
    g2: Circle CenterX=-11.5 CenterY=6 CenterZ=0 NormalX=0 NormalY=0 NormalZ=1 AngleXU=0 Radius=1.45
  constraints (7):
    c: Coincident(g0,g-4)
    c: Coincident(g0,g-3)
    c: Symmetric(g0,g0,g1)
    c: Vertical(g1)
    c: DistanceY(g1,g1) = 24
    c: Coincident(g2,g1)
    c: Diameter(g2) = 2.9
FEATURE [PartDesign::Pocket] Pocket046
  BaseFeature = -> Fillet015
  Direction = (1,0,0)
  Length = 5
  Length2 = 5
  Profile = -> Sketch066
  ReferenceAxis = -> Sketch066 [N_Axis]
  Refine = true
  Suppressed = false
  Type = 0
FEATURE [Sketcher::SketchObject] Sketch067
  ArcFitTolerance = 1e-06
  AttachmentSupport = -> [Mirrored003]
  FullyConstrained = true
  MakeInternals = false
  MapMode = 5
  Placement = pos=(0,0,45) rot=(0,0,1;0rad)
  sketch-geometry (1):
    g0: Circle CenterX=4 CenterY=32.5 CenterZ=0 NormalX=0 NormalY=0 NormalZ=1 AngleXU=0 Radius=5
  constraints (3):
    c: Diameter(g0) = 10
    c: DistanceX(g-1,g0) = 4
    c: DistanceY(g-1,g0) = 32.5
FEATURE [PartDesign::Pad] Pad022
  BaseFeature = -> Mirrored003
  Direction = (0,0,1)
  Length = 5
  Length2 = 10
  Profile = -> Sketch067
  ReferenceAxis = -> Sketch067 [N_Axis]
  Refine = true
  Reversed = true
  Suppressed = false
  Type = 0
FEATURE [Sketcher::SketchObject] Sketch068
  ArcFitTolerance = 1e-06
  AttachmentSupport = -> [Pad022]
  ExternalGeometry = -> [Pad022]
  FullyConstrained = true
  MakeInternals = false
  MapMode = 5
  Placement = pos=(0,0,45) rot=(0,0,1;0rad)
  sketch-geometry (1):
    g0: Circle CenterX=4 CenterY=32.5 CenterZ=0 NormalX=0 NormalY=0 NormalZ=1 AngleXU=0 Radius=3.05
  constraints (2):
    c: Coincident(g0,g-3)
    c: Diameter(g0) = 6.1
FEATURE [PartDesign::Pocket] Pocket047
  BaseFeature = -> Pad022
  Direction = (0,0,-1)
  Length = 2.8
  Length2 = 5
  Profile = -> Sketch068
  ReferenceAxis = -> Sketch068 [N_Axis]
  Refine = true
  Suppressed = false
  Type = 0
FEATURE [PartDesign::Mirrored] Mirrored007
  BaseFeature = -> Pocket047
  MirrorPlane = -> XZ_Plane
  Originals = -> [Pad022,Pocket047]
  Refine = true
  Suppressed = false
  TransformMode = 0
FEATURE [PartDesign::Chamfer] Chamfer015
  Angle = 45
  Base = -> Mirrored007 [Edge85,Edge122]
  BaseFeature = -> Mirrored007
  ChamferType = 0
  FlipDirection = false
  Refine = true
  Size = 6.5
  Size2 = 1
  SupportTransform = false
  Suppressed = false
  UseAllEdges = false
FEATURE [Sketcher::SketchObject] Sketch069
  ArcFitTolerance = 1e-06
  AttachmentSupport = -> [Pocket045]
  ExternalGeometry = -> [Pocket045]
  FullyConstrained = true
  MakeInternals = false
  MapMode = 5
  Placement = pos=(0,0,-3) rot=(1,0,0;3.14159rad)
  sketch-geometry (5):
    g0: LineSegment StartX=-52.5 StartY=-15 StartZ=0 EndX=-46.5 EndY=-15 EndZ=0
    g1: LineSegment StartX=-46.5 StartY=-15 StartZ=0 EndX=-46.5 EndY=15 EndZ=0
    g2: LineSegment StartX=-46.5 StartY=15 StartZ=0 EndX=-52.5 EndY=15 EndZ=0
    g3: LineSegment StartX=-52.5 StartY=15 StartZ=0 EndX=-52.5 EndY=-15 EndZ=0
    g4: GeomPoint [constr] X=-49.5 Y=0 Z=0
  constraints (13):
    c: Coincident(g0,g1)
    c: Coincident(g1,g2)
    c: Coincident(g2,g3)
    c: Coincident(g3,g0)
    c: Horizontal(g0)
    c: Horizontal(g2)
    c: Vertical(g1)
    c: Vertical(g3)
    c: Symmetric(g2,g0,g4)
    c: PointOnObject(g4,g-1)
    c: PointOnObject(g1,g-3)
    c: DistanceX(g2,g2) = 6
    c: DistanceY(g3,g3) = 30
FEATURE [PartDesign::Pad] Pad023
  BaseFeature = -> Pocket045
  Direction = (0,0,-1)
  Length = 10
  Length2 = 10
  Profile = -> Sketch069
  ReferenceAxis = -> Sketch069 [N_Axis]
  Refine = true
  Suppressed = false
  Type = 3
  UpToFace = -> Pocket045 [Face2]
FEATURE [PartDesign::Chamfer] Chamfer016
  Angle = 45
  Base = -> Pad023 [Edge34,Edge30,Edge24,Edge28]
  BaseFeature = -> Pad023
  ChamferType = 0
  FlipDirection = false
  Refine = true
  Size = 1
  Size2 = 1
  SupportTransform = false
  Suppressed = false
  UseAllEdges = false
FEATURE [Sketcher::SketchObject] Sketch070
  ArcFitTolerance = 1e-06
  AttachmentSupport = -> [Chamfer015]
  FullyConstrained = true
  MakeInternals = false
  MapMode = 5
  Placement = pos=(-47.5,0,0) rot=(0.57735,-0.57735,-0.57735;2.0944rad)
  sketch-geometry (7):
    g0: Circle CenterX=-10 CenterY=10 CenterZ=0 NormalX=0 NormalY=0 NormalZ=1 AngleXU=0 Radius=1.45
    g1: Circle CenterX=10 CenterY=10 CenterZ=0 NormalX=0 NormalY=0 NormalZ=1 AngleXU=0 Radius=1.45
    g2: LineSegment StartX=-7.7 StartY=3.35 StartZ=0 EndX=7.7 EndY=3.35 EndZ=0
    g3: LineSegment StartX=7.7 StartY=3.35 StartZ=0 EndX=7.7 EndY=6.65 EndZ=0
    g4: LineSegment StartX=7.7 StartY=6.65 StartZ=0 EndX=-7.7 EndY=6.65 EndZ=0
    g5: LineSegment StartX=-7.7 StartY=6.65 StartZ=0 EndX=-7.7 EndY=3.35 EndZ=0
    g6: GeomPoint [constr] X=0 Y=5 Z=0
  constraints (18):
    c: Diameter(g0) = 2.9
    c: Equal(g1,g0)
    c: Symmetric(g0,g1,g-2)
    c: DistanceX(g0,g1) = 20
    c: Distance(g1,g-1) = 10
    c: Coincident(g2,g3)
    c: Coincident(g3,g4)
    c: Coincident(g4,g5)
    c: Coincident(g5,g2)
    c: Horizontal(g2)
    c: Horizontal(g4)
    c: Vertical(g3)
    c: Vertical(g5)
    c: Symmetric(g4,g2,g6)
    c: PointOnObject(g6,g-2)
    c: DistanceY(g6,g1) = 5
    c: DistanceY(g3,g3) = 3.3
    c: DistanceX(g4,g4) = 15.4
FEATURE [PartDesign::Pocket] Pocket048
  BaseFeature = -> Chamfer015
  Direction = (1,0,0)
  Length = 5
  Length2 = 5
  Profile = -> Sketch070
  ReferenceAxis = -> Sketch070 [N_Axis]
  Refine = true
  Suppressed = false
  Type = 2
FEATURE [Sketcher::SketchObject] Sketch071
  ArcFitTolerance = 1e-06
  AttachmentSupport = -> [YZ_Plane]
  ExternalGeometry = -> [Pocket048]
  FullyConstrained = true
  MakeInternals = false
  MapMode = 5
  Placement = pos=(0,0,0) rot=(0.57735,0.57735,0.57735;2.0944rad)
  sketch-geometry (3):
    g0: LineSegment StartX=-34.5 StartY=42 StartZ=0 EndX=-30.5 EndY=42 EndZ=0
    g1: LineSegment StartX=-30.5 StartY=42 StartZ=0 EndX=-34.5 EndY=38 EndZ=0
    g2: LineSegment StartX=-34.5 StartY=38 StartZ=0 EndX=-34.5 EndY=42 EndZ=0
  constraints (9):
    c: PointOnObject(g0,g-4)
    c: Horizontal(g0)
    c: Coincident(g1,g0)
    c: PointOnObject(g1,g-4)
    c: Coincident(g2,g1)
    c: Coincident(g2,g0)
    c: Horizontal(g0,g-3)
    c: Angle(g1,g2) = 0.785398
    c: DistanceX(g0,g0) = 4
FEATURE [PartDesign::Pad] Pad024
  BaseFeature = -> Pocket048
  Direction = (1,0,0)
  Length = 8
  Length2 = 10
  Profile = -> Sketch071
  ReferenceAxis = -> Sketch071 [N_Axis]
  Refine = true
  Reversed = true
  Suppressed = false
  Type = 0
FEATURE [PartDesign::Mirrored] Mirrored008
  BaseFeature = -> Pad024
  MirrorPlane = -> Sketch071 [V_Axis]
  Originals = -> [Pad024]
  Refine = true
  Suppressed = false
  TransformMode = 0
FEATURE [PartDesign::Body] Body  label="BASE"
  AllowCompound = false
  Group = -> [Sketch,Pad,Fillet,Chamfer,Thickness,Sketch001,Pocket,Fillet001,Sketch002,Pocket001,Chamfer001,Sketch003,Pocket002,Sketch004,Pocket003,Sketch005,Pocket004,DatumLine,Sketch006,Pocket005,PolarPattern001,Sketch007,Pocket006,PolarPattern002,Sketch008,Pocket007,Chamfer002,Sketch010,Pocket008,Sketch012,Pocket009,Sketch037,Pad011,Fillet007,Sketch040,Pocket030,PolarPattern,Mirrored003,Sketch067,Pad022,+9 more]
  Origin = -> Origin
  Tip = -> Mirrored008
FEATURE [Sketcher::SketchObject] Sketch072
  ArcFitTolerance = 1e-06
  AttachmentSupport = -> [Pocket046]
  ExternalGeometry = -> [Pocket046]
  FullyConstrained = true
  MakeInternals = false
  MapMode = 5
  Placement = pos=(0,29.4,0) rot=(0,0.707107,0.707107;3.14159rad)
  sketch-geometry (5):
    g0: LineSegment StartX=-26.2 StartY=2.2 StartZ=0 EndX=-34.2 EndY=2.2 EndZ=0
    g1: LineSegment StartX=-34.2 StartY=2.2 StartZ=0 EndX=-34.2 EndY=-1 EndZ=0
    g2: LineSegment StartX=-34.2 StartY=-1 StartZ=0 EndX=-26.2 EndY=-1 EndZ=0
    g3: LineSegment StartX=-26.2 StartY=-1 StartZ=0 EndX=-26.2 EndY=2.2 EndZ=0
    g4: GeomPoint [constr] X=-30.2 Y=0.6 Z=0
  constraints (13):
    c: Coincident(g0,g1)
    c: Coincident(g1,g2)
    c: Coincident(g2,g3)
    c: Coincident(g3,g0)
    c: Horizontal(g0)
    c: Horizontal(g2)
    c: Vertical(g1)
    c: Vertical(g3)
    c: Symmetric(g2,g0,g4)
    c: PointOnObject(g1,g-3)
    c: DistanceX(g0,g0) = 8
    c: DistanceX(g4,g-1) = 30.2
    c: Distance(g4,g-3) = 1.6
FEATURE [PartDesign::Pocket] Pocket049
  BaseFeature = -> Pocket046
  Direction = (0,-1,2e-16)
  Length = 5
  Length2 = 5
  Profile = -> Sketch072
  ReferenceAxis = -> Sketch072 [N_Axis]
  Refine = true
  Suppressed = false
  Type = 2
FEATURE [PartDesign::Chamfer] Chamfer017
  Angle = 45
  Base = -> Pocket049 [Edge211,Edge344]
  BaseFeature = -> Pocket049
  ChamferType = 0
  FlipDirection = false
  Refine = true
  Size = 1
  Size2 = 1
  SupportTransform = false
  Suppressed = false
  UseAllEdges = false
FEATURE [PartDesign::Body] Body005  label="holder"
  AllowCompound = false
  Group = -> [Sketch016,Sketch017,Pad005,Pocket011,Sketch018,Binder,Pocket012,Pocket013,Pocket014,Sketch019,Pocket015,Sketch020,Pocket016,Sketch021,Pocket017,Sketch023,Pocket019,Sketch024,Pocket020,Sketch025,Pad006,Chamfer004,Pocket021,Sketch026,Pocket022,LinearPattern,Sketch027,Pocket023,Mirrored001,Sketch022,Pocket018,Fillet002,Sketch056,Pocket039,Sketch057,Pad019,Chamfer013,Fillet013,Sketch058,Pocket040,+13 more]
  Origin = -> Origin005
  Placement = pos=(-33.2,-1.3e-15,46) rot=(0,0,1;4.71239rad)
  Tip = -> Chamfer017
FEATURE [Sketcher::SketchObject] Sketch073
  ArcFitTolerance = 1e-06
  AttachmentSupport = -> [Chamfer016]
  FullyConstrained = true
  MakeInternals = false
  MapMode = 5
  Placement = pos=(0,0,-3) rot=(1,0,0;3.14159rad)
  sketch-geometry (4):
    g0: ArcOfCircle CenterX=-34 CenterY=20 CenterZ=0 NormalX=0 NormalY=0 NormalZ=1 AngleXU=0 Radius=2 StartAngle=-8e-15 EndAngle=3.14159
    g1: ArcOfCircle CenterX=-34 CenterY=-20 CenterZ=0 NormalX=0 NormalY=0 NormalZ=1 AngleXU=0 Radius=2 StartAngle=3.14159 EndAngle=6.28319
    g2: LineSegment StartX=-32 StartY=20 StartZ=0 EndX=-32 EndY=-20 EndZ=0
    g3: LineSegment StartX=-36 StartY=20 StartZ=0 EndX=-36 EndY=-20 EndZ=0
  constraints (9):
    c: Tangent(g0,g2) = 1.5708
    c: Tangent(g0,g3) = -1.5708
    c: Tangent(g1,g2) = 1.5708
    c: Tangent(g1,g3) = -1.5708
    c: Equal(g0,g1)
    c: Symmetric(g0,g1,g-1)
    c: DistanceY(g1,g0) = 40
    c: Distance(g2,g3) = 4
    c: DistanceX(g0,g-1) = 34
FEATURE [PartDesign::Pocket] Pocket050
  BaseFeature = -> Chamfer016
  Direction = (0,0,1)
  Length = 5
  Length2 = 5
  Profile = -> Sketch073
  ReferenceAxis = -> Sketch073 [N_Axis]
  Refine = true
  Suppressed = false
  Type = 1
FEATURE [PartDesign::LinearPattern] LinearPattern001
  BaseFeature = -> Pocket050
  Direction = -> X_Axis100
  Length = 30
  Mode = 1
  Occurrences = 4
  Offset = 10
  Originals = -> [Pocket050]
  Refine = true
  Suppressed = false
  TransformMode = 0
FEATURE [PartDesign::Body] Body011  label="Plaque BAS"
  AllowCompound = false
  Group = -> [CopyMirrored003,Sketch064,Pad021,Fillet016,Sketch065,Pocket045,Sketch069,Pad023,Chamfer016,Sketch073,Pocket050,LinearPattern001]
  Origin = -> Origin100
  Tip = -> LinearPattern001
